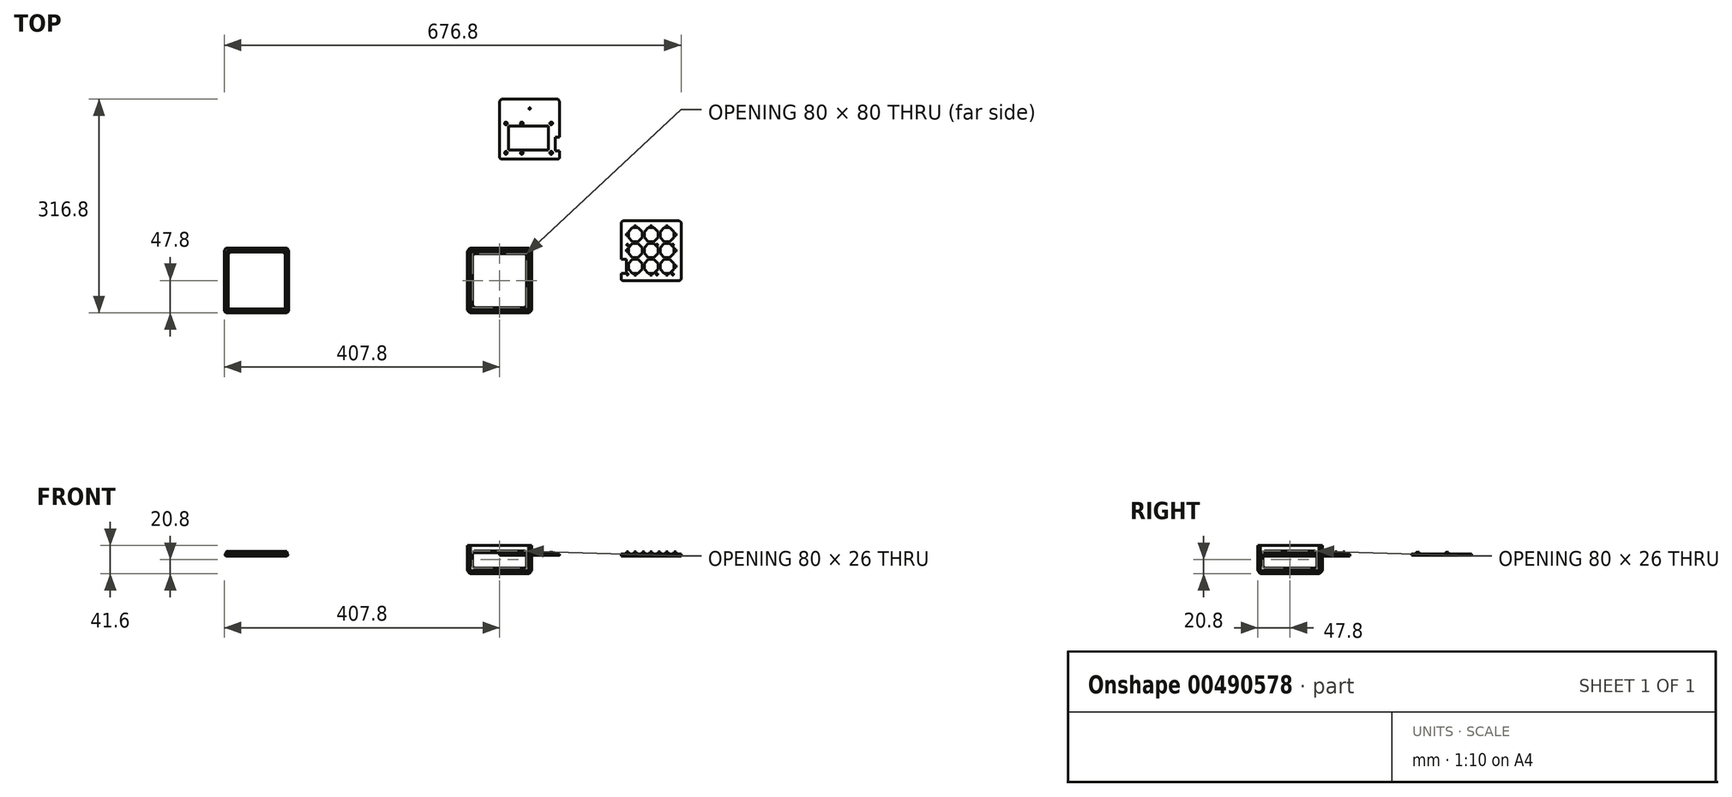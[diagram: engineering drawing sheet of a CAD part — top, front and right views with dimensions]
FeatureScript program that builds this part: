
annotation { "Feature Type Name" : "Feature", "Feature Type Description" : "" }
export const myFeature = defineFeature(function(context is Context, id is Id, definition is map)
    precondition{}
    {
        {
            assignVariable(context, id + "F0", {"name" : "Grosor", "anyValue" : 2.8});
        }
        {
            assignVariable(context, id + "F1", {"name" : "AltoPlaca", "anyValue" : 26});
        }
        {
            assignVariable(context, id + "F2", {"name" : "AltoBriX", "anyValue" : 10});
        }
        {
            var Q0;
            Q0=qCreatedBy(makeId("Top.planeOp"),FACE);
            var sketch = newSketch(context, id + "F3", { "sketchPlane" : qUnion([Q0])});
            skLineSegment(sketch, "E0.bottom", {"start": v(45, -45) * mm, "end": v(-45, -45) * mm});
            skLineSegment(sketch, "E0.top", {"start": v(45, 45) * mm, "end": v(-45, 45) * mm});
            skLineSegment(sketch, "E0.left", {"start": v(45, -45) * mm, "end": v(45, 45) * mm});
            skLineSegment(sketch, "E0.right", {"start": v(-45, -45) * mm, "end": v(-45, 45) * mm});
            skPoint(sketch, "E0.middle", {"position": v(0, 0) * mm});
            skLineSegment(sketch, "E1.0", {"start": v(47.8, 47.8) * mm, "end": v(-47.8, 47.8) * mm});
            skLineSegment(sketch, "E1.1", {"start": v(47.8, -47.8) * mm, "end": v(47.8, 47.8) * mm});
            skLineSegment(sketch, "E1.2", {"start": v(47.8, -47.8) * mm, "end": v(-47.8, -47.8) * mm});
            skLineSegment(sketch, "E1.3", {"start": v(-47.8, -47.8) * mm, "end": v(-47.8, 47.8) * mm});
            skLineSegment(sketch, "E2.bottom", {"start": v(-40, 47.8) * mm, "end": v(40, 47.8) * mm});
            skLineSegment(sketch, "E2.top", {"start": v(-40, -47.8) * mm, "end": v(40, -47.8) * mm});
            skLineSegment(sketch, "E2.left", {"start": v(-40, 47.8) * mm, "end": v(-40, -47.8) * mm});
            skLineSegment(sketch, "E2.right", {"start": v(40, 47.8) * mm, "end": v(40, -47.8) * mm});
            skLineSegment(sketch, "E3.bottom", {"start": v(-47.8, 40) * mm, "end": v(47.8, 40) * mm});
            skLineSegment(sketch, "E3.top", {"start": v(-47.8, -40) * mm, "end": v(47.8, -40) * mm});
            skLineSegment(sketch, "E3.left", {"start": v(-47.8, 40) * mm, "end": v(-47.8, -40) * mm});
            skLineSegment(sketch, "E3.right", {"start": v(47.8, 40) * mm, "end": v(47.8, -40) * mm});
            skSolve(sketch);
        }
        {
            var Q0;
            {var subQ0=sQuery(id+"F3.wireOp",EDGE,"E2.right");var subQ1=sQuery(id+"F3.wireOp",EDGE,"E0.top");var subQ2=makeQuery(id+"F3.imprint","INTERSECT",VERTEX,{"derivedFrom":[subQ1,subQ0]});Q0=makeQuery(id+"F3.imprint","IMPRINT",FACE,{"disambiguationData":[TD([[makeQuery(id+"F3.imprint","IMPRINT",EDGE,{"disambiguationData":[TD([[subQ2,-1.0]])],"derivedFrom":subQ1}),-1.0]])]});}
            var Q1;
            {var subQ7=sQuery(id+"F3.wireOp",EDGE,"E0.right");var subQ8=sQuery(id+"F3.wireOp",EDGE,"E0.top");var subQ9=makeQuery(id+"F3.imprint","INTERSECT",VERTEX,{"derivedFrom":[subQ8,subQ7]});Q1=makeQuery(id+"F3.imprint","IMPRINT",FACE,{"disambiguationData":[TD([[makeQuery(id+"F3.imprint","IMPRINT",EDGE,{"disambiguationData":[TD([[subQ9,1.0]])],"derivedFrom":subQ8}),-1.0]])]});}
            var Q2;
            {var subQ0=sQuery(id+"F3.wireOp",EDGE,"E2.right");var subQ8=sQuery(id+"F3.wireOp",EDGE,"E0.top");var subQ11=makeQuery(id+"F3.imprint","INTERSECT",VERTEX,{"derivedFrom":[subQ8,subQ0]});Q2=makeQuery(id+"F3.imprint","IMPRINT",FACE,{"disambiguationData":[TD([[makeQuery(id+"F3.imprint","IMPRINT",EDGE,{"disambiguationData":[TD([[subQ11,1.0]])],"derivedFrom":subQ8}),-1.0]])]});}
            var Q3;
            {var subQ0=sQuery(id+"F3.wireOp",EDGE,"E3.top");var subQ1=sQuery(id+"F3.wireOp",EDGE,"E0.left");var subQ2=makeQuery(id+"F3.imprint","INTERSECT",VERTEX,{"derivedFrom":[subQ1,subQ0]});Q3=makeQuery(id+"F3.imprint","IMPRINT",FACE,{"disambiguationData":[TD([[makeQuery(id+"F3.imprint","IMPRINT",EDGE,{"disambiguationData":[TD([[subQ2,-1.0]])],"derivedFrom":subQ1}),-1.0]])]});}
            var Q4;
            {var subQ0=sQuery(id+"F3.wireOp",EDGE,"E2.right");var subQ8=sQuery(id+"F3.wireOp",EDGE,"E0.bottom");var subQ11=makeQuery(id+"F3.imprint","INTERSECT",VERTEX,{"derivedFrom":[subQ8,subQ0]});Q4=makeQuery(id+"F3.imprint","IMPRINT",FACE,{"disambiguationData":[TD([[makeQuery(id+"F3.imprint","IMPRINT",EDGE,{"disambiguationData":[TD([[subQ11,1.0]])],"derivedFrom":subQ8}),1.0]])]});}
            var Q5;
            {var subQ0=sQuery(id+"F3.wireOp",EDGE,"E2.right");var subQ1=sQuery(id+"F3.wireOp",EDGE,"E0.bottom");var subQ2=makeQuery(id+"F3.imprint","INTERSECT",VERTEX,{"derivedFrom":[subQ1,subQ0]});Q5=makeQuery(id+"F3.imprint","IMPRINT",FACE,{"disambiguationData":[TD([[makeQuery(id+"F3.imprint","IMPRINT",EDGE,{"disambiguationData":[TD([[subQ2,-1.0]])],"derivedFrom":subQ1}),1.0]])]});}
            var Q6;
            {var subQ6=sQuery(id+"F3.wireOp",EDGE,"E0.right");var subQ9=sQuery(id+"F3.wireOp",EDGE,"E0.bottom");var subQ10=makeQuery(id+"F3.imprint","INTERSECT",VERTEX,{"derivedFrom":[subQ9,subQ6]});Q6=makeQuery(id+"F3.imprint","IMPRINT",FACE,{"disambiguationData":[TD([[makeQuery(id+"F3.imprint","IMPRINT",EDGE,{"disambiguationData":[TD([[subQ10,1.0]])],"derivedFrom":subQ9}),1.0]])]});}
            var Q7;
            {var subQ0=sQuery(id+"F3.wireOp",EDGE,"E3.top");var subQ1=sQuery(id+"F3.wireOp",EDGE,"E0.right");var subQ2=makeQuery(id+"F3.imprint","INTERSECT",VERTEX,{"derivedFrom":[subQ1,subQ0]});Q7=makeQuery(id+"F3.imprint","IMPRINT",FACE,{"disambiguationData":[TD([[makeQuery(id+"F3.imprint","IMPRINT",EDGE,{"disambiguationData":[TD([[subQ2,-1.0]])],"derivedFrom":subQ1}),1.0]])]});}
            var Q8;
            {var subQ0=sQuery(id+"F3.wireOp",EDGE,"E2.right");var subQ1=sQuery(id+"F3.wireOp",EDGE,"E0.bottom");var subQ2=makeQuery(id+"F3.imprint","INTERSECT",VERTEX,{"derivedFrom":[subQ1,subQ0]});Q8=makeQuery(id+"F3.imprint","IMPRINT",FACE,{"disambiguationData":[TD([[makeQuery(id+"F3.imprint","IMPRINT",EDGE,{"disambiguationData":[TD([[subQ2,1.0]])],"derivedFrom":subQ1}),-1.0]])]});}
            var Q9;
            {var subQ0=sQuery(id+"F3.wireOp",EDGE,"E2.right");var subQ1=sQuery(id+"F3.wireOp",EDGE,"E0.top");var subQ2=makeQuery(id+"F3.imprint","INTERSECT",VERTEX,{"derivedFrom":[subQ1,subQ0]});Q9=makeQuery(id+"F3.imprint","IMPRINT",FACE,{"disambiguationData":[TD([[makeQuery(id+"F3.imprint","IMPRINT",EDGE,{"disambiguationData":[TD([[subQ2,1.0]])],"derivedFrom":subQ1}),1.0]])]});}
            var Q10;
            {var subQ0=sQuery(id+"F3.wireOp",EDGE,"E0.right");var subQ1=sQuery(id+"F3.wireOp",EDGE,"E0.top");var subQ2=makeQuery(id+"F3.imprint","INTERSECT",VERTEX,{"derivedFrom":[subQ1,subQ0]});Q10=makeQuery(id+"F3.imprint","IMPRINT",FACE,{"disambiguationData":[TD([[makeQuery(id+"F3.imprint","IMPRINT",EDGE,{"disambiguationData":[TD([[subQ2,1.0]])],"derivedFrom":subQ1}),1.0]])]});}
            var Q11;
            {var subQ0=sQuery(id+"F3.wireOp",EDGE,"E3.top");var subQ1=sQuery(id+"F3.wireOp",EDGE,"E0.right");var subQ2=makeQuery(id+"F3.imprint","INTERSECT",VERTEX,{"derivedFrom":[subQ1,subQ0]});Q11=makeQuery(id+"F3.imprint","IMPRINT",FACE,{"disambiguationData":[TD([[makeQuery(id+"F3.imprint","IMPRINT",EDGE,{"disambiguationData":[TD([[subQ2,-1.0]])],"derivedFrom":subQ1}),-1.0]])]});}
            var Q12;
            {var subQ0=sQuery(id+"F3.wireOp",EDGE,"E3.top");var subQ1=sQuery(id+"F3.wireOp",EDGE,"E0.left");var subQ2=makeQuery(id+"F3.imprint","INTERSECT",VERTEX,{"derivedFrom":[subQ1,subQ0]});Q12=makeQuery(id+"F3.imprint","IMPRINT",FACE,{"disambiguationData":[TD([[makeQuery(id+"F3.imprint","IMPRINT",EDGE,{"disambiguationData":[TD([[subQ2,-1.0]])],"derivedFrom":subQ1}),1.0]])]});}
            var Q13;
            {var subQ0=sQuery(id+"F3.wireOp",EDGE,"E0.right");var subQ1=sQuery(id+"F3.wireOp",EDGE,"E0.bottom");var subQ2=makeQuery(id+"F3.imprint","INTERSECT",VERTEX,{"derivedFrom":[subQ1,subQ0]});Q13=makeQuery(id+"F3.imprint","IMPRINT",FACE,{"disambiguationData":[TD([[makeQuery(id+"F3.imprint","IMPRINT",EDGE,{"disambiguationData":[TD([[subQ2,1.0]])],"derivedFrom":subQ1}),-1.0]])]});}
            var Q14;
            {var subQ0=sQuery(id+"F3.wireOp",EDGE,"E2.right");var subQ1=sQuery(id+"F3.wireOp",EDGE,"E0.bottom");var subQ2=makeQuery(id+"F3.imprint","INTERSECT",VERTEX,{"derivedFrom":[subQ1,subQ0]});Q14=makeQuery(id+"F3.imprint","IMPRINT",FACE,{"disambiguationData":[TD([[makeQuery(id+"F3.imprint","IMPRINT",EDGE,{"disambiguationData":[TD([[subQ2,-1.0]])],"derivedFrom":subQ1}),-1.0]])]});}
            var Q15;
            {var subQ0=sQuery(id+"F3.wireOp",EDGE,"E2.right");var subQ1=sQuery(id+"F3.wireOp",EDGE,"E0.top");var subQ2=makeQuery(id+"F3.imprint","INTERSECT",VERTEX,{"derivedFrom":[subQ1,subQ0]});Q15=makeQuery(id+"F3.imprint","IMPRINT",FACE,{"disambiguationData":[TD([[makeQuery(id+"F3.imprint","IMPRINT",EDGE,{"disambiguationData":[TD([[subQ2,-1.0]])],"derivedFrom":subQ1}),1.0]])]});}
            extrude(context, id + "F4", {"entities" : qUnion([Q0, Q1, Q2, Q3, Q4, Q5, Q6, Q7, Q8, Q9, Q10, Q11, Q12, Q13, Q14, Q15]), "depth" : (getVariable(context, 'AltoBriX') + getVariable(context, 'Grosor')) * mm, "hasSecondDirection" : true, "secondDirectionOppositeDirection" : true, "secondDirectionDepth" : (getVariable(context, 'AltoPlaca') + getVariable(context, 'Grosor')) * mm});
        }
        {
            var Q0;
            {var subQ0=sQuery(id+"F3.wireOp",EDGE,"E3.top");var subQ1=sQuery(id+"F3.wireOp",EDGE,"E0.right");var subQ2=makeQuery(id+"F3.imprint","INTERSECT",VERTEX,{"derivedFrom":[subQ1,subQ0]});Q0=makeQuery(id+"F3.imprint","IMPRINT",FACE,{"disambiguationData":[TD([[makeQuery(id+"F3.imprint","IMPRINT",EDGE,{"disambiguationData":[TD([[subQ2,-1.0]])],"derivedFrom":subQ1}),-1.0]])]});}
            var Q1;
            {var subQ0=sQuery(id+"F3.wireOp",EDGE,"E2.right");var subQ1=sQuery(id+"F3.wireOp",EDGE,"E0.top");var subQ2=makeQuery(id+"F3.imprint","INTERSECT",VERTEX,{"derivedFrom":[subQ1,subQ0]});Q1=makeQuery(id+"F3.imprint","IMPRINT",FACE,{"disambiguationData":[TD([[makeQuery(id+"F3.imprint","IMPRINT",EDGE,{"disambiguationData":[TD([[subQ2,-1.0]])],"derivedFrom":subQ1}),1.0]])]});}
            var Q2;
            {var subQ0=sQuery(id+"F3.wireOp",EDGE,"E0.right");var subQ1=sQuery(id+"F3.wireOp",EDGE,"E0.top");var subQ2=makeQuery(id+"F3.imprint","INTERSECT",VERTEX,{"derivedFrom":[subQ1,subQ0]});Q2=makeQuery(id+"F3.imprint","IMPRINT",FACE,{"disambiguationData":[TD([[makeQuery(id+"F3.imprint","IMPRINT",EDGE,{"disambiguationData":[TD([[subQ2,1.0]])],"derivedFrom":subQ1}),1.0]])]});}
            var Q3;
            {var subQ0=sQuery(id+"F3.wireOp",EDGE,"E3.top");var subQ1=sQuery(id+"F3.wireOp",EDGE,"E0.left");var subQ2=makeQuery(id+"F3.imprint","INTERSECT",VERTEX,{"derivedFrom":[subQ1,subQ0]});Q3=makeQuery(id+"F3.imprint","IMPRINT",FACE,{"disambiguationData":[TD([[makeQuery(id+"F3.imprint","IMPRINT",EDGE,{"disambiguationData":[TD([[subQ2,-1.0]])],"derivedFrom":subQ1}),1.0]])]});}
            var Q4;
            {var subQ0=sQuery(id+"F3.wireOp",EDGE,"E2.right");var subQ1=sQuery(id+"F3.wireOp",EDGE,"E0.top");var subQ2=makeQuery(id+"F3.imprint","INTERSECT",VERTEX,{"derivedFrom":[subQ1,subQ0]});Q4=makeQuery(id+"F3.imprint","IMPRINT",FACE,{"disambiguationData":[TD([[makeQuery(id+"F3.imprint","IMPRINT",EDGE,{"disambiguationData":[TD([[subQ2,1.0]])],"derivedFrom":subQ1}),1.0]])]});}
            var Q5;
            {var subQ0=sQuery(id+"F3.wireOp",EDGE,"E0.right");var subQ1=sQuery(id+"F3.wireOp",EDGE,"E0.bottom");var subQ2=makeQuery(id+"F3.imprint","INTERSECT",VERTEX,{"derivedFrom":[subQ1,subQ0]});Q5=makeQuery(id+"F3.imprint","IMPRINT",FACE,{"disambiguationData":[TD([[makeQuery(id+"F3.imprint","IMPRINT",EDGE,{"disambiguationData":[TD([[subQ2,1.0]])],"derivedFrom":subQ1}),-1.0]])]});}
            var Q6;
            {var subQ0=sQuery(id+"F3.wireOp",EDGE,"E2.right");var subQ1=sQuery(id+"F3.wireOp",EDGE,"E0.bottom");var subQ2=makeQuery(id+"F3.imprint","INTERSECT",VERTEX,{"derivedFrom":[subQ1,subQ0]});Q6=makeQuery(id+"F3.imprint","IMPRINT",FACE,{"disambiguationData":[TD([[makeQuery(id+"F3.imprint","IMPRINT",EDGE,{"disambiguationData":[TD([[subQ2,-1.0]])],"derivedFrom":subQ1}),-1.0]])]});}
            var Q7;
            {var subQ0=sQuery(id+"F3.wireOp",EDGE,"E2.right");var subQ1=sQuery(id+"F3.wireOp",EDGE,"E0.bottom");var subQ2=makeQuery(id+"F3.imprint","INTERSECT",VERTEX,{"derivedFrom":[subQ1,subQ0]});Q7=makeQuery(id+"F3.imprint","IMPRINT",FACE,{"disambiguationData":[TD([[makeQuery(id+"F3.imprint","IMPRINT",EDGE,{"disambiguationData":[TD([[subQ2,1.0]])],"derivedFrom":subQ1}),-1.0]])]});}
            extrude(context, id + "F5", {"entities" : qUnion([Q0, Q1, Q2, Q3, Q4, Q5, Q6, Q7]), "operationType" : NewBodyOperationType.REMOVE, "depth" : (getVariable(context, 'AltoBriX') + getVariable(context, 'Grosor')) * mm, "hasSecondDirection" : true, "secondDirectionOppositeDirection" : true, "secondDirectionDepth" : (getVariable(context, 'AltoPlaca')) * mm});
        }
        {
            var Q0;
            {var subQ0=sQuery(id+"F3.wireOp",EDGE,"E3.top");var subQ1=sQuery(id+"F3.wireOp",EDGE,"E0.right");var subQ2=makeQuery(id+"F3.imprint","INTERSECT",VERTEX,{"derivedFrom":[subQ1,subQ0]});Q0=makeQuery(id+"F3.imprint","IMPRINT",FACE,{"disambiguationData":[TD([[makeQuery(id+"F3.imprint","IMPRINT",EDGE,{"disambiguationData":[TD([[subQ2,-1.0]])],"derivedFrom":subQ1}),1.0]])]});}
            var Q1;
            {var subQ0=sQuery(id+"F3.wireOp",EDGE,"E3.top");var subQ1=sQuery(id+"F3.wireOp",EDGE,"E0.left");var subQ2=makeQuery(id+"F3.imprint","INTERSECT",VERTEX,{"derivedFrom":[subQ1,subQ0]});Q1=makeQuery(id+"F3.imprint","IMPRINT",FACE,{"disambiguationData":[TD([[makeQuery(id+"F3.imprint","IMPRINT",EDGE,{"disambiguationData":[TD([[subQ2,-1.0]])],"derivedFrom":subQ1}),-1.0]])]});}
            var Q2;
            {var subQ0=sQuery(id+"F3.wireOp",EDGE,"E2.right");var subQ1=sQuery(id+"F3.wireOp",EDGE,"E0.bottom");var subQ2=makeQuery(id+"F3.imprint","INTERSECT",VERTEX,{"derivedFrom":[subQ1,subQ0]});Q2=makeQuery(id+"F3.imprint","IMPRINT",FACE,{"disambiguationData":[TD([[makeQuery(id+"F3.imprint","IMPRINT",EDGE,{"disambiguationData":[TD([[subQ2,-1.0]])],"derivedFrom":subQ1}),1.0]])]});}
            var Q3;
            {var subQ0=sQuery(id+"F3.wireOp",EDGE,"E2.right");var subQ1=sQuery(id+"F3.wireOp",EDGE,"E0.top");var subQ2=makeQuery(id+"F3.imprint","INTERSECT",VERTEX,{"derivedFrom":[subQ1,subQ0]});Q3=makeQuery(id+"F3.imprint","IMPRINT",FACE,{"disambiguationData":[TD([[makeQuery(id+"F3.imprint","IMPRINT",EDGE,{"disambiguationData":[TD([[subQ2,-1.0]])],"derivedFrom":subQ1}),-1.0]])]});}
            extrude(context, id + "F6", {"entities" : qUnion([Q0, Q1, Q2, Q3]), "operationType" : NewBodyOperationType.REMOVE, "depth" : (getVariable(context, 'AltoBriX') - 5) * mm, "hasSecondDirection" : true, "secondDirectionOppositeDirection" : true, "secondDirectionDepth" : (getVariable(context, 'AltoPlaca') - 5) * mm});
        }
        {
            var Q0;
            {var subQ0=sQuery(id+"F3.wireOp",EDGE,"E3.bottom");Q0=makeQuery(id+"F6.boolean.opBoolean","COPY",EDGE,{"derivedFrom":makeQuery(id+"F6.opExtrude","CAP_EDGE",EDGE,{"disambiguationData":[OSD([subQ0]),TDD([makeQuery(id+"F3.imprint","IMPRINT",EDGE,{"disambiguationData":[TD([[makeQuery(id+"F3.imprint","INTERSECT",VERTEX,{"derivedFrom":[sQuery(id+"F3.wireOp",EDGE,"E0.right"),subQ0]}),1.0]])],"derivedFrom":subQ0})])],"isStart":false})});}
            var Q1;
            {var subQ0=sQuery(id+"F3.wireOp",EDGE,"E3.bottom");Q1=makeQuery(id+"F6.boolean.opBoolean","COPY",EDGE,{"derivedFrom":makeQuery(id+"F6.opExtrude","CAP_EDGE",EDGE,{"disambiguationData":[OSD([subQ0]),TDD([makeQuery(id+"F3.imprint","IMPRINT",EDGE,{"disambiguationData":[TD([[makeQuery(id+"F3.imprint","INTERSECT",VERTEX,{"derivedFrom":[sQuery(id+"F3.wireOp",EDGE,"E0.right"),subQ0]}),1.0]])],"derivedFrom":subQ0})])],"isStart":true})});}
            var Q2;
            {var subQ0=sQuery(id+"F3.wireOp",EDGE,"E3.top");Q2=makeQuery(id+"F6.boolean.opBoolean","COPY",EDGE,{"derivedFrom":makeQuery(id+"F6.opExtrude","CAP_EDGE",EDGE,{"disambiguationData":[OSD([subQ0]),TDD([makeQuery(id+"F3.imprint","IMPRINT",EDGE,{"disambiguationData":[TD([[makeQuery(id+"F3.imprint","INTERSECT",VERTEX,{"derivedFrom":[sQuery(id+"F3.wireOp",EDGE,"E0.right"),subQ0]}),1.0]])],"derivedFrom":subQ0})])],"isStart":false})});}
            var Q3;
            {var subQ0=sQuery(id+"F3.wireOp",EDGE,"E2.right");Q3=makeQuery(id+"F6.boolean.opBoolean","COPY",EDGE,{"derivedFrom":makeQuery(id+"F6.opExtrude","CAP_EDGE",EDGE,{"disambiguationData":[OSD([subQ0]),TDD([makeQuery(id+"F3.imprint","IMPRINT",EDGE,{"disambiguationData":[TD([[makeQuery(id+"F3.imprint","INTERSECT",VERTEX,{"derivedFrom":[sQuery(id+"F3.wireOp",EDGE,"E0.bottom"),subQ0]}),-1.0]])],"derivedFrom":subQ0})])],"isStart":false})});}
            var Q4;
            {var subQ0=sQuery(id+"F3.wireOp",EDGE,"E3.top");Q4=makeQuery(id+"F6.boolean.opBoolean","COPY",EDGE,{"derivedFrom":makeQuery(id+"F6.opExtrude","CAP_EDGE",EDGE,{"disambiguationData":[OSD([subQ0]),TDD([makeQuery(id+"F3.imprint","IMPRINT",EDGE,{"disambiguationData":[TD([[makeQuery(id+"F3.imprint","INTERSECT",VERTEX,{"derivedFrom":[sQuery(id+"F3.wireOp",EDGE,"E0.left"),subQ0]}),-1.0]])],"derivedFrom":subQ0})])],"isStart":false})});}
            var Q5;
            {var subQ0=sQuery(id+"F3.wireOp",EDGE,"E3.top");Q5=makeQuery(id+"F6.boolean.opBoolean","COPY",EDGE,{"derivedFrom":makeQuery(id+"F6.opExtrude","CAP_EDGE",EDGE,{"disambiguationData":[OSD([subQ0]),TDD([makeQuery(id+"F3.imprint","IMPRINT",EDGE,{"disambiguationData":[TD([[makeQuery(id+"F3.imprint","INTERSECT",VERTEX,{"derivedFrom":[sQuery(id+"F3.wireOp",EDGE,"E0.left"),subQ0]}),-1.0]])],"derivedFrom":subQ0})])],"isStart":true})});}
            var Q6;
            {var subQ0=sQuery(id+"F3.wireOp",EDGE,"E2.right");Q6=makeQuery(id+"F6.boolean.opBoolean","COPY",EDGE,{"derivedFrom":makeQuery(id+"F6.opExtrude","CAP_EDGE",EDGE,{"disambiguationData":[OSD([subQ0]),TDD([makeQuery(id+"F3.imprint","IMPRINT",EDGE,{"disambiguationData":[TD([[makeQuery(id+"F3.imprint","INTERSECT",VERTEX,{"derivedFrom":[sQuery(id+"F3.wireOp",EDGE,"E0.bottom"),subQ0]}),-1.0]])],"derivedFrom":subQ0})])],"isStart":true})});}
            var Q7;
            {var subQ0=sQuery(id+"F3.wireOp",EDGE,"E3.top");Q7=makeQuery(id+"F6.boolean.opBoolean","COPY",EDGE,{"derivedFrom":makeQuery(id+"F6.opExtrude","CAP_EDGE",EDGE,{"disambiguationData":[OSD([subQ0]),TDD([makeQuery(id+"F3.imprint","IMPRINT",EDGE,{"disambiguationData":[TD([[makeQuery(id+"F3.imprint","INTERSECT",VERTEX,{"derivedFrom":[sQuery(id+"F3.wireOp",EDGE,"E0.right"),subQ0]}),1.0]])],"derivedFrom":subQ0})])],"isStart":true})});}
            var Q8;
            {var subQ0=sQuery(id+"F3.wireOp",EDGE,"E2.left");Q8=makeQuery(id+"F6.boolean.opBoolean","COPY",EDGE,{"derivedFrom":makeQuery(id+"F6.opExtrude","CAP_EDGE",EDGE,{"disambiguationData":[OSD([subQ0]),TDD([makeQuery(id+"F3.imprint","IMPRINT",EDGE,{"disambiguationData":[TD([[makeQuery(id+"F3.imprint","INTERSECT",VERTEX,{"derivedFrom":[sQuery(id+"F3.wireOp",EDGE,"E1.2"),subQ0]}),1.0]])],"derivedFrom":subQ0})])],"isStart":true})});}
            var Q9;
            {var subQ0=sQuery(id+"F3.wireOp",EDGE,"E2.left");Q9=makeQuery(id+"F6.boolean.opBoolean","COPY",EDGE,{"derivedFrom":makeQuery(id+"F6.opExtrude","CAP_EDGE",EDGE,{"disambiguationData":[OSD([subQ0]),TDD([makeQuery(id+"F3.imprint","IMPRINT",EDGE,{"disambiguationData":[TD([[makeQuery(id+"F3.imprint","INTERSECT",VERTEX,{"derivedFrom":[sQuery(id+"F3.wireOp",EDGE,"E1.2"),subQ0]}),1.0]])],"derivedFrom":subQ0})])],"isStart":false})});}
            var Q10;
            {var subQ0=sQuery(id+"F3.wireOp",EDGE,"E3.bottom");Q10=makeQuery(id+"F6.boolean.opBoolean","COPY",EDGE,{"derivedFrom":makeQuery(id+"F6.opExtrude","CAP_EDGE",EDGE,{"disambiguationData":[OSD([subQ0]),TDD([makeQuery(id+"F3.imprint","IMPRINT",EDGE,{"disambiguationData":[TD([[makeQuery(id+"F3.imprint","INTERSECT",VERTEX,{"derivedFrom":[sQuery(id+"F3.wireOp",EDGE,"E1.1"),subQ0]}),1.0]])],"derivedFrom":subQ0})])],"isStart":true})});}
            var Q11;
            {var subQ0=sQuery(id+"F3.wireOp",EDGE,"E3.bottom");Q11=makeQuery(id+"F6.boolean.opBoolean","COPY",EDGE,{"derivedFrom":makeQuery(id+"F6.opExtrude","CAP_EDGE",EDGE,{"disambiguationData":[OSD([subQ0]),TDD([makeQuery(id+"F3.imprint","IMPRINT",EDGE,{"disambiguationData":[TD([[makeQuery(id+"F3.imprint","INTERSECT",VERTEX,{"derivedFrom":[sQuery(id+"F3.wireOp",EDGE,"E1.1"),subQ0]}),1.0]])],"derivedFrom":subQ0})])],"isStart":false})});}
            var Q12;
            {var subQ0=sQuery(id+"F3.wireOp",EDGE,"E2.left");Q12=makeQuery(id+"F6.boolean.opBoolean","COPY",EDGE,{"derivedFrom":makeQuery(id+"F6.opExtrude","CAP_EDGE",EDGE,{"disambiguationData":[OSD([subQ0]),TDD([makeQuery(id+"F3.imprint","IMPRINT",EDGE,{"disambiguationData":[TD([[makeQuery(id+"F3.imprint","INTERSECT",VERTEX,{"derivedFrom":[sQuery(id+"F3.wireOp",EDGE,"E1.0"),subQ0]}),-1.0]])],"derivedFrom":subQ0})])],"isStart":false})});}
            var Q13;
            {var subQ0=sQuery(id+"F3.wireOp",EDGE,"E2.left");Q13=makeQuery(id+"F6.boolean.opBoolean","COPY",EDGE,{"derivedFrom":makeQuery(id+"F6.opExtrude","CAP_EDGE",EDGE,{"disambiguationData":[OSD([subQ0]),TDD([makeQuery(id+"F3.imprint","IMPRINT",EDGE,{"disambiguationData":[TD([[makeQuery(id+"F3.imprint","INTERSECT",VERTEX,{"derivedFrom":[sQuery(id+"F3.wireOp",EDGE,"E1.0"),subQ0]}),-1.0]])],"derivedFrom":subQ0})])],"isStart":true})});}
            var Q14;
            {var subQ0=sQuery(id+"F3.wireOp",EDGE,"E2.right");Q14=makeQuery(id+"F6.boolean.opBoolean","COPY",EDGE,{"derivedFrom":makeQuery(id+"F6.opExtrude","CAP_EDGE",EDGE,{"disambiguationData":[OSD([subQ0]),TDD([makeQuery(id+"F3.imprint","IMPRINT",EDGE,{"disambiguationData":[TD([[makeQuery(id+"F3.imprint","INTERSECT",VERTEX,{"derivedFrom":[sQuery(id+"F3.wireOp",EDGE,"E0.top"),subQ0]}),1.0]])],"derivedFrom":subQ0})])],"isStart":false})});}
            var Q15;
            {var subQ0=sQuery(id+"F3.wireOp",EDGE,"E2.right");Q15=makeQuery(id+"F6.boolean.opBoolean","COPY",EDGE,{"derivedFrom":makeQuery(id+"F6.opExtrude","CAP_EDGE",EDGE,{"disambiguationData":[OSD([subQ0]),TDD([makeQuery(id+"F3.imprint","IMPRINT",EDGE,{"disambiguationData":[TD([[makeQuery(id+"F3.imprint","INTERSECT",VERTEX,{"derivedFrom":[sQuery(id+"F3.wireOp",EDGE,"E0.top"),subQ0]}),1.0]])],"derivedFrom":subQ0})])],"isStart":true})});}
            var Q16;
            Q16=makeQuery(id+"F4.opExtrude","SWEPT_EDGE",EDGE,{"disambiguationData":[OSD([sQuery(id+"F3.wireOp",EDGE,"E2.right"),sQuery(id+"F3.wireOp",EDGE,"E3.top")])]});
            var Q17;
            Q17=makeQuery(id+"F4.opExtrude","SWEPT_EDGE",EDGE,{"disambiguationData":[OSD([sQuery(id+"F3.wireOp",EDGE,"E2.left"),sQuery(id+"F3.wireOp",EDGE,"E3.top")])]});
            var Q18;
            Q18=makeQuery(id+"F4.opExtrude","SWEPT_EDGE",EDGE,{"disambiguationData":[OSD([sQuery(id+"F3.wireOp",EDGE,"E2.left"),sQuery(id+"F3.wireOp",EDGE,"E3.bottom")])]});
            var Q19;
            Q19=makeQuery(id+"F4.opExtrude","SWEPT_EDGE",EDGE,{"disambiguationData":[OSD([sQuery(id+"F3.wireOp",EDGE,"E2.right"),sQuery(id+"F3.wireOp",EDGE,"E3.bottom")])]});
            fillet(context, id + "F7", {"entities" : qUnion([Q0, Q1, Q2, Q3, Q4, Q5, Q6, Q7, Q8, Q9, Q10, Q11, Q12, Q13, Q14, Q15, Q16, Q17, Q18, Q19]), "radius" : 5 * mm, "tangentPropagation" : true, "allowEdgeOverflow" : false});
        }
        {
            var Q0;
            Q0=qCreatedBy(makeId("Top.planeOp"),FACE);
            cPlane(context, id + "F8", {"entities" : qUnion([Q0]), "cplaneType" : CPlaneType.OFFSET, "offset" : (getVariable(context, 'AltoBriX') - 5) * mm, "width" : 150 * mm, "height" : 150 * mm});
        }
        {
            var Q0;
            Q0=qCreatedBy(id+"F8.planeOp",FACE);
            var sketch = newSketch(context, id + "F9", { "sketchPlane" : qUnion([Q0])});
            skLineSegment(sketch, "E4", {"start": v(0, 0) * mm, "end": v(-46.4, 0) * mm, "construction": true});
            skLineSegment(sketch, "E5", {"start": v(0, 0) * mm, "end": v(0, 46.4) * mm, "construction": true});
            skLineSegment(sketch, "E6", {"start": v(0, 0) * mm, "end": v(-16.82, 16.82) * mm, "construction": true});
            skLineSegment(sketch, "E7", {"start": v(0, 0) * mm, "end": v(10.62, -10.62) * mm, "construction": true});
            skLineSegment(sketch, "E8.bottom", {"start": v(-0.3, 45.25) * mm, "end": v(0.3, 45.25) * mm});
            skLineSegment(sketch, "E8.top", {"start": v(-0.3, 47.55) * mm, "end": v(0.3, 47.55) * mm});
            skLineSegment(sketch, "E8.left", {"start": v(-0.3, 45.25) * mm, "end": v(-0.3, 47.55) * mm});
            skLineSegment(sketch, "E8.right", {"start": v(0.3, 45.25) * mm, "end": v(0.3, 47.55) * mm});
            skPoint(sketch, "E8.middle", {"position": v(0, 46.4) * mm});
            skLineSegment(sketch, "E9", {"start": v(0, 0) * mm, "end": v(15.28, 0) * mm, "construction": true});
            skLineSegment(sketch, "E10.MirrorCS", {"start": v(0, 0) * mm, "end": v(0, -46.4) * mm, "construction": true});
            skPoint(sketch, "E11.1.0.0", {"position": v(5, 46.4) * mm});
            skPoint(sketch, "E11.1.0.1", {"position": v(5, 46.4) * mm});
            skLineSegment(sketch, "E11.1.0.2", {"start": v(4.7, 45.25) * mm, "end": v(5.3, 45.25) * mm});
            skLineSegment(sketch, "E11.1.0.3", {"start": v(4.7, 47.55) * mm, "end": v(5.3, 47.55) * mm});
            skLineSegment(sketch, "E11.1.0.4", {"start": v(4.7, 45.25) * mm, "end": v(4.7, 47.55) * mm});
            skLineSegment(sketch, "E11.1.0.5", {"start": v(5.3, 45.25) * mm, "end": v(5.3, 47.55) * mm});
            skPoint(sketch, "E11.2.0.0", {"position": v(10, 46.4) * mm});
            skPoint(sketch, "E11.2.0.1", {"position": v(10, 46.4) * mm});
            skLineSegment(sketch, "E11.2.0.2", {"start": v(9.7, 45.25) * mm, "end": v(10.3, 45.25) * mm});
            skLineSegment(sketch, "E11.2.0.3", {"start": v(9.7, 47.55) * mm, "end": v(10.3, 47.55) * mm});
            skLineSegment(sketch, "E11.2.0.4", {"start": v(9.7, 45.25) * mm, "end": v(9.7, 47.55) * mm});
            skLineSegment(sketch, "E11.2.0.5", {"start": v(10.3, 45.25) * mm, "end": v(10.3, 47.55) * mm});
            skPoint(sketch, "E11.3.0.0", {"position": v(15, 46.4) * mm});
            skPoint(sketch, "E11.3.0.1", {"position": v(15, 46.4) * mm});
            skLineSegment(sketch, "E11.3.0.2", {"start": v(14.7, 45.25) * mm, "end": v(15.3, 45.25) * mm});
            skLineSegment(sketch, "E11.3.0.3", {"start": v(14.7, 47.55) * mm, "end": v(15.3, 47.55) * mm});
            skLineSegment(sketch, "E11.3.0.4", {"start": v(14.7, 45.25) * mm, "end": v(14.7, 47.55) * mm});
            skLineSegment(sketch, "E11.3.0.5", {"start": v(15.3, 45.25) * mm, "end": v(15.3, 47.55) * mm});
            skPoint(sketch, "E11.4.0.0", {"position": v(20, 46.4) * mm});
            skPoint(sketch, "E11.4.0.1", {"position": v(20, 46.4) * mm});
            skLineSegment(sketch, "E11.4.0.2", {"start": v(19.7, 45.25) * mm, "end": v(20.3, 45.25) * mm});
            skLineSegment(sketch, "E11.4.0.3", {"start": v(19.7, 47.55) * mm, "end": v(20.3, 47.55) * mm});
            skLineSegment(sketch, "E11.4.0.4", {"start": v(19.7, 45.25) * mm, "end": v(19.7, 47.55) * mm});
            skLineSegment(sketch, "E11.4.0.5", {"start": v(20.3, 45.25) * mm, "end": v(20.3, 47.55) * mm});
            skLineSegment(sketch, "E11.direction1", {"start": v(-0.3, 45.25) * mm, "end": v(4.7, 45.25) * mm, "construction": true});
            skPoint(sketch, "E12.1.0.0", {"position": v(-5, 46.4) * mm});
            skLineSegment(sketch, "E12.1.0.1", {"start": v(-4.7, 45.25) * mm, "end": v(-4.7, 47.55) * mm});
            skLineSegment(sketch, "E12.1.0.2", {"start": v(-5.3, 45.25) * mm, "end": v(-5.3, 47.55) * mm});
            skPoint(sketch, "E12.1.0.3", {"position": v(-5, 46.4) * mm});
            skLineSegment(sketch, "E12.1.0.4", {"start": v(-5.3, 47.55) * mm, "end": v(-4.7, 47.55) * mm});
            skLineSegment(sketch, "E12.1.0.5", {"start": v(-5.3, 45.25) * mm, "end": v(-4.7, 45.25) * mm});
            skPoint(sketch, "E12.2.0.0", {"position": v(-10, 46.4) * mm});
            skLineSegment(sketch, "E12.2.0.1", {"start": v(-9.7, 45.25) * mm, "end": v(-9.7, 47.55) * mm});
            skLineSegment(sketch, "E12.2.0.2", {"start": v(-10.3, 45.25) * mm, "end": v(-10.3, 47.55) * mm});
            skPoint(sketch, "E12.2.0.3", {"position": v(-10, 46.4) * mm});
            skLineSegment(sketch, "E12.2.0.4", {"start": v(-10.3, 47.55) * mm, "end": v(-9.7, 47.55) * mm});
            skLineSegment(sketch, "E12.2.0.5", {"start": v(-10.3, 45.25) * mm, "end": v(-9.7, 45.25) * mm});
            skPoint(sketch, "E12.3.0.0", {"position": v(-15, 46.4) * mm});
            skLineSegment(sketch, "E12.3.0.1", {"start": v(-14.7, 45.25) * mm, "end": v(-14.7, 47.55) * mm});
            skLineSegment(sketch, "E12.3.0.2", {"start": v(-15.3, 45.25) * mm, "end": v(-15.3, 47.55) * mm});
            skPoint(sketch, "E12.3.0.3", {"position": v(-15, 46.4) * mm});
            skLineSegment(sketch, "E12.3.0.4", {"start": v(-15.3, 47.55) * mm, "end": v(-14.7, 47.55) * mm});
            skLineSegment(sketch, "E12.3.0.5", {"start": v(-15.3, 45.25) * mm, "end": v(-14.7, 45.25) * mm});
            skPoint(sketch, "E12.4.0.0", {"position": v(-20, 46.4) * mm});
            skLineSegment(sketch, "E12.4.0.1", {"start": v(-19.7, 45.25) * mm, "end": v(-19.7, 47.55) * mm});
            skLineSegment(sketch, "E12.4.0.2", {"start": v(-20.3, 45.25) * mm, "end": v(-20.3, 47.55) * mm});
            skPoint(sketch, "E12.4.0.3", {"position": v(-20, 46.4) * mm});
            skLineSegment(sketch, "E12.4.0.4", {"start": v(-20.3, 47.55) * mm, "end": v(-19.7, 47.55) * mm});
            skLineSegment(sketch, "E12.4.0.5", {"start": v(-20.3, 45.25) * mm, "end": v(-19.7, 45.25) * mm});
            skLineSegment(sketch, "E12.direction1", {"start": v(-0.3, 45.25) * mm, "end": v(-5.3, 45.25) * mm, "construction": true});
            skLineSegment(sketch, "E13.MirrorCS", {"start": v(-0.3, -45.25) * mm, "end": v(0.3, -45.25) * mm});
            skLineSegment(sketch, "E14.MirrorCS", {"start": v(9.7, -45.25) * mm, "end": v(10.3, -45.25) * mm});
            skLineSegment(sketch, "E15.MirrorCS", {"start": v(5.3, -45.25) * mm, "end": v(5.3, -47.55) * mm});
            skLineSegment(sketch, "E16.MirrorCS", {"start": v(4.7, -45.25) * mm, "end": v(4.7, -47.55) * mm});
            skLineSegment(sketch, "E17.MirrorCS", {"start": v(4.7, -47.55) * mm, "end": v(5.3, -47.55) * mm});
            skLineSegment(sketch, "E18.MirrorCS", {"start": v(4.7, -45.25) * mm, "end": v(5.3, -45.25) * mm});
            skLineSegment(sketch, "E19.MirrorCS", {"start": v(19.7, -45.25) * mm, "end": v(20.3, -45.25) * mm});
            skLineSegment(sketch, "E20.MirrorCS", {"start": v(-0.3, -45.25) * mm, "end": v(-0.3, -47.55) * mm});
            skLineSegment(sketch, "E21.MirrorCS", {"start": v(-0.3, -47.55) * mm, "end": v(0.3, -47.55) * mm});
            skLineSegment(sketch, "E22.MirrorCS", {"start": v(0.3, -45.25) * mm, "end": v(0.3, -47.55) * mm});
            skLineSegment(sketch, "E23.MirrorCS", {"start": v(-5.3, -45.25) * mm, "end": v(-4.7, -45.25) * mm});
            skLineSegment(sketch, "E24.MirrorCS", {"start": v(14.7, -45.25) * mm, "end": v(15.3, -45.25) * mm});
            skLineSegment(sketch, "E25.MirrorCS", {"start": v(20.3, -45.25) * mm, "end": v(20.3, -47.55) * mm});
            skLineSegment(sketch, "E26.MirrorCS", {"start": v(-20.3, -47.55) * mm, "end": v(-19.7, -47.55) * mm});
            skLineSegment(sketch, "E27.MirrorCS", {"start": v(-5.3, -47.55) * mm, "end": v(-4.7, -47.55) * mm});
            skLineSegment(sketch, "E28.MirrorCS", {"start": v(-5.3, -45.25) * mm, "end": v(-5.3, -47.55) * mm});
            skLineSegment(sketch, "E29.MirrorCS", {"start": v(19.7, -45.25) * mm, "end": v(19.7, -47.55) * mm});
            skLineSegment(sketch, "E30.MirrorCS", {"start": v(-20.3, -45.25) * mm, "end": v(-20.3, -47.55) * mm});
            skLineSegment(sketch, "E31.MirrorCS", {"start": v(-4.7, -45.25) * mm, "end": v(-4.7, -47.55) * mm});
            skLineSegment(sketch, "E32.MirrorCS", {"start": v(-0.3, -45.25) * mm, "end": v(-5.3, -45.25) * mm, "construction": true});
            skLineSegment(sketch, "E33.MirrorCS", {"start": v(-20.3, -45.25) * mm, "end": v(-19.7, -45.25) * mm});
            skLineSegment(sketch, "E34.MirrorCS", {"start": v(-15.3, -45.25) * mm, "end": v(-14.7, -45.25) * mm});
            skLineSegment(sketch, "E35.MirrorCS", {"start": v(19.7, -47.55) * mm, "end": v(20.3, -47.55) * mm});
            skLineSegment(sketch, "E36.MirrorCS", {"start": v(-19.7, -45.25) * mm, "end": v(-19.7, -47.55) * mm});
            skLineSegment(sketch, "E37.MirrorCS", {"start": v(15.3, -45.25) * mm, "end": v(15.3, -47.55) * mm});
            skLineSegment(sketch, "E38.MirrorCS", {"start": v(-15.3, -47.55) * mm, "end": v(-14.7, -47.55) * mm});
            skLineSegment(sketch, "E39.MirrorCS", {"start": v(14.7, -45.25) * mm, "end": v(14.7, -47.55) * mm});
            skLineSegment(sketch, "E40.MirrorCS", {"start": v(-15.3, -45.25) * mm, "end": v(-15.3, -47.55) * mm});
            skLineSegment(sketch, "E41.MirrorCS", {"start": v(-10.3, -45.25) * mm, "end": v(-9.7, -45.25) * mm});
            skLineSegment(sketch, "E42.MirrorCS", {"start": v(14.7, -47.55) * mm, "end": v(15.3, -47.55) * mm});
            skLineSegment(sketch, "E43.MirrorCS", {"start": v(-14.7, -45.25) * mm, "end": v(-14.7, -47.55) * mm});
            skLineSegment(sketch, "E44.MirrorCS", {"start": v(-10.3, -45.25) * mm, "end": v(-10.3, -47.55) * mm});
            skLineSegment(sketch, "E45.MirrorCS", {"start": v(9.7, -47.55) * mm, "end": v(10.3, -47.55) * mm});
            skLineSegment(sketch, "E46.MirrorCS", {"start": v(10.3, -45.25) * mm, "end": v(10.3, -47.55) * mm});
            skLineSegment(sketch, "E47.MirrorCS", {"start": v(-10.3, -47.55) * mm, "end": v(-9.7, -47.55) * mm});
            skLineSegment(sketch, "E48.MirrorCS", {"start": v(-9.7, -45.25) * mm, "end": v(-9.7, -47.55) * mm});
            skLineSegment(sketch, "E49.MirrorCS", {"start": v(9.7, -45.25) * mm, "end": v(9.7, -47.55) * mm});
            skPoint(sketch, "E50.MirrorP", {"position": v(0, -46.4) * mm});
            skPoint(sketch, "E51.MirrorP", {"position": v(-15, -46.4) * mm});
            skPoint(sketch, "E52.MirrorP", {"position": v(20, -46.4) * mm});
            skPoint(sketch, "E53.MirrorP", {"position": v(15, -46.4) * mm});
            skLineSegment(sketch, "E54.MirrorCS", {"start": v(-0.3, -45.25) * mm, "end": v(4.7, -45.25) * mm, "construction": true});
            skPoint(sketch, "E55.MirrorP", {"position": v(-5, -46.4) * mm});
            skPoint(sketch, "E56.MirrorP", {"position": v(-20, -46.4) * mm});
            skPoint(sketch, "E57.MirrorP", {"position": v(-10, -46.4) * mm});
            skPoint(sketch, "E58.MirrorP", {"position": v(10, -46.4) * mm});
            skPoint(sketch, "E59.MirrorP", {"position": v(5, -46.4) * mm});
            skLineSegment(sketch, "E60.bottom", {"start": v(-40, 46.25) * mm, "end": v(40, 46.25) * mm});
            skLineSegment(sketch, "E60.top", {"start": v(-40, 46.55) * mm, "end": v(40, 46.55) * mm});
            skLineSegment(sketch, "E60.left", {"start": v(-40, 46.25) * mm, "end": v(-40, 46.55) * mm});
            skLineSegment(sketch, "E60.right", {"start": v(40, 46.25) * mm, "end": v(40, 46.55) * mm});
            skLineSegment(sketch, "E61.MirrorCS", {"start": v(-40, -46.55) * mm, "end": v(40, -46.55) * mm});
            skLineSegment(sketch, "E62.MirrorCS", {"start": v(-40, -46.25) * mm, "end": v(40, -46.25) * mm});
            skLineSegment(sketch, "E63.MirrorCS", {"start": v(40, -46.25) * mm, "end": v(40, -46.55) * mm});
            skLineSegment(sketch, "E64.MirrorCS", {"start": v(-40, -46.25) * mm, "end": v(-40, -46.55) * mm});
            skLineSegment(sketch, "E65.bottom", {"start": v(-47.55, 0.3) * mm, "end": v(-45.25, 0.3) * mm});
            skLineSegment(sketch, "E65.top", {"start": v(-47.55, -0.3) * mm, "end": v(-45.25, -0.3) * mm});
            skLineSegment(sketch, "E65.left", {"start": v(-47.55, 0.3) * mm, "end": v(-47.55, -0.3) * mm});
            skLineSegment(sketch, "E65.right", {"start": v(-45.25, 0.3) * mm, "end": v(-45.25, -0.3) * mm});
            skPoint(sketch, "E65.middle", {"position": v(-46.4, 0) * mm});
            skLineSegment(sketch, "E66.1.0.0", {"start": v(-47.54, -4.7) * mm, "end": v(-47.54, -5.3) * mm});
            skLineSegment(sketch, "E66.1.0.1", {"start": v(-45.24, -4.7) * mm, "end": v(-45.24, -5.3) * mm});
            skPoint(sketch, "E66.1.0.2", {"position": v(-46.4, -5) * mm});
            skLineSegment(sketch, "E66.1.0.3", {"start": v(-47.54, -4.7) * mm, "end": v(-45.24, -4.7) * mm});
            skLineSegment(sketch, "E66.1.0.4", {"start": v(-47.54, -5.3) * mm, "end": v(-45.24, -5.3) * mm});
            skLineSegment(sketch, "E66.2.0.0", {"start": v(-47.53, -9.7) * mm, "end": v(-47.53, -10.3) * mm});
            skLineSegment(sketch, "E66.2.0.1", {"start": v(-45.23, -9.7) * mm, "end": v(-45.23, -10.3) * mm});
            skPoint(sketch, "E66.2.0.2", {"position": v(-46.38, -10) * mm});
            skLineSegment(sketch, "E66.2.0.3", {"start": v(-47.53, -9.7) * mm, "end": v(-45.23, -9.7) * mm});
            skLineSegment(sketch, "E66.2.0.4", {"start": v(-47.53, -10.3) * mm, "end": v(-45.23, -10.3) * mm});
            skLineSegment(sketch, "E66.3.0.0", {"start": v(-47.53, -14.7) * mm, "end": v(-47.53, -15.3) * mm});
            skLineSegment(sketch, "E66.3.0.1", {"start": v(-45.23, -14.7) * mm, "end": v(-45.23, -15.3) * mm});
            skPoint(sketch, "E66.3.0.2", {"position": v(-46.38, -15) * mm});
            skLineSegment(sketch, "E66.3.0.3", {"start": v(-47.53, -14.7) * mm, "end": v(-45.23, -14.7) * mm});
            skLineSegment(sketch, "E66.3.0.4", {"start": v(-47.53, -15.3) * mm, "end": v(-45.23, -15.3) * mm});
            skLineSegment(sketch, "E66.4.0.0", {"start": v(-47.52, -19.7) * mm, "end": v(-47.52, -20.3) * mm});
            skLineSegment(sketch, "E66.4.0.1", {"start": v(-45.22, -19.7) * mm, "end": v(-45.22, -20.3) * mm});
            skPoint(sketch, "E66.4.0.2", {"position": v(-46.37, -20) * mm});
            skLineSegment(sketch, "E66.4.0.3", {"start": v(-47.52, -19.7) * mm, "end": v(-45.22, -19.7) * mm});
            skLineSegment(sketch, "E66.4.0.4", {"start": v(-47.52, -20.3) * mm, "end": v(-45.22, -20.3) * mm});
            skLineSegment(sketch, "E66.5.0.0", {"start": v(-47.5, -24.7) * mm, "end": v(-47.5, -25.3) * mm});
            skLineSegment(sketch, "E66.5.0.1", {"start": v(-45.2, -24.7) * mm, "end": v(-45.2, -25.3) * mm});
            skPoint(sketch, "E66.5.0.2", {"position": v(-46.36, -25) * mm});
            skLineSegment(sketch, "E66.5.0.3", {"start": v(-47.5, -24.7) * mm, "end": v(-45.2, -24.7) * mm});
            skLineSegment(sketch, "E66.5.0.4", {"start": v(-47.5, -25.3) * mm, "end": v(-45.2, -25.3) * mm});
            skLineSegment(sketch, "E66.6.0.0", {"start": v(-47.5, -29.7) * mm, "end": v(-47.5, -30.3) * mm});
            skLineSegment(sketch, "E66.6.0.1", {"start": v(-45.2, -29.7) * mm, "end": v(-45.2, -30.3) * mm});
            skPoint(sketch, "E66.6.0.2", {"position": v(-46.35, -30) * mm});
            skLineSegment(sketch, "E66.6.0.3", {"start": v(-47.5, -29.7) * mm, "end": v(-45.2, -29.7) * mm});
            skLineSegment(sketch, "E66.6.0.4", {"start": v(-47.5, -30.3) * mm, "end": v(-45.2, -30.3) * mm});
            skLineSegment(sketch, "E66.direction1", {"start": v(-47.55, -0.3) * mm, "end": v(-47.54, -5.3) * mm, "construction": true});
            skLineSegment(sketch, "E67.1.0.0", {"start": v(-47.55, 4.7) * mm, "end": v(-45.25, 4.7) * mm});
            skPoint(sketch, "E67.1.0.1", {"position": v(-46.4, 5) * mm});
            skLineSegment(sketch, "E67.1.0.2", {"start": v(-47.55, 5.3) * mm, "end": v(-45.25, 5.3) * mm});
            skLineSegment(sketch, "E67.1.0.3", {"start": v(-45.25, 5.3) * mm, "end": v(-45.25, 4.7) * mm});
            skLineSegment(sketch, "E67.1.0.4", {"start": v(-47.55, 5.3) * mm, "end": v(-47.55, 4.7) * mm});
            skLineSegment(sketch, "E67.2.0.0", {"start": v(-47.55, 9.7) * mm, "end": v(-45.25, 9.7) * mm});
            skPoint(sketch, "E67.2.0.1", {"position": v(-46.4, 10) * mm});
            skLineSegment(sketch, "E67.2.0.2", {"start": v(-47.55, 10.3) * mm, "end": v(-45.25, 10.3) * mm});
            skLineSegment(sketch, "E67.2.0.3", {"start": v(-45.25, 10.3) * mm, "end": v(-45.25, 9.7) * mm});
            skLineSegment(sketch, "E67.2.0.4", {"start": v(-47.55, 10.3) * mm, "end": v(-47.55, 9.7) * mm});
            skLineSegment(sketch, "E67.3.0.0", {"start": v(-47.55, 14.7) * mm, "end": v(-45.25, 14.7) * mm});
            skPoint(sketch, "E67.3.0.1", {"position": v(-46.4, 15) * mm});
            skLineSegment(sketch, "E67.3.0.2", {"start": v(-47.55, 15.3) * mm, "end": v(-45.25, 15.3) * mm});
            skLineSegment(sketch, "E67.3.0.3", {"start": v(-45.25, 15.3) * mm, "end": v(-45.25, 14.7) * mm});
            skLineSegment(sketch, "E67.3.0.4", {"start": v(-47.55, 15.3) * mm, "end": v(-47.55, 14.7) * mm});
            skLineSegment(sketch, "E67.4.0.0", {"start": v(-47.55, 19.7) * mm, "end": v(-45.25, 19.7) * mm});
            skPoint(sketch, "E67.4.0.1", {"position": v(-46.4, 20) * mm});
            skLineSegment(sketch, "E67.4.0.2", {"start": v(-47.55, 20.3) * mm, "end": v(-45.25, 20.3) * mm});
            skLineSegment(sketch, "E67.4.0.3", {"start": v(-45.25, 20.3) * mm, "end": v(-45.25, 19.7) * mm});
            skLineSegment(sketch, "E67.4.0.4", {"start": v(-47.55, 20.3) * mm, "end": v(-47.55, 19.7) * mm});
            skLineSegment(sketch, "E67.5.0.0", {"start": v(-47.55, 24.7) * mm, "end": v(-45.25, 24.7) * mm});
            skPoint(sketch, "E67.5.0.1", {"position": v(-46.4, 25) * mm});
            skLineSegment(sketch, "E67.5.0.2", {"start": v(-47.55, 25.3) * mm, "end": v(-45.25, 25.3) * mm});
            skLineSegment(sketch, "E67.5.0.3", {"start": v(-45.25, 25.3) * mm, "end": v(-45.25, 24.7) * mm});
            skLineSegment(sketch, "E67.5.0.4", {"start": v(-47.55, 25.3) * mm, "end": v(-47.55, 24.7) * mm});
            skLineSegment(sketch, "E67.6.0.0", {"start": v(-47.55, 29.7) * mm, "end": v(-45.25, 29.7) * mm});
            skPoint(sketch, "E67.6.0.1", {"position": v(-46.4, 30) * mm});
            skLineSegment(sketch, "E67.6.0.2", {"start": v(-47.55, 30.3) * mm, "end": v(-45.25, 30.3) * mm});
            skLineSegment(sketch, "E67.6.0.3", {"start": v(-45.25, 30.3) * mm, "end": v(-45.25, 29.7) * mm});
            skLineSegment(sketch, "E67.6.0.4", {"start": v(-47.55, 30.3) * mm, "end": v(-47.55, 29.7) * mm});
            skLineSegment(sketch, "E67.direction1", {"start": v(-47.55, -0.3) * mm, "end": v(-47.55, 4.7) * mm, "construction": true});
            skLineSegment(sketch, "E68.MirrorCS", {"start": v(47.55, 0.3) * mm, "end": v(47.55, -0.3) * mm});
            skLineSegment(sketch, "E69.MirrorCS", {"start": v(47.55, -0.3) * mm, "end": v(45.25, -0.3) * mm});
            skLineSegment(sketch, "E70.MirrorCS", {"start": v(47.55, 0.3) * mm, "end": v(45.25, 0.3) * mm});
            skLineSegment(sketch, "E71.MirrorCS", {"start": v(47.5, -24.7) * mm, "end": v(47.5, -25.3) * mm});
            skLineSegment(sketch, "E72.MirrorCS", {"start": v(47.55, 20.3) * mm, "end": v(47.55, 19.7) * mm});
            skLineSegment(sketch, "E73.MirrorCS", {"start": v(45.2, -24.7) * mm, "end": v(45.2, -25.3) * mm});
            skLineSegment(sketch, "E74.MirrorCS", {"start": v(45.25, 0.3) * mm, "end": v(45.25, -0.3) * mm});
            skLineSegment(sketch, "E75.MirrorCS", {"start": v(45.25, 20.3) * mm, "end": v(45.25, 19.7) * mm});
            skLineSegment(sketch, "E76.MirrorCS", {"start": v(47.5, -24.7) * mm, "end": v(45.2, -24.7) * mm});
            skLineSegment(sketch, "E77.MirrorCS", {"start": v(47.5, -25.3) * mm, "end": v(45.2, -25.3) * mm});
            skLineSegment(sketch, "E78.MirrorCS", {"start": v(47.55, 20.3) * mm, "end": v(45.25, 20.3) * mm});
            skLineSegment(sketch, "E79.MirrorCS", {"start": v(47.55, 19.7) * mm, "end": v(45.25, 19.7) * mm});
            skLineSegment(sketch, "E80.MirrorCS", {"start": v(45.23, -9.7) * mm, "end": v(45.23, -10.3) * mm});
            skLineSegment(sketch, "E81.MirrorCS", {"start": v(45.24, -4.7) * mm, "end": v(45.24, -5.3) * mm});
            skLineSegment(sketch, "E82.MirrorCS", {"start": v(47.52, -20.3) * mm, "end": v(45.22, -20.3) * mm});
            skLineSegment(sketch, "E83.MirrorCS", {"start": v(47.53, -9.7) * mm, "end": v(47.53, -10.3) * mm});
            skLineSegment(sketch, "E84.MirrorCS", {"start": v(47.55, -0.3) * mm, "end": v(47.55, 4.7) * mm, "construction": true});
            skLineSegment(sketch, "E85.MirrorCS", {"start": v(47.53, -10.3) * mm, "end": v(45.23, -10.3) * mm});
            skLineSegment(sketch, "E86.MirrorCS", {"start": v(47.53, -9.7) * mm, "end": v(45.23, -9.7) * mm});
            skLineSegment(sketch, "E87.MirrorCS", {"start": v(47.55, 9.7) * mm, "end": v(45.25, 9.7) * mm});
            skLineSegment(sketch, "E88.MirrorCS", {"start": v(47.55, 29.7) * mm, "end": v(45.25, 29.7) * mm});
            skLineSegment(sketch, "E89.MirrorCS", {"start": v(45.22, -19.7) * mm, "end": v(45.22, -20.3) * mm});
            skLineSegment(sketch, "E90.MirrorCS", {"start": v(45.25, 30.3) * mm, "end": v(45.25, 29.7) * mm});
            skLineSegment(sketch, "E91.MirrorCS", {"start": v(47.52, -19.7) * mm, "end": v(45.22, -19.7) * mm});
            skLineSegment(sketch, "E92.MirrorCS", {"start": v(45.25, 10.3) * mm, "end": v(45.25, 9.7) * mm});
            skLineSegment(sketch, "E93.MirrorCS", {"start": v(47.54, -5.3) * mm, "end": v(45.24, -5.3) * mm});
            skLineSegment(sketch, "E94.MirrorCS", {"start": v(47.55, 5.3) * mm, "end": v(45.25, 5.3) * mm});
            skLineSegment(sketch, "E95.MirrorCS", {"start": v(45.2, -29.7) * mm, "end": v(45.2, -30.3) * mm});
            skLineSegment(sketch, "E96.MirrorCS", {"start": v(45.23, -14.7) * mm, "end": v(45.23, -15.3) * mm});
            skLineSegment(sketch, "E97.MirrorCS", {"start": v(47.55, 4.7) * mm, "end": v(45.25, 4.7) * mm});
            skLineSegment(sketch, "E98.MirrorCS", {"start": v(47.54, -4.7) * mm, "end": v(45.24, -4.7) * mm});
            skLineSegment(sketch, "E99.MirrorCS", {"start": v(47.55, 5.3) * mm, "end": v(47.55, 4.7) * mm});
            skLineSegment(sketch, "E100.MirrorCS", {"start": v(47.55, 30.3) * mm, "end": v(45.25, 30.3) * mm});
            skLineSegment(sketch, "E101.MirrorCS", {"start": v(47.55, 10.3) * mm, "end": v(45.25, 10.3) * mm});
            skLineSegment(sketch, "E102.MirrorCS", {"start": v(47.55, 24.7) * mm, "end": v(45.25, 24.7) * mm});
            skLineSegment(sketch, "E103.MirrorCS", {"start": v(47.5, -30.3) * mm, "end": v(45.2, -30.3) * mm});
            skLineSegment(sketch, "E104.MirrorCS", {"start": v(47.53, -14.7) * mm, "end": v(47.53, -15.3) * mm});
            skLineSegment(sketch, "E105.MirrorCS", {"start": v(47.55, 15.3) * mm, "end": v(47.55, 14.7) * mm});
            skLineSegment(sketch, "E106.MirrorCS", {"start": v(47.55, 10.3) * mm, "end": v(47.55, 9.7) * mm});
            skLineSegment(sketch, "E107.MirrorCS", {"start": v(47.55, 30.3) * mm, "end": v(47.55, 29.7) * mm});
            skLineSegment(sketch, "E108.MirrorCS", {"start": v(47.55, 14.7) * mm, "end": v(45.25, 14.7) * mm});
            skLineSegment(sketch, "E109.MirrorCS", {"start": v(47.54, -4.7) * mm, "end": v(47.54, -5.3) * mm});
            skLineSegment(sketch, "E110.MirrorCS", {"start": v(47.5, -29.7) * mm, "end": v(45.2, -29.7) * mm});
            skLineSegment(sketch, "E111.MirrorCS", {"start": v(47.55, 15.3) * mm, "end": v(45.25, 15.3) * mm});
            skLineSegment(sketch, "E112.MirrorCS", {"start": v(45.25, 15.3) * mm, "end": v(45.25, 14.7) * mm});
            skLineSegment(sketch, "E113.MirrorCS", {"start": v(45.25, 5.3) * mm, "end": v(45.25, 4.7) * mm});
            skLineSegment(sketch, "E114.MirrorCS", {"start": v(47.53, -14.7) * mm, "end": v(45.23, -14.7) * mm});
            skLineSegment(sketch, "E115.MirrorCS", {"start": v(47.55, 25.3) * mm, "end": v(45.25, 25.3) * mm});
            skLineSegment(sketch, "E116.MirrorCS", {"start": v(45.25, 25.3) * mm, "end": v(45.25, 24.7) * mm});
            skLineSegment(sketch, "E117.MirrorCS", {"start": v(47.53, -15.3) * mm, "end": v(45.23, -15.3) * mm});
            skLineSegment(sketch, "E118.MirrorCS", {"start": v(47.5, -29.7) * mm, "end": v(47.5, -30.3) * mm});
            skLineSegment(sketch, "E119.MirrorCS", {"start": v(47.55, -0.3) * mm, "end": v(47.54, -5.3) * mm, "construction": true});
            skLineSegment(sketch, "E120.MirrorCS", {"start": v(47.52, -19.7) * mm, "end": v(47.52, -20.3) * mm});
            skLineSegment(sketch, "E121.MirrorCS", {"start": v(47.55, 25.3) * mm, "end": v(47.55, 24.7) * mm});
            skPoint(sketch, "E122.MirrorP", {"position": v(46.4, 0) * mm});
            skPoint(sketch, "E123.MirrorP", {"position": v(46.38, -10) * mm});
            skPoint(sketch, "E124.MirrorP", {"position": v(46.38, -15) * mm});
            skPoint(sketch, "E125.MirrorP", {"position": v(46.4, 15) * mm});
            skPoint(sketch, "E126.MirrorP", {"position": v(46.4, 30) * mm});
            skPoint(sketch, "E127.MirrorP", {"position": v(46.4, 5) * mm});
            skPoint(sketch, "E128.MirrorP", {"position": v(46.36, -25) * mm});
            skPoint(sketch, "E129.MirrorP", {"position": v(46.35, -30) * mm});
            skPoint(sketch, "E130.MirrorP", {"position": v(46.4, 20) * mm});
            skPoint(sketch, "E131.MirrorP", {"position": v(46.4, 10) * mm});
            skPoint(sketch, "E132.MirrorP", {"position": v(46.4, 25) * mm});
            skPoint(sketch, "E133.MirrorP", {"position": v(46.4, -5) * mm});
            skPoint(sketch, "E134.MirrorP", {"position": v(46.37, -20) * mm});
            skLineSegment(sketch, "E135.bottom", {"start": v(-46.6, -40) * mm, "end": v(-46.2, -40) * mm});
            skLineSegment(sketch, "E135.top", {"start": v(-46.6, 40) * mm, "end": v(-46.2, 40) * mm});
            skLineSegment(sketch, "E135.left", {"start": v(-46.6, -40) * mm, "end": v(-46.6, 40) * mm});
            skLineSegment(sketch, "E135.right", {"start": v(-46.2, -40) * mm, "end": v(-46.2, 40) * mm});
            skLineSegment(sketch, "E136.bottom", {"start": v(46.6, -40) * mm, "end": v(46.2, -40) * mm});
            skLineSegment(sketch, "E136.top", {"start": v(46.6, 40) * mm, "end": v(46.2, 40) * mm});
            skLineSegment(sketch, "E136.left", {"start": v(46.6, -40) * mm, "end": v(46.6, 40) * mm});
            skLineSegment(sketch, "E136.right", {"start": v(46.2, -40) * mm, "end": v(46.2, 40) * mm});
            skSolve(sketch);
        }
        {
            var Q0;
            Q0=qSketchRegion(id+"F9",true);
            extrude(context, id + "F10", {"entities" : qUnion([Q0]), "operationType" : NewBodyOperationType.ADD, "oppositeDirection" : true, "depth" : 3 * mm, "hasDraft" : true, "draftAngle" : 3 * degree});
        }
        {
            var Q0;
            {var subQ5=sQuery(id+"F9.wireOp",EDGE,"E60.left");Q0=makeQuery(id+"F9.imprint","IMPRINT",FACE,{"disambiguationData":[TD([[makeQuery(id+"F9.imprint","IMPRINT",EDGE,{"derivedFrom":subQ5}),-1.0]])]});}
            var Q1;
            {var subQ5=sQuery(id+"F9.wireOp",EDGE,"E60.right");Q1=makeQuery(id+"F9.imprint","IMPRINT",FACE,{"disambiguationData":[TD([[makeQuery(id+"F9.imprint","IMPRINT",EDGE,{"derivedFrom":subQ5}),1.0]])]});}
            var Q2;
            {var subQ0=sQuery(id+"F9.wireOp",EDGE,"E136.left");var subQ1=sQuery(id+"F9.wireOp",EDGE,"E78.MirrorCS");var subQ2=makeQuery(id+"F9.imprint","INTERSECT",VERTEX,{"derivedFrom":[subQ1,subQ0]});Q2=makeQuery(id+"F9.imprint","IMPRINT",FACE,{"disambiguationData":[TD([[makeQuery(id+"F9.imprint","IMPRINT",EDGE,{"disambiguationData":[TD([[subQ2,-1.0]])],"derivedFrom":subQ1}),-1.0]])]});}
            var Q3;
            {var subQ0=sQuery(id+"F9.wireOp",EDGE,"E136.left");var subQ1=sQuery(id+"F9.wireOp",EDGE,"E76.MirrorCS");var subQ2=makeQuery(id+"F9.imprint","INTERSECT",VERTEX,{"derivedFrom":[subQ1,subQ0]});Q3=makeQuery(id+"F9.imprint","IMPRINT",FACE,{"disambiguationData":[TD([[makeQuery(id+"F9.imprint","IMPRINT",EDGE,{"disambiguationData":[TD([[subQ2,-1.0]])],"derivedFrom":subQ1}),-1.0]])]});}
            var Q4;
            {var subQ5=sQuery(id+"F9.wireOp",EDGE,"E63.MirrorCS");Q4=makeQuery(id+"F9.imprint","IMPRINT",FACE,{"disambiguationData":[TD([[makeQuery(id+"F9.imprint","IMPRINT",EDGE,{"derivedFrom":subQ5}),-1.0]])]});}
            var Q5;
            {var subQ5=sQuery(id+"F9.wireOp",EDGE,"E64.MirrorCS");Q5=makeQuery(id+"F9.imprint","IMPRINT",FACE,{"disambiguationData":[TD([[makeQuery(id+"F9.imprint","IMPRINT",EDGE,{"derivedFrom":subQ5}),1.0]])]});}
            var Q6;
            {var subQ0=sQuery(id+"F9.wireOp",EDGE,"E135.left");var subQ1=sQuery(id+"F9.wireOp",EDGE,"E66.4.0.4");var subQ2=makeQuery(id+"F9.imprint","INTERSECT",VERTEX,{"derivedFrom":[subQ1,subQ0]});Q6=makeQuery(id+"F9.imprint","IMPRINT",FACE,{"disambiguationData":[TD([[makeQuery(id+"F9.imprint","IMPRINT",EDGE,{"disambiguationData":[TD([[subQ2,-1.0]])],"derivedFrom":subQ1}),-1.0]])]});}
            var Q7;
            {var subQ0=sQuery(id+"F9.wireOp",EDGE,"E135.left");var subQ1=sQuery(id+"F9.wireOp",EDGE,"E67.4.0.2");var subQ2=makeQuery(id+"F9.imprint","INTERSECT",VERTEX,{"derivedFrom":[subQ1,subQ0]});Q7=makeQuery(id+"F9.imprint","IMPRINT",FACE,{"disambiguationData":[TD([[makeQuery(id+"F9.imprint","IMPRINT",EDGE,{"disambiguationData":[TD([[subQ2,-1.0]])],"derivedFrom":subQ1}),1.0]])]});}
            var Q8;
            {var subQ0=sQuery(id+"F9.wireOp",EDGE,"E60.bottom");var subQ1=sQuery(id+"F9.wireOp",EDGE,"E12.2.0.2");var subQ2=makeQuery(id+"F9.imprint","INTERSECT",VERTEX,{"derivedFrom":[subQ1,subQ0]});Q8=makeQuery(id+"F9.imprint","IMPRINT",FACE,{"disambiguationData":[TD([[makeQuery(id+"F9.imprint","IMPRINT",EDGE,{"disambiguationData":[TD([[subQ2,-1.0]])],"derivedFrom":subQ1}),1.0]])]});}
            var Q9;
            {var subQ0=sQuery(id+"F9.wireOp",EDGE,"E62.MirrorCS");var subQ1=sQuery(id+"F9.wireOp",EDGE,"E36.MirrorCS");var subQ2=makeQuery(id+"F9.imprint","INTERSECT",VERTEX,{"derivedFrom":[subQ1,subQ0]});Q9=makeQuery(id+"F9.imprint","IMPRINT",FACE,{"disambiguationData":[TD([[makeQuery(id+"F9.imprint","IMPRINT",EDGE,{"disambiguationData":[TD([[subQ2,-1.0]])],"derivedFrom":subQ1}),1.0]])]});}
            var Q10;
            {var subQ0=sQuery(id+"F9.wireOp",EDGE,"E62.MirrorCS");var subQ1=sQuery(id+"F9.wireOp",EDGE,"E43.MirrorCS");var subQ2=makeQuery(id+"F9.imprint","INTERSECT",VERTEX,{"derivedFrom":[subQ1,subQ0]});Q10=makeQuery(id+"F9.imprint","IMPRINT",FACE,{"disambiguationData":[TD([[makeQuery(id+"F9.imprint","IMPRINT",EDGE,{"disambiguationData":[TD([[subQ2,-1.0]])],"derivedFrom":subQ1}),1.0]])]});}
            var Q11;
            {var subQ0=sQuery(id+"F9.wireOp",EDGE,"E62.MirrorCS");var subQ1=sQuery(id+"F9.wireOp",EDGE,"E28.MirrorCS");var subQ2=makeQuery(id+"F9.imprint","INTERSECT",VERTEX,{"derivedFrom":[subQ1,subQ0]});Q11=makeQuery(id+"F9.imprint","IMPRINT",FACE,{"disambiguationData":[TD([[makeQuery(id+"F9.imprint","IMPRINT",EDGE,{"disambiguationData":[TD([[subQ2,-1.0]])],"derivedFrom":subQ1}),-1.0]])]});}
            var Q12;
            {var subQ0=sQuery(id+"F9.wireOp",EDGE,"E62.MirrorCS");var subQ1=sQuery(id+"F9.wireOp",EDGE,"E20.MirrorCS");var subQ2=makeQuery(id+"F9.imprint","INTERSECT",VERTEX,{"derivedFrom":[subQ1,subQ0]});Q12=makeQuery(id+"F9.imprint","IMPRINT",FACE,{"disambiguationData":[TD([[makeQuery(id+"F9.imprint","IMPRINT",EDGE,{"disambiguationData":[TD([[subQ2,-1.0]])],"derivedFrom":subQ1}),-1.0]])]});}
            var Q13;
            {var subQ0=sQuery(id+"F9.wireOp",EDGE,"E62.MirrorCS");var subQ1=sQuery(id+"F9.wireOp",EDGE,"E16.MirrorCS");var subQ2=makeQuery(id+"F9.imprint","INTERSECT",VERTEX,{"derivedFrom":[subQ1,subQ0]});Q13=makeQuery(id+"F9.imprint","IMPRINT",FACE,{"disambiguationData":[TD([[makeQuery(id+"F9.imprint","IMPRINT",EDGE,{"disambiguationData":[TD([[subQ2,-1.0]])],"derivedFrom":subQ1}),-1.0]])]});}
            var Q14;
            {var subQ0=sQuery(id+"F9.wireOp",EDGE,"E62.MirrorCS");var subQ1=sQuery(id+"F9.wireOp",EDGE,"E15.MirrorCS");var subQ2=makeQuery(id+"F9.imprint","INTERSECT",VERTEX,{"derivedFrom":[subQ1,subQ0]});Q14=makeQuery(id+"F9.imprint","IMPRINT",FACE,{"disambiguationData":[TD([[makeQuery(id+"F9.imprint","IMPRINT",EDGE,{"disambiguationData":[TD([[subQ2,-1.0]])],"derivedFrom":subQ1}),1.0]])]});}
            var Q15;
            {var subQ0=sQuery(id+"F9.wireOp",EDGE,"E62.MirrorCS");var subQ1=sQuery(id+"F9.wireOp",EDGE,"E29.MirrorCS");var subQ2=makeQuery(id+"F9.imprint","INTERSECT",VERTEX,{"derivedFrom":[subQ1,subQ0]});Q15=makeQuery(id+"F9.imprint","IMPRINT",FACE,{"disambiguationData":[TD([[makeQuery(id+"F9.imprint","IMPRINT",EDGE,{"disambiguationData":[TD([[subQ2,-1.0]])],"derivedFrom":subQ1}),-1.0]])]});}
            var Q16;
            {var subQ0=sQuery(id+"F9.wireOp",EDGE,"E62.MirrorCS");var subQ1=sQuery(id+"F9.wireOp",EDGE,"E39.MirrorCS");var subQ2=makeQuery(id+"F9.imprint","INTERSECT",VERTEX,{"derivedFrom":[subQ1,subQ0]});Q16=makeQuery(id+"F9.imprint","IMPRINT",FACE,{"disambiguationData":[TD([[makeQuery(id+"F9.imprint","IMPRINT",EDGE,{"disambiguationData":[TD([[subQ2,-1.0]])],"derivedFrom":subQ1}),-1.0]])]});}
            var Q17;
            {var subQ0=sQuery(id+"F9.wireOp",EDGE,"E136.left");var subQ1=sQuery(id+"F9.wireOp",EDGE,"E91.MirrorCS");var subQ2=makeQuery(id+"F9.imprint","INTERSECT",VERTEX,{"derivedFrom":[subQ1,subQ0]});Q17=makeQuery(id+"F9.imprint","IMPRINT",FACE,{"disambiguationData":[TD([[makeQuery(id+"F9.imprint","IMPRINT",EDGE,{"disambiguationData":[TD([[subQ2,-1.0]])],"derivedFrom":subQ1}),-1.0]])]});}
            var Q18;
            {var subQ0=sQuery(id+"F9.wireOp",EDGE,"E136.left");var subQ1=sQuery(id+"F9.wireOp",EDGE,"E85.MirrorCS");var subQ2=makeQuery(id+"F9.imprint","INTERSECT",VERTEX,{"derivedFrom":[subQ1,subQ0]});Q18=makeQuery(id+"F9.imprint","IMPRINT",FACE,{"disambiguationData":[TD([[makeQuery(id+"F9.imprint","IMPRINT",EDGE,{"disambiguationData":[TD([[subQ2,-1.0]])],"derivedFrom":subQ1}),1.0]])]});}
            var Q19;
            {var subQ0=sQuery(id+"F9.wireOp",EDGE,"E136.left");var subQ1=sQuery(id+"F9.wireOp",EDGE,"E86.MirrorCS");var subQ2=makeQuery(id+"F9.imprint","INTERSECT",VERTEX,{"derivedFrom":[subQ1,subQ0]});Q19=makeQuery(id+"F9.imprint","IMPRINT",FACE,{"disambiguationData":[TD([[makeQuery(id+"F9.imprint","IMPRINT",EDGE,{"disambiguationData":[TD([[subQ2,-1.0]])],"derivedFrom":subQ1}),-1.0]])]});}
            var Q20;
            {var subQ0=sQuery(id+"F9.wireOp",EDGE,"E136.left");var subQ1=sQuery(id+"F9.wireOp",EDGE,"E69.MirrorCS");var subQ2=makeQuery(id+"F9.imprint","INTERSECT",VERTEX,{"derivedFrom":[subQ1,subQ0]});Q20=makeQuery(id+"F9.imprint","IMPRINT",FACE,{"disambiguationData":[TD([[makeQuery(id+"F9.imprint","IMPRINT",EDGE,{"disambiguationData":[TD([[subQ2,-1.0]])],"derivedFrom":subQ1}),1.0]])]});}
            var Q21;
            {var subQ0=sQuery(id+"F9.wireOp",EDGE,"E136.left");var subQ1=sQuery(id+"F9.wireOp",EDGE,"E87.MirrorCS");var subQ2=makeQuery(id+"F9.imprint","INTERSECT",VERTEX,{"derivedFrom":[subQ1,subQ0]});Q21=makeQuery(id+"F9.imprint","IMPRINT",FACE,{"disambiguationData":[TD([[makeQuery(id+"F9.imprint","IMPRINT",EDGE,{"disambiguationData":[TD([[subQ2,-1.0]])],"derivedFrom":subQ1}),1.0]])]});}
            var Q22;
            {var subQ0=sQuery(id+"F9.wireOp",EDGE,"E136.left");var subQ1=sQuery(id+"F9.wireOp",EDGE,"E70.MirrorCS");var subQ2=makeQuery(id+"F9.imprint","INTERSECT",VERTEX,{"derivedFrom":[subQ1,subQ0]});Q22=makeQuery(id+"F9.imprint","IMPRINT",FACE,{"disambiguationData":[TD([[makeQuery(id+"F9.imprint","IMPRINT",EDGE,{"disambiguationData":[TD([[subQ2,-1.0]])],"derivedFrom":subQ1}),-1.0]])]});}
            var Q23;
            {var subQ0=sQuery(id+"F9.wireOp",EDGE,"E136.left");var subQ1=sQuery(id+"F9.wireOp",EDGE,"E101.MirrorCS");var subQ2=makeQuery(id+"F9.imprint","INTERSECT",VERTEX,{"derivedFrom":[subQ1,subQ0]});Q23=makeQuery(id+"F9.imprint","IMPRINT",FACE,{"disambiguationData":[TD([[makeQuery(id+"F9.imprint","IMPRINT",EDGE,{"disambiguationData":[TD([[subQ2,-1.0]])],"derivedFrom":subQ1}),-1.0]])]});}
            var Q24;
            {var subQ0=sQuery(id+"F9.wireOp",EDGE,"E136.left");var subQ1=sQuery(id+"F9.wireOp",EDGE,"E79.MirrorCS");var subQ2=makeQuery(id+"F9.imprint","INTERSECT",VERTEX,{"derivedFrom":[subQ1,subQ0]});Q24=makeQuery(id+"F9.imprint","IMPRINT",FACE,{"disambiguationData":[TD([[makeQuery(id+"F9.imprint","IMPRINT",EDGE,{"disambiguationData":[TD([[subQ2,-1.0]])],"derivedFrom":subQ1}),1.0]])]});}
            var Q25;
            {var subQ0=sQuery(id+"F9.wireOp",EDGE,"E60.bottom");var subQ1=sQuery(id+"F9.wireOp",EDGE,"E11.3.0.5");var subQ2=makeQuery(id+"F9.imprint","INTERSECT",VERTEX,{"derivedFrom":[subQ1,subQ0]});Q25=makeQuery(id+"F9.imprint","IMPRINT",FACE,{"disambiguationData":[TD([[makeQuery(id+"F9.imprint","IMPRINT",EDGE,{"disambiguationData":[TD([[subQ2,-1.0]])],"derivedFrom":subQ1}),-1.0]])]});}
            var Q26;
            {var subQ0=sQuery(id+"F9.wireOp",EDGE,"E60.bottom");var subQ1=sQuery(id+"F9.wireOp",EDGE,"E11.2.0.5");var subQ2=makeQuery(id+"F9.imprint","INTERSECT",VERTEX,{"derivedFrom":[subQ1,subQ0]});Q26=makeQuery(id+"F9.imprint","IMPRINT",FACE,{"disambiguationData":[TD([[makeQuery(id+"F9.imprint","IMPRINT",EDGE,{"disambiguationData":[TD([[subQ2,-1.0]])],"derivedFrom":subQ1}),-1.0]])]});}
            var Q27;
            {var subQ0=sQuery(id+"F9.wireOp",EDGE,"E60.bottom");var subQ1=sQuery(id+"F9.wireOp",EDGE,"E11.1.0.5");var subQ2=makeQuery(id+"F9.imprint","INTERSECT",VERTEX,{"derivedFrom":[subQ1,subQ0]});Q27=makeQuery(id+"F9.imprint","IMPRINT",FACE,{"disambiguationData":[TD([[makeQuery(id+"F9.imprint","IMPRINT",EDGE,{"disambiguationData":[TD([[subQ2,-1.0]])],"derivedFrom":subQ1}),-1.0]])]});}
            var Q28;
            {var subQ0=sQuery(id+"F9.wireOp",EDGE,"E60.bottom");var subQ1=sQuery(id+"F9.wireOp",EDGE,"E8.right");var subQ2=makeQuery(id+"F9.imprint","INTERSECT",VERTEX,{"derivedFrom":[subQ1,subQ0]});Q28=makeQuery(id+"F9.imprint","IMPRINT",FACE,{"disambiguationData":[TD([[makeQuery(id+"F9.imprint","IMPRINT",EDGE,{"disambiguationData":[TD([[subQ2,-1.0]])],"derivedFrom":subQ1}),-1.0]])]});}
            var Q29;
            {var subQ0=sQuery(id+"F9.wireOp",EDGE,"E60.bottom");var subQ1=sQuery(id+"F9.wireOp",EDGE,"E8.left");var subQ2=makeQuery(id+"F9.imprint","INTERSECT",VERTEX,{"derivedFrom":[subQ1,subQ0]});Q29=makeQuery(id+"F9.imprint","IMPRINT",FACE,{"disambiguationData":[TD([[makeQuery(id+"F9.imprint","IMPRINT",EDGE,{"disambiguationData":[TD([[subQ2,-1.0]])],"derivedFrom":subQ1}),1.0]])]});}
            var Q30;
            {var subQ0=sQuery(id+"F9.wireOp",EDGE,"E60.bottom");var subQ1=sQuery(id+"F9.wireOp",EDGE,"E12.1.0.2");var subQ2=makeQuery(id+"F9.imprint","INTERSECT",VERTEX,{"derivedFrom":[subQ1,subQ0]});Q30=makeQuery(id+"F9.imprint","IMPRINT",FACE,{"disambiguationData":[TD([[makeQuery(id+"F9.imprint","IMPRINT",EDGE,{"disambiguationData":[TD([[subQ2,-1.0]])],"derivedFrom":subQ1}),1.0]])]});}
            var Q31;
            {var subQ0=sQuery(id+"F9.wireOp",EDGE,"E60.bottom");var subQ1=sQuery(id+"F9.wireOp",EDGE,"E12.3.0.2");var subQ2=makeQuery(id+"F9.imprint","INTERSECT",VERTEX,{"derivedFrom":[subQ1,subQ0]});Q31=makeQuery(id+"F9.imprint","IMPRINT",FACE,{"disambiguationData":[TD([[makeQuery(id+"F9.imprint","IMPRINT",EDGE,{"disambiguationData":[TD([[subQ2,-1.0]])],"derivedFrom":subQ1}),1.0]])]});}
            var Q32;
            {var subQ0=sQuery(id+"F9.wireOp",EDGE,"E135.left");var subQ1=sQuery(id+"F9.wireOp",EDGE,"E67.3.0.2");var subQ2=makeQuery(id+"F9.imprint","INTERSECT",VERTEX,{"derivedFrom":[subQ1,subQ0]});Q32=makeQuery(id+"F9.imprint","IMPRINT",FACE,{"disambiguationData":[TD([[makeQuery(id+"F9.imprint","IMPRINT",EDGE,{"disambiguationData":[TD([[subQ2,-1.0]])],"derivedFrom":subQ1}),1.0]])]});}
            var Q33;
            {var subQ0=sQuery(id+"F9.wireOp",EDGE,"E135.left");var subQ1=sQuery(id+"F9.wireOp",EDGE,"E67.2.0.2");var subQ2=makeQuery(id+"F9.imprint","INTERSECT",VERTEX,{"derivedFrom":[subQ1,subQ0]});Q33=makeQuery(id+"F9.imprint","IMPRINT",FACE,{"disambiguationData":[TD([[makeQuery(id+"F9.imprint","IMPRINT",EDGE,{"disambiguationData":[TD([[subQ2,-1.0]])],"derivedFrom":subQ1}),1.0]])]});}
            var Q34;
            {var subQ0=sQuery(id+"F9.wireOp",EDGE,"E135.left");var subQ1=sQuery(id+"F9.wireOp",EDGE,"E67.1.0.2");var subQ2=makeQuery(id+"F9.imprint","INTERSECT",VERTEX,{"derivedFrom":[subQ1,subQ0]});Q34=makeQuery(id+"F9.imprint","IMPRINT",FACE,{"disambiguationData":[TD([[makeQuery(id+"F9.imprint","IMPRINT",EDGE,{"disambiguationData":[TD([[subQ2,-1.0]])],"derivedFrom":subQ1}),1.0]])]});}
            var Q35;
            {var subQ0=sQuery(id+"F9.wireOp",EDGE,"E135.left");var subQ1=sQuery(id+"F9.wireOp",EDGE,"E65.bottom");var subQ2=makeQuery(id+"F9.imprint","INTERSECT",VERTEX,{"derivedFrom":[subQ1,subQ0]});Q35=makeQuery(id+"F9.imprint","IMPRINT",FACE,{"disambiguationData":[TD([[makeQuery(id+"F9.imprint","IMPRINT",EDGE,{"disambiguationData":[TD([[subQ2,-1.0]])],"derivedFrom":subQ1}),1.0]])]});}
            var Q36;
            {var subQ0=sQuery(id+"F9.wireOp",EDGE,"E135.left");var subQ1=sQuery(id+"F9.wireOp",EDGE,"E66.1.0.4");var subQ2=makeQuery(id+"F9.imprint","INTERSECT",VERTEX,{"derivedFrom":[subQ1,subQ0]});Q36=makeQuery(id+"F9.imprint","IMPRINT",FACE,{"disambiguationData":[TD([[makeQuery(id+"F9.imprint","IMPRINT",EDGE,{"disambiguationData":[TD([[subQ2,-1.0]])],"derivedFrom":subQ1}),-1.0]])]});}
            var Q37;
            {var subQ0=sQuery(id+"F9.wireOp",EDGE,"E135.left");var subQ1=sQuery(id+"F9.wireOp",EDGE,"E65.top");var subQ2=makeQuery(id+"F9.imprint","INTERSECT",VERTEX,{"derivedFrom":[subQ1,subQ0]});Q37=makeQuery(id+"F9.imprint","IMPRINT",FACE,{"disambiguationData":[TD([[makeQuery(id+"F9.imprint","IMPRINT",EDGE,{"disambiguationData":[TD([[subQ2,-1.0]])],"derivedFrom":subQ1}),-1.0]])]});}
            var Q38;
            {var subQ0=sQuery(id+"F9.wireOp",EDGE,"E135.left");var subQ1=sQuery(id+"F9.wireOp",EDGE,"E66.2.0.4");var subQ2=makeQuery(id+"F9.imprint","INTERSECT",VERTEX,{"derivedFrom":[subQ1,subQ0]});Q38=makeQuery(id+"F9.imprint","IMPRINT",FACE,{"disambiguationData":[TD([[makeQuery(id+"F9.imprint","IMPRINT",EDGE,{"disambiguationData":[TD([[subQ2,-1.0]])],"derivedFrom":subQ1}),-1.0]])]});}
            var Q39;
            {var subQ0=sQuery(id+"F9.wireOp",EDGE,"E135.left");var subQ1=sQuery(id+"F9.wireOp",EDGE,"E66.3.0.4");var subQ2=makeQuery(id+"F9.imprint","INTERSECT",VERTEX,{"derivedFrom":[subQ1,subQ0]});Q39=makeQuery(id+"F9.imprint","IMPRINT",FACE,{"disambiguationData":[TD([[makeQuery(id+"F9.imprint","IMPRINT",EDGE,{"disambiguationData":[TD([[subQ2,-1.0]])],"derivedFrom":subQ1}),-1.0]])]});}
            extrude(context, id + "F11", {"entities" : qUnion([Q0, Q1, Q2, Q3, Q4, Q5, Q6, Q7, Q8, Q9, Q10, Q11, Q12, Q13, Q14, Q15, Q16, Q17, Q18, Q19, Q20, Q21, Q22, Q23, Q24, Q25, Q26, Q27, Q28, Q29, Q30, Q31, Q32, Q33, Q34, Q35, Q36, Q37, Q38, Q39]), "operationType" : NewBodyOperationType.REMOVE, "oppositeDirection" : true, "depth" : 2 * mm, "hasDraft" : true, "draftAngle" : 3 * degree});
        }
        {
            var Q0;
            {var subQ0=sQuery(id+"F3.wireOp",EDGE,"E0.right");var subQ1=sQuery(id+"F3.wireOp",EDGE,"E0.top");var subQ2=makeQuery(id+"F3.imprint","INTERSECT",VERTEX,{"derivedFrom":[subQ1,subQ0]});Q0=makeQuery(id+"F3.imprint","IMPRINT",FACE,{"disambiguationData":[TD([[makeQuery(id+"F3.imprint","IMPRINT",EDGE,{"disambiguationData":[TD([[subQ2,1.0]])],"derivedFrom":subQ1}),1.0]])]});}
            var Q1;
            {var subQ0=sQuery(id+"F3.wireOp",EDGE,"E2.right");var subQ1=sQuery(id+"F3.wireOp",EDGE,"E0.top");var subQ2=makeQuery(id+"F3.imprint","INTERSECT",VERTEX,{"derivedFrom":[subQ1,subQ0]});Q1=makeQuery(id+"F3.imprint","IMPRINT",FACE,{"disambiguationData":[TD([[makeQuery(id+"F3.imprint","IMPRINT",EDGE,{"disambiguationData":[TD([[subQ2,1.0]])],"derivedFrom":subQ1}),1.0]])]});}
            var Q2;
            {var subQ0=sQuery(id+"F3.wireOp",EDGE,"E2.right");var subQ1=sQuery(id+"F3.wireOp",EDGE,"E0.bottom");var subQ2=makeQuery(id+"F3.imprint","INTERSECT",VERTEX,{"derivedFrom":[subQ1,subQ0]});Q2=makeQuery(id+"F3.imprint","IMPRINT",FACE,{"disambiguationData":[TD([[makeQuery(id+"F3.imprint","IMPRINT",EDGE,{"disambiguationData":[TD([[subQ2,1.0]])],"derivedFrom":subQ1}),-1.0]])]});}
            var Q3;
            {var subQ0=sQuery(id+"F3.wireOp",EDGE,"E0.right");var subQ1=sQuery(id+"F3.wireOp",EDGE,"E0.bottom");var subQ2=makeQuery(id+"F3.imprint","INTERSECT",VERTEX,{"derivedFrom":[subQ1,subQ0]});Q3=makeQuery(id+"F3.imprint","IMPRINT",FACE,{"disambiguationData":[TD([[makeQuery(id+"F3.imprint","IMPRINT",EDGE,{"disambiguationData":[TD([[subQ2,1.0]])],"derivedFrom":subQ1}),-1.0]])]});}
            extrude(context, id + "F12", {"entities" : qUnion([Q0, Q1, Q2, Q3]), "operationType" : NewBodyOperationType.ADD, "endBound" : BoundingType.SYMMETRIC, "depth" : (getVariable(context, 'Grosor')) * mm});
        }
        {
            var Q0;
            Q0=makeQuery(id+"F12.opExtrude","SWEPT_EDGE",EDGE,{"disambiguationData":[OSD([sQuery(id+"F3.wireOp",EDGE,"E2.left"),sQuery(id+"F3.wireOp",EDGE,"E3.bottom")])]});
            var Q1;
            Q1=makeQuery(id+"F12.opExtrude","SWEPT_EDGE",EDGE,{"disambiguationData":[OSD([sQuery(id+"F3.wireOp",EDGE,"E2.right"),sQuery(id+"F3.wireOp",EDGE,"E3.bottom")])]});
            var Q2;
            Q2=makeQuery(id+"F12.opExtrude","SWEPT_EDGE",EDGE,{"disambiguationData":[OSD([sQuery(id+"F3.wireOp",EDGE,"E2.right"),sQuery(id+"F3.wireOp",EDGE,"E3.top")])]});
            var Q3;
            Q3=makeQuery(id+"F12.opExtrude","SWEPT_EDGE",EDGE,{"disambiguationData":[OSD([sQuery(id+"F3.wireOp",EDGE,"E2.left"),sQuery(id+"F3.wireOp",EDGE,"E3.top")])]});
            chamfer(context, id + "F13", {"entities" : qUnion([Q0, Q1, Q2, Q3]), "width" : 5 * mm, "tangentPropagation" : true});
        }
        {
            var Q0;
            {var subQ0=sQuery(id+"F3.wireOp",EDGE,"E1.3");Q0=makeQuery(id+"F3vxCluZQKjuGS6_1.boolean.opBoolean","MERGE",EDGE,{"derivedFrom":[makeQuery(id+"F6.opExtrude","CAP_EDGE",EDGE,{"disambiguationData":[OSD([subQ0]),TDD([makeQuery(id+"F3.imprint","IMPRINT",EDGE,{"disambiguationData":[TD([[makeQuery(id+"F3.imprint","INTERSECT",VERTEX,{"derivedFrom":[sQuery(id+"F3.wireOp",EDGE,"E1.2"),subQ0]}),-1.0]])],"derivedFrom":subQ0})])],"isStart":false}),makeQuery(id+"F6.opExtrude","CAP_EDGE",EDGE,{"disambiguationData":[OSD([subQ0]),TDD([makeQuery(id+"F3.imprint","IMPRINT",EDGE,{"disambiguationData":[TD([[makeQuery(id+"F3.imprint","INTERSECT",VERTEX,{"derivedFrom":[sQuery(id+"F3.wireOp",EDGE,"E1.0"),subQ0]}),1.0]])],"derivedFrom":subQ0})])],"isStart":false}),makeQuery(id+"F3vxCluZQKjuGS6_1.opExtrude","CAP_EDGE",EDGE,{"disambiguationData":[OSD([sQuery(id+"FG7JfQnFfKm0W8e.wireOp",EDGE,"a4df6a7b-901c-458c-aeef-db07d71890a7.3"),sQuery(id+"FG7JfQnFfKm0W8e.wireOp",EDGE,"3a78ae17-f210-4514-9efc-eef556d70575.left")])],"isStart":true})]});}
            var Q1;
            {var subQ0=sQuery(id+"F3.wireOp",EDGE,"E1.0");Q1=makeQuery(id+"F3vxCluZQKjuGS6_1.boolean.opBoolean","MERGE",EDGE,{"derivedFrom":[makeQuery(id+"F6.opExtrude","CAP_EDGE",EDGE,{"disambiguationData":[OSD([subQ0]),TDD([makeQuery(id+"F3.imprint","IMPRINT",EDGE,{"disambiguationData":[TD([[makeQuery(id+"F3.imprint","INTERSECT",VERTEX,{"derivedFrom":[subQ0,sQuery(id+"F3.wireOp",EDGE,"E1.1")]}),-1.0]])],"derivedFrom":subQ0})])],"isStart":false}),makeQuery(id+"F6.opExtrude","CAP_EDGE",EDGE,{"disambiguationData":[OSD([subQ0]),TDD([makeQuery(id+"F3.imprint","IMPRINT",EDGE,{"disambiguationData":[TD([[makeQuery(id+"F3.imprint","INTERSECT",VERTEX,{"derivedFrom":[subQ0,sQuery(id+"F3.wireOp",EDGE,"E1.3")]}),1.0]])],"derivedFrom":subQ0})])],"isStart":false}),makeQuery(id+"F3vxCluZQKjuGS6_1.opExtrude","CAP_EDGE",EDGE,{"disambiguationData":[OSD([sQuery(id+"FG7JfQnFfKm0W8e.wireOp",EDGE,"a4df6a7b-901c-458c-aeef-db07d71890a7.0"),sQuery(id+"FG7JfQnFfKm0W8e.wireOp",EDGE,"28a57de8-ee20-4f04-b501-8f9bbeeccb0a.bottom")])],"isStart":true})]});}
            var Q2;
            Q2=makeQuery(id+"F4.opExtrude","SWEPT_EDGE",EDGE,{"disambiguationData":[OSD([sQuery(id+"F3.wireOp",EDGE,"E1.0"),sQuery(id+"F3.wireOp",EDGE,"E1.3")])]});
            var Q3;
            {var subQ0=sQuery(id+"F3.wireOp",EDGE,"E1.1");Q3=makeQuery(id+"F3vxCluZQKjuGS6_1.boolean.opBoolean","MERGE",EDGE,{"derivedFrom":[makeQuery(id+"F6.opExtrude","CAP_EDGE",EDGE,{"disambiguationData":[OSD([subQ0]),TDD([makeQuery(id+"F3.imprint","IMPRINT",EDGE,{"disambiguationData":[TD([[makeQuery(id+"F3.imprint","INTERSECT",VERTEX,{"derivedFrom":[subQ0,sQuery(id+"F3.wireOp",EDGE,"E1.2")]}),-1.0]])],"derivedFrom":subQ0})])],"isStart":false}),makeQuery(id+"F6.opExtrude","CAP_EDGE",EDGE,{"disambiguationData":[OSD([subQ0]),TDD([makeQuery(id+"F3.imprint","IMPRINT",EDGE,{"disambiguationData":[TD([[makeQuery(id+"F3.imprint","INTERSECT",VERTEX,{"derivedFrom":[sQuery(id+"F3.wireOp",EDGE,"E1.0"),subQ0]}),1.0]])],"derivedFrom":subQ0})])],"isStart":false}),makeQuery(id+"F3vxCluZQKjuGS6_1.opExtrude","CAP_EDGE",EDGE,{"disambiguationData":[OSD([sQuery(id+"FG7JfQnFfKm0W8e.wireOp",EDGE,"a4df6a7b-901c-458c-aeef-db07d71890a7.1"),sQuery(id+"FG7JfQnFfKm0W8e.wireOp",EDGE,"3a78ae17-f210-4514-9efc-eef556d70575.right")])],"isStart":true})]});}
            var Q4;
            Q4=makeQuery(id+"F4.opExtrude","SWEPT_EDGE",EDGE,{"disambiguationData":[OSD([sQuery(id+"F3.wireOp",EDGE,"E1.0"),sQuery(id+"F3.wireOp",EDGE,"E1.1")])]});
            var Q5;
            Q5=makeQuery(id+"F4.opExtrude","SWEPT_EDGE",EDGE,{"disambiguationData":[OSD([sQuery(id+"F3.wireOp",EDGE,"E1.1"),sQuery(id+"F3.wireOp",EDGE,"E1.2")])]});
            var Q6;
            Q6=makeQuery(id+"F4.opExtrude","SWEPT_EDGE",EDGE,{"disambiguationData":[OSD([sQuery(id+"F3.wireOp",EDGE,"E1.2"),sQuery(id+"F3.wireOp",EDGE,"E1.3")])]});
            var Q7;
            {var subQ0=sQuery(id+"F3.wireOp",EDGE,"E1.2");Q7=makeQuery(id+"F3vxCluZQKjuGS6_1.boolean.opBoolean","MERGE",EDGE,{"derivedFrom":[makeQuery(id+"F6.opExtrude","CAP_EDGE",EDGE,{"disambiguationData":[OSD([subQ0]),TDD([makeQuery(id+"F3.imprint","IMPRINT",EDGE,{"disambiguationData":[TD([[makeQuery(id+"F3.imprint","INTERSECT",VERTEX,{"derivedFrom":[sQuery(id+"F3.wireOp",EDGE,"E1.1"),subQ0]}),-1.0]])],"derivedFrom":subQ0})])],"isStart":false}),makeQuery(id+"F6.opExtrude","CAP_EDGE",EDGE,{"disambiguationData":[OSD([subQ0]),TDD([makeQuery(id+"F3.imprint","IMPRINT",EDGE,{"disambiguationData":[TD([[makeQuery(id+"F3.imprint","INTERSECT",VERTEX,{"derivedFrom":[subQ0,sQuery(id+"F3.wireOp",EDGE,"E1.3")]}),1.0]])],"derivedFrom":subQ0})])],"isStart":false}),makeQuery(id+"F3vxCluZQKjuGS6_1.opExtrude","CAP_EDGE",EDGE,{"disambiguationData":[OSD([sQuery(id+"FG7JfQnFfKm0W8e.wireOp",EDGE,"a4df6a7b-901c-458c-aeef-db07d71890a7.2"),sQuery(id+"FG7JfQnFfKm0W8e.wireOp",EDGE,"28a57de8-ee20-4f04-b501-8f9bbeeccb0a.top")])],"isStart":true})]});}
            var Q8;
            Q8=makeQuery(id+"F4.opExtrude","CAP_EDGE",EDGE,{"disambiguationData":[OSD([sQuery(id+"F3.wireOp",EDGE,"E1.2")])],"isStart":true});
            var Q9;
            Q9=makeQuery(id+"F4.opExtrude","CAP_EDGE",EDGE,{"disambiguationData":[OSD([sQuery(id+"F3.wireOp",EDGE,"E1.0")])],"isStart":true});
            var Q10;
            Q10=makeQuery(id+"F4.opExtrude","CAP_EDGE",EDGE,{"disambiguationData":[OSD([sQuery(id+"F3.wireOp",EDGE,"E1.1")])],"isStart":true});
            var Q11;
            Q11=makeQuery(id+"F4.opExtrude","CAP_EDGE",EDGE,{"disambiguationData":[OSD([sQuery(id+"F3.wireOp",EDGE,"E1.3")])],"isStart":true});
            chamfer(context, id + "F14", {"entities" : qUnion([Q0, Q1, Q2, Q3, Q4, Q5, Q6, Q7, Q8, Q9, Q10, Q11]), "width" : 4 * mm, "tangentPropagation" : true});
        }
        {
            var Q0;
            Q0=makeQuery(id+"F5.boolean.opBoolean","COPY",EDGE,{"derivedFrom":makeQuery(id+"F5.opExtrude","CAP_EDGE",EDGE,{"disambiguationData":[OSD([sQuery(id+"F3.wireOp",EDGE,"E0.left")])],"isStart":true})});
            var Q1;
            Q1=makeQuery(id+"F5.boolean.opBoolean","COPY",EDGE,{"derivedFrom":makeQuery(id+"F5.opExtrude","CAP_EDGE",EDGE,{"disambiguationData":[OSD([sQuery(id+"F3.wireOp",EDGE,"E0.bottom")])],"isStart":true})});
            var Q2;
            Q2=makeQuery(id+"F5.boolean.opBoolean","COPY",EDGE,{"derivedFrom":makeQuery(id+"F5.opExtrude","CAP_EDGE",EDGE,{"disambiguationData":[OSD([sQuery(id+"F3.wireOp",EDGE,"E0.top")])],"isStart":true})});
            var Q3;
            Q3=makeQuery(id+"F5.boolean.opBoolean","COPY",EDGE,{"derivedFrom":makeQuery(id+"F5.opExtrude","CAP_EDGE",EDGE,{"disambiguationData":[OSD([sQuery(id+"F3.wireOp",EDGE,"E0.right")])],"isStart":true})});
            var Q4;
            {var subQ0=sQuery(id+"F3.wireOp",EDGE,"E3.bottom");var subQ1=sQuery(id+"F3.wireOp",EDGE,"E2.left");var subQ2=sQuery(id+"F3.wireOp",EDGE,"E0.right");var subQ3=sQuery(id+"F3.wireOp",EDGE,"E0.top");Q4=makeQuery(id+"F12.boolean.opBoolean","SPLIT",EDGE,{"disambiguationData":[TD([makeQuery(id+"F12.opExtrude","CAP_FACE",FACE,{"disambiguationData":[OSD([subQ3,subQ2,subQ1,subQ0])],"isStart":true})])],"derivedFrom":makeQuery(id+"F5.boolean.opBoolean","COPY",EDGE,{"derivedFrom":makeQuery(id+"F5.opExtrude","SWEPT_EDGE",EDGE,{"disambiguationData":[OSD([subQ3,subQ2])]})})});}
            var Q5;
            {var subQ0=sQuery(id+"F3.wireOp",EDGE,"E3.bottom");var subQ1=sQuery(id+"F3.wireOp",EDGE,"E2.right");var subQ2=sQuery(id+"F3.wireOp",EDGE,"E0.left");var subQ3=sQuery(id+"F3.wireOp",EDGE,"E0.top");Q5=makeQuery(id+"F12.boolean.opBoolean","SPLIT",EDGE,{"disambiguationData":[TD([makeQuery(id+"F12.opExtrude","CAP_FACE",FACE,{"disambiguationData":[OSD([subQ3,subQ2,subQ1,subQ0])],"isStart":true})])],"derivedFrom":makeQuery(id+"F5.boolean.opBoolean","COPY",EDGE,{"derivedFrom":makeQuery(id+"F5.opExtrude","SWEPT_EDGE",EDGE,{"disambiguationData":[OSD([subQ3,subQ2])]})})});}
            var Q6;
            {var subQ0=sQuery(id+"F3.wireOp",EDGE,"E0.bottom");var subQ1=sQuery(id+"F3.wireOp",EDGE,"E3.top");var subQ2=sQuery(id+"F3.wireOp",EDGE,"E2.right");var subQ3=sQuery(id+"F3.wireOp",EDGE,"E0.left");Q6=makeQuery(id+"F12.boolean.opBoolean","SPLIT",EDGE,{"disambiguationData":[TD([makeQuery(id+"F12.opExtrude","CAP_FACE",FACE,{"disambiguationData":[OSD([subQ0,subQ3,subQ2,subQ1])],"isStart":true})])],"derivedFrom":makeQuery(id+"F5.boolean.opBoolean","COPY",EDGE,{"derivedFrom":makeQuery(id+"F5.opExtrude","SWEPT_EDGE",EDGE,{"disambiguationData":[OSD([subQ0,subQ3])]})})});}
            var Q7;
            {var subQ0=sQuery(id+"F3.wireOp",EDGE,"E0.bottom");var subQ1=sQuery(id+"F3.wireOp",EDGE,"E3.top");var subQ2=sQuery(id+"F3.wireOp",EDGE,"E2.left");var subQ3=sQuery(id+"F3.wireOp",EDGE,"E0.right");Q7=makeQuery(id+"F12.boolean.opBoolean","SPLIT",EDGE,{"disambiguationData":[TD([makeQuery(id+"F12.opExtrude","CAP_FACE",FACE,{"disambiguationData":[OSD([subQ0,subQ3,subQ2,subQ1])],"isStart":true})])],"derivedFrom":makeQuery(id+"F5.boolean.opBoolean","COPY",EDGE,{"derivedFrom":makeQuery(id+"F5.opExtrude","SWEPT_EDGE",EDGE,{"disambiguationData":[OSD([subQ0,subQ3])]})})});}
            var Q8;
            {var subQ0=sQuery(id+"F3.wireOp",EDGE,"E3.bottom");var subQ1=sQuery(id+"F3.wireOp",EDGE,"E2.right");var subQ2=sQuery(id+"F3.wireOp",EDGE,"E0.top");var subQ3=sQuery(id+"F3.wireOp",EDGE,"E0.left");Q8=makeQuery(id+"F12.boolean.opBoolean","SPLIT",EDGE,{"disambiguationData":[TD([makeQuery(id+"F12.opExtrude","CAP_FACE",FACE,{"disambiguationData":[OSD([subQ2,subQ3,subQ1,subQ0])],"isStart":false})])],"derivedFrom":makeQuery(id+"F5.boolean.opBoolean","COPY",EDGE,{"derivedFrom":makeQuery(id+"F5.opExtrude","SWEPT_EDGE",EDGE,{"disambiguationData":[OSD([subQ2,subQ3])]})})});}
            var Q9;
            {var subQ0=sQuery(id+"F3.wireOp",EDGE,"E3.bottom");var subQ1=sQuery(id+"F3.wireOp",EDGE,"E2.left");var subQ2=sQuery(id+"F3.wireOp",EDGE,"E0.top");var subQ3=sQuery(id+"F3.wireOp",EDGE,"E0.right");Q9=makeQuery(id+"F12.boolean.opBoolean","SPLIT",EDGE,{"disambiguationData":[TD([makeQuery(id+"F12.opExtrude","CAP_FACE",FACE,{"disambiguationData":[OSD([subQ2,subQ3,subQ1,subQ0])],"isStart":false})])],"derivedFrom":makeQuery(id+"F5.boolean.opBoolean","COPY",EDGE,{"derivedFrom":makeQuery(id+"F5.opExtrude","SWEPT_EDGE",EDGE,{"disambiguationData":[OSD([subQ2,subQ3])]})})});}
            chamfer(context, id + "F15", {"entities" : qUnion([Q0, Q1, Q2, Q3, Q4, Q5, Q6, Q7, Q8, Q9]), "width" : 3 * mm, "tangentPropagation" : true});
        }
        {
            var Q0;
            {var subQ0=sQuery(id+"F3.wireOp",EDGE,"E3.top");var subQ1=sQuery(id+"F3.wireOp",EDGE,"E2.right");var subQ2=sQuery(id+"F3.wireOp",EDGE,"E0.bottom");var subQ3=sQuery(id+"F3.wireOp",EDGE,"E0.left");Q0=makeQuery(id+"F12.boolean.opBoolean","SPLIT",EDGE,{"disambiguationData":[TD([makeQuery(id+"F12.opExtrude","CAP_FACE",FACE,{"disambiguationData":[OSD([subQ2,subQ3,subQ1,subQ0])],"isStart":false})])],"derivedFrom":makeQuery(id+"F5.boolean.opBoolean","COPY",EDGE,{"derivedFrom":makeQuery(id+"F5.opExtrude","SWEPT_EDGE",EDGE,{"disambiguationData":[OSD([subQ2,subQ3])]})})});}
            var Q1;
            {var subQ0=sQuery(id+"F3.wireOp",EDGE,"E3.top");var subQ1=sQuery(id+"F3.wireOp",EDGE,"E2.left");var subQ2=sQuery(id+"F3.wireOp",EDGE,"E0.bottom");var subQ3=sQuery(id+"F3.wireOp",EDGE,"E0.right");Q1=makeQuery(id+"F12.boolean.opBoolean","SPLIT",EDGE,{"disambiguationData":[TD([makeQuery(id+"F12.opExtrude","CAP_FACE",FACE,{"disambiguationData":[OSD([subQ2,subQ3,subQ1,subQ0])],"isStart":false})])],"derivedFrom":makeQuery(id+"F5.boolean.opBoolean","COPY",EDGE,{"derivedFrom":makeQuery(id+"F5.opExtrude","SWEPT_EDGE",EDGE,{"disambiguationData":[OSD([subQ2,subQ3])]})})});}
            fillet(context, id + "F16", {"entities" : qUnion([Q0, Q1]), "radius" : 3 * mm, "tangentPropagation" : true, "allowEdgeOverflow" : false});
        }
        {
            var Q0;
            Q0=qCreatedBy(makeId("Top.planeOp"),FACE);
            var sketch = newSketch(context, id + "F17", { "sketchPlane" : qUnion([Q0])});
            skLineSegment(sketch, "E137", {"start": v(0, 0) * mm, "end": v(-360, 0) * mm, "construction": true});
            skLineSegment(sketch, "E138.bottom", {"start": v(-407.8, 47.8) * mm, "end": v(-312.2, 47.8) * mm});
            skLineSegment(sketch, "E138.top", {"start": v(-407.8, -47.8) * mm, "end": v(-312.2, -47.8) * mm});
            skLineSegment(sketch, "E138.left", {"start": v(-407.8, 47.8) * mm, "end": v(-407.8, -47.8) * mm});
            skLineSegment(sketch, "E138.right", {"start": v(-312.2, 47.8) * mm, "end": v(-312.2, -47.8) * mm});
            skPoint(sketch, "E138.middle", {"position": v(-360, 0) * mm});
            skSolve(sketch);
        }
        {
            var Q0;
            Q0=qSketchRegion(id+"F17",true);
            extrude(context, id + "F18", {"entities" : qUnion([Q0]), "oppositeDirection" : true, "depth" : (getVariable(context, 'Grosor')) * mm});
        }
        {
            var Q0;
            Q0=qCreatedBy(makeId("Top.planeOp"),FACE);
            var sketch = newSketch(context, id + "F19", { "sketchPlane" : qUnion([Q0])});
            skLineSegment(sketch, "E139", {"start": v(0, 0) * mm, "end": v(-360, 0) * mm, "construction": true});
            skLineSegment(sketch, "E140.bottom", {"start": v(-404.75, 44.75) * mm, "end": v(-315.25, 44.75) * mm});
            skLineSegment(sketch, "E140.top", {"start": v(-404.75, -44.75) * mm, "end": v(-315.25, -44.75) * mm});
            skLineSegment(sketch, "E140.left", {"start": v(-404.75, 44.75) * mm, "end": v(-404.75, -44.75) * mm});
            skLineSegment(sketch, "E140.right", {"start": v(-315.25, 44.75) * mm, "end": v(-315.25, -44.75) * mm});
            skPoint(sketch, "E140.middle", {"position": v(-360, 0) * mm});
            skLineSegment(sketch, "E141.bottom", {"start": v(-402.2, 42.2) * mm, "end": v(-317.8, 42.2) * mm});
            skLineSegment(sketch, "E141.top", {"start": v(-402.2, -42.2) * mm, "end": v(-317.8, -42.2) * mm});
            skLineSegment(sketch, "E141.left", {"start": v(-402.2, 42.2) * mm, "end": v(-402.2, -42.2) * mm});
            skLineSegment(sketch, "E141.right", {"start": v(-317.8, 42.2) * mm, "end": v(-317.8, -42.2) * mm});
            skSolve(sketch);
        }
        {
            var Q0;
            Q0=qSketchRegion(id+"F19",true);
            extrude(context, id + "F20", {"entities" : qUnion([Q0]), "operationType" : NewBodyOperationType.ADD, "depth" : (getVariable(context, 'Grosor') + 1) * mm});
        }
        {
            var Q0;
            Q0=makeQuery(id+"F18.opExtrude","CAP_FACE",FACE,{"disambiguationData":[OSD([sQuery(id+"F17.wireOp",EDGE,"E138.bottom"),sQuery(id+"F17.wireOp",EDGE,"E138.top"),sQuery(id+"F17.wireOp",EDGE,"E138.left"),sQuery(id+"F17.wireOp",EDGE,"E138.right")])],"isStart":false});
            var Q1;
            Q1=makeQuery(id+"F18.opExtrude","SWEPT_EDGE",EDGE,{"disambiguationData":[OSD([sQuery(id+"F17.wireOp",EDGE,"E138.bottom"),sQuery(id+"F17.wireOp",EDGE,"E138.left")])]});
            var Q2;
            Q2=makeQuery(id+"F18.opExtrude","SWEPT_EDGE",EDGE,{"disambiguationData":[OSD([sQuery(id+"F17.wireOp",EDGE,"E138.bottom"),sQuery(id+"F17.wireOp",EDGE,"E138.right")])]});
            var Q3;
            Q3=makeQuery(id+"F18.opExtrude","SWEPT_EDGE",EDGE,{"disambiguationData":[OSD([sQuery(id+"F17.wireOp",EDGE,"E138.top"),sQuery(id+"F17.wireOp",EDGE,"E138.right")])]});
            var Q4;
            Q4=makeQuery(id+"F18.opExtrude","SWEPT_EDGE",EDGE,{"disambiguationData":[OSD([sQuery(id+"F17.wireOp",EDGE,"E138.top"),sQuery(id+"F17.wireOp",EDGE,"E138.left")])]});
            chamfer(context, id + "F21", {"entities" : qUnion([Q0, Q1, Q2, Q3, Q4]), "width" : 2.8 * mm, "tangentPropagation" : true});
        }
        {
            var Q0;
            Q0=makeQuery(id+"F20.opExtrude","SWEPT_EDGE",EDGE,{"disambiguationData":[OSD([sQuery(id+"F19.wireOp",EDGE,"E140.bottom"),sQuery(id+"F19.wireOp",EDGE,"E140.left")])]});
            var Q1;
            Q1=makeQuery(id+"F20.opExtrude","SWEPT_EDGE",EDGE,{"disambiguationData":[OSD([sQuery(id+"F19.wireOp",EDGE,"E141.bottom"),sQuery(id+"F19.wireOp",EDGE,"E141.left")])]});
            var Q2;
            Q2=makeQuery(id+"F20.opExtrude","SWEPT_EDGE",EDGE,{"disambiguationData":[OSD([sQuery(id+"F19.wireOp",EDGE,"E141.bottom"),sQuery(id+"F19.wireOp",EDGE,"E141.right")])]});
            var Q3;
            Q3=makeQuery(id+"F20.opExtrude","SWEPT_EDGE",EDGE,{"disambiguationData":[OSD([sQuery(id+"F19.wireOp",EDGE,"E140.bottom"),sQuery(id+"F19.wireOp",EDGE,"E140.right")])]});
            chamfer(context, id + "F22", {"entities" : qUnion([Q0, Q1, Q2, Q3]), "width" : 3 * mm, "tangentPropagation" : true});
        }
        {
            var Q0;
            Q0=makeQuery(id+"F20.opExtrude","SWEPT_EDGE",EDGE,{"disambiguationData":[OSD([sQuery(id+"F19.wireOp",EDGE,"E140.top"),sQuery(id+"F19.wireOp",EDGE,"E140.right")])]});
            var Q1;
            Q1=makeQuery(id+"F20.opExtrude","SWEPT_EDGE",EDGE,{"disambiguationData":[OSD([sQuery(id+"F19.wireOp",EDGE,"E140.top"),sQuery(id+"F19.wireOp",EDGE,"E140.left")])]});
            var Q2;
            Q2=makeQuery(id+"F20.opExtrude","SWEPT_EDGE",EDGE,{"disambiguationData":[OSD([sQuery(id+"F19.wireOp",EDGE,"E141.top"),sQuery(id+"F19.wireOp",EDGE,"E141.left")])]});
            var Q3;
            Q3=makeQuery(id+"F20.opExtrude","SWEPT_EDGE",EDGE,{"disambiguationData":[OSD([sQuery(id+"F19.wireOp",EDGE,"E141.top"),sQuery(id+"F19.wireOp",EDGE,"E141.right")])]});
            fillet(context, id + "F23", {"entities" : qUnion([Q0, Q1, Q2, Q3]), "radius" : 3 * mm, "tangentPropagation" : true, "allowEdgeOverflow" : false});
        }
        {
            var Q0;
            Q0=qCreatedBy(makeId("Top.planeOp"),FACE);
            var sketch = newSketch(context, id + "F24", { "sketchPlane" : qUnion([Q0])});
            skLineSegment(sketch, "E142", {"start": v(0, 0) * mm, "end": v(-360, 0) * mm, "construction": true});
            skLineSegment(sketch, "E143", {"start": v(-360, 0) * mm, "end": v(-360, -23.5) * mm, "construction": true});
            skLineSegment(sketch, "E144", {"start": v(-360, -23.5) * mm, "end": v(-383.5, -23.5) * mm, "construction": true});
            skLineSegment(sketch, "E145.bottom", {"start": v(-386, -16) * mm, "end": v(-381, -16) * mm});
            skLineSegment(sketch, "E145.top", {"start": v(-386, -31) * mm, "end": v(-381, -31) * mm});
            skLineSegment(sketch, "E145.left", {"start": v(-391, -21) * mm, "end": v(-391, -26) * mm});
            skLineSegment(sketch, "E145.right", {"start": v(-376, -21) * mm, "end": v(-376, -26) * mm});
            skPoint(sketch, "E145.middle", {"position": v(-383.5, -23.5) * mm});
            skPoint(sketch, "E146.visualSharp", {"position": v(-391, -16) * mm});
            skArc(sketch, "E146.filletArc", {"start": v(-386, -16) * mm, "mid": v(-389.54, -17.46) * mm, "end": v(-391, -21) * mm});
            skPoint(sketch, "E147.visualSharp", {"position": v(-376, -16) * mm});
            skArc(sketch, "E147.filletArc", {"start": v(-376, -21) * mm, "mid": v(-377.46, -17.46) * mm, "end": v(-381, -16) * mm});
            skPoint(sketch, "E148.visualSharp", {"position": v(-376, -31) * mm});
            skArc(sketch, "E148.filletArc", {"start": v(-381, -31) * mm, "mid": v(-377.46, -29.54) * mm, "end": v(-376, -26) * mm});
            skPoint(sketch, "E149.visualSharp", {"position": v(-391, -31) * mm});
            skArc(sketch, "E149.filletArc", {"start": v(-391, -26) * mm, "mid": v(-389.54, -29.54) * mm, "end": v(-386, -31) * mm});
            skArc(sketch, "E150.0.1.0", {"start": v(-386, 7.5) * mm, "mid": v(-389.54, 6.04) * mm, "end": v(-391, 2.5) * mm});
            skPoint(sketch, "E150.0.1.1", {"position": v(-376, -7.5) * mm});
            skPoint(sketch, "E150.0.1.2", {"position": v(-376, 7.5) * mm});
            skArc(sketch, "E150.0.1.3", {"start": v(-381, -7.5) * mm, "mid": v(-377.46, -6.04) * mm, "end": v(-376, -2.5) * mm});
            skArc(sketch, "E150.0.1.4", {"start": v(-376, 2.5) * mm, "mid": v(-377.46, 6.04) * mm, "end": v(-381, 7.5) * mm});
            skPoint(sketch, "E150.0.1.5", {"position": v(-383.5, 0) * mm});
            skPoint(sketch, "E150.0.1.6", {"position": v(-391, 7.5) * mm});
            skLineSegment(sketch, "E150.0.1.7", {"start": v(-391, 2.5) * mm, "end": v(-391, -2.5) * mm});
            skArc(sketch, "E150.0.1.8", {"start": v(-391, -2.5) * mm, "mid": v(-389.54, -6.04) * mm, "end": v(-386, -7.5) * mm});
            skPoint(sketch, "E150.0.1.9", {"position": v(-391, -7.5) * mm});
            skLineSegment(sketch, "E150.0.1.10", {"start": v(-376, 2.5) * mm, "end": v(-376, -2.5) * mm});
            skLineSegment(sketch, "E150.0.1.11", {"start": v(-386, 7.5) * mm, "end": v(-381, 7.5) * mm});
            skLineSegment(sketch, "E150.0.1.12", {"start": v(-386, -7.5) * mm, "end": v(-381, -7.5) * mm});
            skArc(sketch, "E150.0.2.0", {"start": v(-386, 31) * mm, "mid": v(-389.54, 29.54) * mm, "end": v(-391, 26) * mm});
            skPoint(sketch, "E150.0.2.1", {"position": v(-376, 16) * mm});
            skPoint(sketch, "E150.0.2.2", {"position": v(-376, 31) * mm});
            skArc(sketch, "E150.0.2.3", {"start": v(-381, 16) * mm, "mid": v(-377.46, 17.46) * mm, "end": v(-376, 21) * mm});
            skArc(sketch, "E150.0.2.4", {"start": v(-376, 26) * mm, "mid": v(-377.46, 29.54) * mm, "end": v(-381, 31) * mm});
            skPoint(sketch, "E150.0.2.5", {"position": v(-383.5, 23.5) * mm});
            skPoint(sketch, "E150.0.2.6", {"position": v(-391, 31) * mm});
            skLineSegment(sketch, "E150.0.2.7", {"start": v(-391, 26) * mm, "end": v(-391, 21) * mm});
            skArc(sketch, "E150.0.2.8", {"start": v(-391, 21) * mm, "mid": v(-389.54, 17.46) * mm, "end": v(-386, 16) * mm});
            skPoint(sketch, "E150.0.2.9", {"position": v(-391, 16) * mm});
            skLineSegment(sketch, "E150.0.2.10", {"start": v(-376, 26) * mm, "end": v(-376, 21) * mm});
            skLineSegment(sketch, "E150.0.2.11", {"start": v(-386, 31) * mm, "end": v(-381, 31) * mm});
            skLineSegment(sketch, "E150.0.2.12", {"start": v(-386, 16) * mm, "end": v(-381, 16) * mm});
            skArc(sketch, "E150.1.0.0", {"start": v(-362.5, -16) * mm, "mid": v(-366.04, -17.46) * mm, "end": v(-367.5, -21) * mm});
            skPoint(sketch, "E150.1.0.1", {"position": v(-352.5, -31) * mm});
            skPoint(sketch, "E150.1.0.2", {"position": v(-352.5, -16) * mm});
            skArc(sketch, "E150.1.0.3", {"start": v(-357.5, -31) * mm, "mid": v(-353.96, -29.54) * mm, "end": v(-352.5, -26) * mm});
            skArc(sketch, "E150.1.0.4", {"start": v(-352.5, -21) * mm, "mid": v(-353.96, -17.46) * mm, "end": v(-357.5, -16) * mm});
            skPoint(sketch, "E150.1.0.5", {"position": v(-360, -23.5) * mm});
            skPoint(sketch, "E150.1.0.6", {"position": v(-367.5, -16) * mm});
            skLineSegment(sketch, "E150.1.0.7", {"start": v(-367.5, -21) * mm, "end": v(-367.5, -26) * mm});
            skArc(sketch, "E150.1.0.8", {"start": v(-367.5, -26) * mm, "mid": v(-366.04, -29.54) * mm, "end": v(-362.5, -31) * mm});
            skPoint(sketch, "E150.1.0.9", {"position": v(-367.5, -31) * mm});
            skLineSegment(sketch, "E150.1.0.10", {"start": v(-352.5, -21) * mm, "end": v(-352.5, -26) * mm});
            skLineSegment(sketch, "E150.1.0.11", {"start": v(-362.5, -16) * mm, "end": v(-357.5, -16) * mm});
            skLineSegment(sketch, "E150.1.0.12", {"start": v(-362.5, -31) * mm, "end": v(-357.5, -31) * mm});
            skArc(sketch, "E150.1.1.0", {"start": v(-362.5, 7.5) * mm, "mid": v(-366.04, 6.04) * mm, "end": v(-367.5, 2.5) * mm});
            skPoint(sketch, "E150.1.1.1", {"position": v(-352.5, -7.5) * mm});
            skPoint(sketch, "E150.1.1.2", {"position": v(-352.5, 7.5) * mm});
            skArc(sketch, "E150.1.1.3", {"start": v(-357.5, -7.5) * mm, "mid": v(-353.96, -6.04) * mm, "end": v(-352.5, -2.5) * mm});
            skArc(sketch, "E150.1.1.4", {"start": v(-352.5, 2.5) * mm, "mid": v(-353.96, 6.04) * mm, "end": v(-357.5, 7.5) * mm});
            skPoint(sketch, "E150.1.1.5", {"position": v(-360, 0) * mm});
            skPoint(sketch, "E150.1.1.6", {"position": v(-367.5, 7.5) * mm});
            skLineSegment(sketch, "E150.1.1.7", {"start": v(-367.5, 2.5) * mm, "end": v(-367.5, -2.5) * mm});
            skArc(sketch, "E150.1.1.8", {"start": v(-367.5, -2.5) * mm, "mid": v(-366.04, -6.04) * mm, "end": v(-362.5, -7.5) * mm});
            skPoint(sketch, "E150.1.1.9", {"position": v(-367.5, -7.5) * mm});
            skLineSegment(sketch, "E150.1.1.10", {"start": v(-352.5, 2.5) * mm, "end": v(-352.5, -2.5) * mm});
            skLineSegment(sketch, "E150.1.1.11", {"start": v(-362.5, 7.5) * mm, "end": v(-357.5, 7.5) * mm});
            skLineSegment(sketch, "E150.1.1.12", {"start": v(-362.5, -7.5) * mm, "end": v(-357.5, -7.5) * mm});
            skArc(sketch, "E150.1.2.0", {"start": v(-362.5, 31) * mm, "mid": v(-366.04, 29.54) * mm, "end": v(-367.5, 26) * mm});
            skPoint(sketch, "E150.1.2.1", {"position": v(-352.5, 16) * mm});
            skPoint(sketch, "E150.1.2.2", {"position": v(-352.5, 31) * mm});
            skArc(sketch, "E150.1.2.3", {"start": v(-357.5, 16) * mm, "mid": v(-353.96, 17.46) * mm, "end": v(-352.5, 21) * mm});
            skArc(sketch, "E150.1.2.4", {"start": v(-352.5, 26) * mm, "mid": v(-353.96, 29.54) * mm, "end": v(-357.5, 31) * mm});
            skPoint(sketch, "E150.1.2.5", {"position": v(-360, 23.5) * mm});
            skPoint(sketch, "E150.1.2.6", {"position": v(-367.5, 31) * mm});
            skLineSegment(sketch, "E150.1.2.7", {"start": v(-367.5, 26) * mm, "end": v(-367.5, 21) * mm});
            skArc(sketch, "E150.1.2.8", {"start": v(-367.5, 21) * mm, "mid": v(-366.04, 17.46) * mm, "end": v(-362.5, 16) * mm});
            skPoint(sketch, "E150.1.2.9", {"position": v(-367.5, 16) * mm});
            skLineSegment(sketch, "E150.1.2.10", {"start": v(-352.5, 26) * mm, "end": v(-352.5, 21) * mm});
            skLineSegment(sketch, "E150.1.2.11", {"start": v(-362.5, 31) * mm, "end": v(-357.5, 31) * mm});
            skLineSegment(sketch, "E150.1.2.12", {"start": v(-362.5, 16) * mm, "end": v(-357.5, 16) * mm});
            skArc(sketch, "E150.2.0.0", {"start": v(-339, -16) * mm, "mid": v(-342.54, -17.46) * mm, "end": v(-344, -21) * mm});
            skPoint(sketch, "E150.2.0.1", {"position": v(-329, -31) * mm});
            skPoint(sketch, "E150.2.0.2", {"position": v(-329, -16) * mm});
            skArc(sketch, "E150.2.0.3", {"start": v(-334, -31) * mm, "mid": v(-330.46, -29.54) * mm, "end": v(-329, -26) * mm});
            skArc(sketch, "E150.2.0.4", {"start": v(-329, -21) * mm, "mid": v(-330.46, -17.46) * mm, "end": v(-334, -16) * mm});
            skPoint(sketch, "E150.2.0.5", {"position": v(-336.5, -23.5) * mm});
            skPoint(sketch, "E150.2.0.6", {"position": v(-344, -16) * mm});
            skLineSegment(sketch, "E150.2.0.7", {"start": v(-344, -21) * mm, "end": v(-344, -26) * mm});
            skArc(sketch, "E150.2.0.8", {"start": v(-344, -26) * mm, "mid": v(-342.54, -29.54) * mm, "end": v(-339, -31) * mm});
            skPoint(sketch, "E150.2.0.9", {"position": v(-344, -31) * mm});
            skLineSegment(sketch, "E150.2.0.10", {"start": v(-329, -21) * mm, "end": v(-329, -26) * mm});
            skLineSegment(sketch, "E150.2.0.11", {"start": v(-339, -16) * mm, "end": v(-334, -16) * mm});
            skLineSegment(sketch, "E150.2.0.12", {"start": v(-339, -31) * mm, "end": v(-334, -31) * mm});
            skArc(sketch, "E150.2.1.0", {"start": v(-339, 7.5) * mm, "mid": v(-342.54, 6.04) * mm, "end": v(-344, 2.5) * mm});
            skPoint(sketch, "E150.2.1.1", {"position": v(-329, -7.5) * mm});
            skPoint(sketch, "E150.2.1.2", {"position": v(-329, 7.5) * mm});
            skArc(sketch, "E150.2.1.3", {"start": v(-334, -7.5) * mm, "mid": v(-330.46, -6.04) * mm, "end": v(-329, -2.5) * mm});
            skArc(sketch, "E150.2.1.4", {"start": v(-329, 2.5) * mm, "mid": v(-330.46, 6.04) * mm, "end": v(-334, 7.5) * mm});
            skPoint(sketch, "E150.2.1.5", {"position": v(-336.5, 0) * mm});
            skPoint(sketch, "E150.2.1.6", {"position": v(-344, 7.5) * mm});
            skLineSegment(sketch, "E150.2.1.7", {"start": v(-344, 2.5) * mm, "end": v(-344, -2.5) * mm});
            skArc(sketch, "E150.2.1.8", {"start": v(-344, -2.5) * mm, "mid": v(-342.54, -6.04) * mm, "end": v(-339, -7.5) * mm});
            skPoint(sketch, "E150.2.1.9", {"position": v(-344, -7.5) * mm});
            skLineSegment(sketch, "E150.2.1.10", {"start": v(-329, 2.5) * mm, "end": v(-329, -2.5) * mm});
            skLineSegment(sketch, "E150.2.1.11", {"start": v(-339, 7.5) * mm, "end": v(-334, 7.5) * mm});
            skLineSegment(sketch, "E150.2.1.12", {"start": v(-339, -7.5) * mm, "end": v(-334, -7.5) * mm});
            skArc(sketch, "E150.2.2.0", {"start": v(-339, 31) * mm, "mid": v(-342.54, 29.54) * mm, "end": v(-344, 26) * mm});
            skPoint(sketch, "E150.2.2.1", {"position": v(-329, 16) * mm});
            skPoint(sketch, "E150.2.2.2", {"position": v(-329, 31) * mm});
            skArc(sketch, "E150.2.2.3", {"start": v(-334, 16) * mm, "mid": v(-330.46, 17.46) * mm, "end": v(-329, 21) * mm});
            skArc(sketch, "E150.2.2.4", {"start": v(-329, 26) * mm, "mid": v(-330.46, 29.54) * mm, "end": v(-334, 31) * mm});
            skPoint(sketch, "E150.2.2.5", {"position": v(-336.5, 23.5) * mm});
            skPoint(sketch, "E150.2.2.6", {"position": v(-344, 31) * mm});
            skLineSegment(sketch, "E150.2.2.7", {"start": v(-344, 26) * mm, "end": v(-344, 21) * mm});
            skArc(sketch, "E150.2.2.8", {"start": v(-344, 21) * mm, "mid": v(-342.54, 17.46) * mm, "end": v(-339, 16) * mm});
            skPoint(sketch, "E150.2.2.9", {"position": v(-344, 16) * mm});
            skLineSegment(sketch, "E150.2.2.10", {"start": v(-329, 26) * mm, "end": v(-329, 21) * mm});
            skLineSegment(sketch, "E150.2.2.11", {"start": v(-339, 31) * mm, "end": v(-334, 31) * mm});
            skLineSegment(sketch, "E150.2.2.12", {"start": v(-339, 16) * mm, "end": v(-334, 16) * mm});
            skLineSegment(sketch, "E150.direction1", {"start": v(-391, -31) * mm, "end": v(-367.5, -31) * mm, "construction": true});
            skLineSegment(sketch, "E150.direction2", {"start": v(-391, -31) * mm, "end": v(-391, -7.5) * mm, "construction": true});
            skSolve(sketch);
        }
        {
            var Q0;
            Q0=qCreatedBy(makeId("Top.planeOp"),FACE);
            var sketch = newSketch(context, id + "F25", { "sketchPlane" : qUnion([Q0])});
            skLineSegment(sketch, "E151", {"start": v(0, 0) * mm, "end": v(180, 0) * mm, "construction": true});
            skLineSegment(sketch, "E152.bottom", {"start": v(180, 0) * mm, "end": v(269, 0) * mm});
            skLineSegment(sketch, "E152.top", {"start": v(180, 89) * mm, "end": v(269, 89) * mm});
            skLineSegment(sketch, "E152.left", {"start": v(180, 0) * mm, "end": v(180, 89) * mm});
            skLineSegment(sketch, "E152.right", {"start": v(269, 0) * mm, "end": v(269, 89) * mm});
            skSolve(sketch);
        }
        {
            var Q0;
            Q0=qSketchRegion(id+"F25",true);
            extrude(context, id + "F26", {"entities" : qUnion([Q0]), "oppositeDirection" : true, "depth" : (getVariable(context, 'Grosor')) * mm, "hasSecondDirection" : true, "secondDirectionOppositeDirection" : false, "secondDirectionDepth" : 3.5 * mm});
        }
        {
            var Q0;
            Q0=qCreatedBy(makeId("Top.planeOp"),FACE);
            var sketch = newSketch(context, id + "F27", { "sketchPlane" : qUnion([Q0])});
            skLineSegment(sketch, "E153", {"start": v(0, 0) * mm, "end": v(180, 0) * mm, "construction": true});
            skLineSegment(sketch, "E154", {"start": v(180, 0) * mm, "end": v(189.25, 0) * mm, "construction": true});
            skLineSegment(sketch, "E155", {"start": v(189.25, 0) * mm, "end": v(189.25, 9.25) * mm, "construction": true});
            skLineSegment(sketch, "E156", {"start": v(189.25, 9.25) * mm, "end": v(201, 9.25) * mm, "construction": true});
            skLineSegment(sketch, "E157", {"start": v(189.25, 9.25) * mm, "end": v(189.25, 21) * mm, "construction": true});
            skLineSegment(sketch, "E158.bottom", {"start": v(199.5, 10.75) * mm, "end": v(202.5, 10.75) * mm});
            skLineSegment(sketch, "E158.top", {"start": v(199.5, 7.75) * mm, "end": v(202.5, 7.75) * mm});
            skLineSegment(sketch, "E158.left", {"start": v(199.5, 10.75) * mm, "end": v(199.5, 7.75) * mm});
            skLineSegment(sketch, "E158.right", {"start": v(202.5, 10.75) * mm, "end": v(202.5, 7.75) * mm});
            skPoint(sketch, "E158.middle", {"position": v(201, 9.25) * mm});
            skLineSegment(sketch, "E159.bottom", {"start": v(187.75, 22.5) * mm, "end": v(190.75, 22.5) * mm});
            skLineSegment(sketch, "E159.top", {"start": v(187.75, 19.5) * mm, "end": v(190.75, 19.5) * mm});
            skLineSegment(sketch, "E159.left", {"start": v(187.75, 22.5) * mm, "end": v(187.75, 19.5) * mm});
            skLineSegment(sketch, "E159.right", {"start": v(190.75, 22.5) * mm, "end": v(190.75, 19.5) * mm});
            skPoint(sketch, "E159.middle", {"position": v(189.25, 21) * mm});
            skLineSegment(sketch, "E160.bottom", {"start": v(180, 0) * mm, "end": v(269, 0) * mm});
            skLineSegment(sketch, "E160.top", {"start": v(180, 89) * mm, "end": v(269, 89) * mm});
            skLineSegment(sketch, "E160.left", {"start": v(180, 0) * mm, "end": v(180, 89) * mm});
            skLineSegment(sketch, "E160.right", {"start": v(269, 0) * mm, "end": v(269, 89) * mm});
            skPoint(sketch, "E161.0.1.0", {"position": v(201, 32.75) * mm});
            skPoint(sketch, "E161.0.1.1", {"position": v(189.25, 44.5) * mm});
            skLineSegment(sketch, "E161.0.1.2", {"start": v(187.75, 46) * mm, "end": v(190.75, 46) * mm});
            skLineSegment(sketch, "E161.0.1.3", {"start": v(199.5, 34.25) * mm, "end": v(202.5, 34.25) * mm});
            skLineSegment(sketch, "E161.0.1.4", {"start": v(202.5, 34.25) * mm, "end": v(202.5, 31.25) * mm});
            skLineSegment(sketch, "E161.0.1.5", {"start": v(199.5, 34.25) * mm, "end": v(199.5, 31.25) * mm});
            skLineSegment(sketch, "E161.0.1.6", {"start": v(199.5, 31.25) * mm, "end": v(202.5, 31.25) * mm});
            skLineSegment(sketch, "E161.0.1.7", {"start": v(187.75, 46) * mm, "end": v(187.75, 43) * mm});
            skLineSegment(sketch, "E161.0.1.8", {"start": v(190.75, 46) * mm, "end": v(190.75, 43) * mm});
            skLineSegment(sketch, "E161.0.1.9", {"start": v(187.75, 43) * mm, "end": v(190.75, 43) * mm});
            skPoint(sketch, "E161.0.2.0", {"position": v(201, 56.25) * mm});
            skPoint(sketch, "E161.0.2.1", {"position": v(189.25, 68) * mm});
            skLineSegment(sketch, "E161.0.2.2", {"start": v(187.75, 69.5) * mm, "end": v(190.75, 69.5) * mm});
            skLineSegment(sketch, "E161.0.2.3", {"start": v(199.5, 57.75) * mm, "end": v(202.5, 57.75) * mm});
            skLineSegment(sketch, "E161.0.2.4", {"start": v(202.5, 57.75) * mm, "end": v(202.5, 54.75) * mm});
            skLineSegment(sketch, "E161.0.2.5", {"start": v(199.5, 57.75) * mm, "end": v(199.5, 54.75) * mm});
            skLineSegment(sketch, "E161.0.2.6", {"start": v(199.5, 54.75) * mm, "end": v(202.5, 54.75) * mm});
            skLineSegment(sketch, "E161.0.2.7", {"start": v(187.75, 69.5) * mm, "end": v(187.75, 66.5) * mm});
            skLineSegment(sketch, "E161.0.2.8", {"start": v(190.75, 69.5) * mm, "end": v(190.75, 66.5) * mm});
            skLineSegment(sketch, "E161.0.2.9", {"start": v(187.75, 66.5) * mm, "end": v(190.75, 66.5) * mm});
            skPoint(sketch, "E161.0.3.0", {"position": v(201, 79.75) * mm});
            skPoint(sketch, "E161.0.3.1", {"position": v(189.25, 91.5) * mm});
            skLineSegment(sketch, "E161.0.3.2", {"start": v(187.75, 93) * mm, "end": v(190.75, 93) * mm});
            skLineSegment(sketch, "E161.0.3.3", {"start": v(199.5, 81.25) * mm, "end": v(202.5, 81.25) * mm});
            skLineSegment(sketch, "E161.0.3.4", {"start": v(202.5, 81.25) * mm, "end": v(202.5, 78.25) * mm});
            skLineSegment(sketch, "E161.0.3.5", {"start": v(199.5, 81.25) * mm, "end": v(199.5, 78.25) * mm});
            skLineSegment(sketch, "E161.0.3.6", {"start": v(199.5, 78.25) * mm, "end": v(202.5, 78.25) * mm});
            skLineSegment(sketch, "E161.0.3.7", {"start": v(187.75, 93) * mm, "end": v(187.75, 90) * mm});
            skLineSegment(sketch, "E161.0.3.8", {"start": v(190.75, 93) * mm, "end": v(190.75, 90) * mm});
            skLineSegment(sketch, "E161.0.3.9", {"start": v(187.75, 90) * mm, "end": v(190.75, 90) * mm});
            skPoint(sketch, "E161.0.4.0", {"position": v(201, 103.25) * mm});
            skPoint(sketch, "E161.0.4.1", {"position": v(189.25, 115) * mm});
            skLineSegment(sketch, "E161.0.4.2", {"start": v(187.75, 116.5) * mm, "end": v(190.75, 116.5) * mm});
            skLineSegment(sketch, "E161.0.4.3", {"start": v(199.5, 104.75) * mm, "end": v(202.5, 104.75) * mm});
            skLineSegment(sketch, "E161.0.4.4", {"start": v(202.5, 104.75) * mm, "end": v(202.5, 101.75) * mm});
            skLineSegment(sketch, "E161.0.4.5", {"start": v(199.5, 104.75) * mm, "end": v(199.5, 101.75) * mm});
            skLineSegment(sketch, "E161.0.4.6", {"start": v(199.5, 101.75) * mm, "end": v(202.5, 101.75) * mm});
            skLineSegment(sketch, "E161.0.4.7", {"start": v(187.75, 116.5) * mm, "end": v(187.75, 113.5) * mm});
            skLineSegment(sketch, "E161.0.4.8", {"start": v(190.75, 116.5) * mm, "end": v(190.75, 113.5) * mm});
            skLineSegment(sketch, "E161.0.4.9", {"start": v(187.75, 113.5) * mm, "end": v(190.75, 113.5) * mm});
            skPoint(sketch, "E161.1.0.0", {"position": v(224.5, 9.25) * mm});
            skPoint(sketch, "E161.1.0.1", {"position": v(212.75, 21) * mm});
            skLineSegment(sketch, "E161.1.0.2", {"start": v(211.25, 22.5) * mm, "end": v(214.25, 22.5) * mm});
            skLineSegment(sketch, "E161.1.0.3", {"start": v(223, 10.75) * mm, "end": v(226, 10.75) * mm});
            skLineSegment(sketch, "E161.1.0.4", {"start": v(226, 10.75) * mm, "end": v(226, 7.75) * mm});
            skLineSegment(sketch, "E161.1.0.5", {"start": v(223, 10.75) * mm, "end": v(223, 7.75) * mm});
            skLineSegment(sketch, "E161.1.0.6", {"start": v(223, 7.75) * mm, "end": v(226, 7.75) * mm});
            skLineSegment(sketch, "E161.1.0.7", {"start": v(211.25, 22.5) * mm, "end": v(211.25, 19.5) * mm});
            skLineSegment(sketch, "E161.1.0.8", {"start": v(214.25, 22.5) * mm, "end": v(214.25, 19.5) * mm});
            skLineSegment(sketch, "E161.1.0.9", {"start": v(211.25, 19.5) * mm, "end": v(214.25, 19.5) * mm});
            skPoint(sketch, "E161.1.1.0", {"position": v(224.5, 32.75) * mm});
            skPoint(sketch, "E161.1.1.1", {"position": v(212.75, 44.5) * mm});
            skLineSegment(sketch, "E161.1.1.2", {"start": v(211.25, 46) * mm, "end": v(214.25, 46) * mm});
            skLineSegment(sketch, "E161.1.1.3", {"start": v(223, 34.25) * mm, "end": v(226, 34.25) * mm});
            skLineSegment(sketch, "E161.1.1.4", {"start": v(226, 34.25) * mm, "end": v(226, 31.25) * mm});
            skLineSegment(sketch, "E161.1.1.5", {"start": v(223, 34.25) * mm, "end": v(223, 31.25) * mm});
            skLineSegment(sketch, "E161.1.1.6", {"start": v(223, 31.25) * mm, "end": v(226, 31.25) * mm});
            skLineSegment(sketch, "E161.1.1.7", {"start": v(211.25, 46) * mm, "end": v(211.25, 43) * mm});
            skLineSegment(sketch, "E161.1.1.8", {"start": v(214.25, 46) * mm, "end": v(214.25, 43) * mm});
            skLineSegment(sketch, "E161.1.1.9", {"start": v(211.25, 43) * mm, "end": v(214.25, 43) * mm});
            skPoint(sketch, "E161.1.2.0", {"position": v(224.5, 56.25) * mm});
            skPoint(sketch, "E161.1.2.1", {"position": v(212.75, 68) * mm});
            skLineSegment(sketch, "E161.1.2.2", {"start": v(211.25, 69.5) * mm, "end": v(214.25, 69.5) * mm});
            skLineSegment(sketch, "E161.1.2.3", {"start": v(223, 57.75) * mm, "end": v(226, 57.75) * mm});
            skLineSegment(sketch, "E161.1.2.4", {"start": v(226, 57.75) * mm, "end": v(226, 54.75) * mm});
            skLineSegment(sketch, "E161.1.2.5", {"start": v(223, 57.75) * mm, "end": v(223, 54.75) * mm});
            skLineSegment(sketch, "E161.1.2.6", {"start": v(223, 54.75) * mm, "end": v(226, 54.75) * mm});
            skLineSegment(sketch, "E161.1.2.7", {"start": v(211.25, 69.5) * mm, "end": v(211.25, 66.5) * mm});
            skLineSegment(sketch, "E161.1.2.8", {"start": v(214.25, 69.5) * mm, "end": v(214.25, 66.5) * mm});
            skLineSegment(sketch, "E161.1.2.9", {"start": v(211.25, 66.5) * mm, "end": v(214.25, 66.5) * mm});
            skPoint(sketch, "E161.1.3.0", {"position": v(224.5, 79.75) * mm});
            skPoint(sketch, "E161.1.3.1", {"position": v(212.75, 91.5) * mm});
            skLineSegment(sketch, "E161.1.3.2", {"start": v(211.25, 93) * mm, "end": v(214.25, 93) * mm});
            skLineSegment(sketch, "E161.1.3.3", {"start": v(223, 81.25) * mm, "end": v(226, 81.25) * mm});
            skLineSegment(sketch, "E161.1.3.4", {"start": v(226, 81.25) * mm, "end": v(226, 78.25) * mm});
            skLineSegment(sketch, "E161.1.3.5", {"start": v(223, 81.25) * mm, "end": v(223, 78.25) * mm});
            skLineSegment(sketch, "E161.1.3.6", {"start": v(223, 78.25) * mm, "end": v(226, 78.25) * mm});
            skLineSegment(sketch, "E161.1.3.7", {"start": v(211.25, 93) * mm, "end": v(211.25, 90) * mm});
            skLineSegment(sketch, "E161.1.3.8", {"start": v(214.25, 93) * mm, "end": v(214.25, 90) * mm});
            skLineSegment(sketch, "E161.1.3.9", {"start": v(211.25, 90) * mm, "end": v(214.25, 90) * mm});
            skPoint(sketch, "E161.1.4.0", {"position": v(224.5, 103.25) * mm});
            skPoint(sketch, "E161.1.4.1", {"position": v(212.75, 115) * mm});
            skLineSegment(sketch, "E161.1.4.2", {"start": v(211.25, 116.5) * mm, "end": v(214.25, 116.5) * mm});
            skLineSegment(sketch, "E161.1.4.3", {"start": v(223, 104.75) * mm, "end": v(226, 104.75) * mm});
            skLineSegment(sketch, "E161.1.4.4", {"start": v(226, 104.75) * mm, "end": v(226, 101.75) * mm});
            skLineSegment(sketch, "E161.1.4.5", {"start": v(223, 104.75) * mm, "end": v(223, 101.75) * mm});
            skLineSegment(sketch, "E161.1.4.6", {"start": v(223, 101.75) * mm, "end": v(226, 101.75) * mm});
            skLineSegment(sketch, "E161.1.4.7", {"start": v(211.25, 116.5) * mm, "end": v(211.25, 113.5) * mm});
            skLineSegment(sketch, "E161.1.4.8", {"start": v(214.25, 116.5) * mm, "end": v(214.25, 113.5) * mm});
            skLineSegment(sketch, "E161.1.4.9", {"start": v(211.25, 113.5) * mm, "end": v(214.25, 113.5) * mm});
            skPoint(sketch, "E161.2.0.0", {"position": v(248, 9.25) * mm});
            skPoint(sketch, "E161.2.0.1", {"position": v(236.25, 21) * mm});
            skLineSegment(sketch, "E161.2.0.2", {"start": v(234.75, 22.5) * mm, "end": v(237.75, 22.5) * mm});
            skLineSegment(sketch, "E161.2.0.3", {"start": v(246.5, 10.75) * mm, "end": v(249.5, 10.75) * mm});
            skLineSegment(sketch, "E161.2.0.4", {"start": v(249.5, 10.75) * mm, "end": v(249.5, 7.75) * mm});
            skLineSegment(sketch, "E161.2.0.5", {"start": v(246.5, 10.75) * mm, "end": v(246.5, 7.75) * mm});
            skLineSegment(sketch, "E161.2.0.6", {"start": v(246.5, 7.75) * mm, "end": v(249.5, 7.75) * mm});
            skLineSegment(sketch, "E161.2.0.7", {"start": v(234.75, 22.5) * mm, "end": v(234.75, 19.5) * mm});
            skLineSegment(sketch, "E161.2.0.8", {"start": v(237.75, 22.5) * mm, "end": v(237.75, 19.5) * mm});
            skLineSegment(sketch, "E161.2.0.9", {"start": v(234.75, 19.5) * mm, "end": v(237.75, 19.5) * mm});
            skPoint(sketch, "E161.2.1.0", {"position": v(248, 32.75) * mm});
            skPoint(sketch, "E161.2.1.1", {"position": v(236.25, 44.5) * mm});
            skLineSegment(sketch, "E161.2.1.2", {"start": v(234.75, 46) * mm, "end": v(237.75, 46) * mm});
            skLineSegment(sketch, "E161.2.1.3", {"start": v(246.5, 34.25) * mm, "end": v(249.5, 34.25) * mm});
            skLineSegment(sketch, "E161.2.1.4", {"start": v(249.5, 34.25) * mm, "end": v(249.5, 31.25) * mm});
            skLineSegment(sketch, "E161.2.1.5", {"start": v(246.5, 34.25) * mm, "end": v(246.5, 31.25) * mm});
            skLineSegment(sketch, "E161.2.1.6", {"start": v(246.5, 31.25) * mm, "end": v(249.5, 31.25) * mm});
            skLineSegment(sketch, "E161.2.1.7", {"start": v(234.75, 46) * mm, "end": v(234.75, 43) * mm});
            skLineSegment(sketch, "E161.2.1.8", {"start": v(237.75, 46) * mm, "end": v(237.75, 43) * mm});
            skLineSegment(sketch, "E161.2.1.9", {"start": v(234.75, 43) * mm, "end": v(237.75, 43) * mm});
            skPoint(sketch, "E161.2.2.0", {"position": v(248, 56.25) * mm});
            skPoint(sketch, "E161.2.2.1", {"position": v(236.25, 68) * mm});
            skLineSegment(sketch, "E161.2.2.2", {"start": v(234.75, 69.5) * mm, "end": v(237.75, 69.5) * mm});
            skLineSegment(sketch, "E161.2.2.3", {"start": v(246.5, 57.75) * mm, "end": v(249.5, 57.75) * mm});
            skLineSegment(sketch, "E161.2.2.4", {"start": v(249.5, 57.75) * mm, "end": v(249.5, 54.75) * mm});
            skLineSegment(sketch, "E161.2.2.5", {"start": v(246.5, 57.75) * mm, "end": v(246.5, 54.75) * mm});
            skLineSegment(sketch, "E161.2.2.6", {"start": v(246.5, 54.75) * mm, "end": v(249.5, 54.75) * mm});
            skLineSegment(sketch, "E161.2.2.7", {"start": v(234.75, 69.5) * mm, "end": v(234.75, 66.5) * mm});
            skLineSegment(sketch, "E161.2.2.8", {"start": v(237.75, 69.5) * mm, "end": v(237.75, 66.5) * mm});
            skLineSegment(sketch, "E161.2.2.9", {"start": v(234.75, 66.5) * mm, "end": v(237.75, 66.5) * mm});
            skPoint(sketch, "E161.2.3.0", {"position": v(248, 79.75) * mm});
            skPoint(sketch, "E161.2.3.1", {"position": v(236.25, 91.5) * mm});
            skLineSegment(sketch, "E161.2.3.2", {"start": v(234.75, 93) * mm, "end": v(237.75, 93) * mm});
            skLineSegment(sketch, "E161.2.3.3", {"start": v(246.5, 81.25) * mm, "end": v(249.5, 81.25) * mm});
            skLineSegment(sketch, "E161.2.3.4", {"start": v(249.5, 81.25) * mm, "end": v(249.5, 78.25) * mm});
            skLineSegment(sketch, "E161.2.3.5", {"start": v(246.5, 81.25) * mm, "end": v(246.5, 78.25) * mm});
            skLineSegment(sketch, "E161.2.3.6", {"start": v(246.5, 78.25) * mm, "end": v(249.5, 78.25) * mm});
            skLineSegment(sketch, "E161.2.3.7", {"start": v(234.75, 93) * mm, "end": v(234.75, 90) * mm});
            skLineSegment(sketch, "E161.2.3.8", {"start": v(237.75, 93) * mm, "end": v(237.75, 90) * mm});
            skLineSegment(sketch, "E161.2.3.9", {"start": v(234.75, 90) * mm, "end": v(237.75, 90) * mm});
            skPoint(sketch, "E161.2.4.0", {"position": v(248, 103.25) * mm});
            skPoint(sketch, "E161.2.4.1", {"position": v(236.25, 115) * mm});
            skLineSegment(sketch, "E161.2.4.2", {"start": v(234.75, 116.5) * mm, "end": v(237.75, 116.5) * mm});
            skLineSegment(sketch, "E161.2.4.3", {"start": v(246.5, 104.75) * mm, "end": v(249.5, 104.75) * mm});
            skLineSegment(sketch, "E161.2.4.4", {"start": v(249.5, 104.75) * mm, "end": v(249.5, 101.75) * mm});
            skLineSegment(sketch, "E161.2.4.5", {"start": v(246.5, 104.75) * mm, "end": v(246.5, 101.75) * mm});
            skLineSegment(sketch, "E161.2.4.6", {"start": v(246.5, 101.75) * mm, "end": v(249.5, 101.75) * mm});
            skLineSegment(sketch, "E161.2.4.7", {"start": v(234.75, 116.5) * mm, "end": v(234.75, 113.5) * mm});
            skLineSegment(sketch, "E161.2.4.8", {"start": v(237.75, 116.5) * mm, "end": v(237.75, 113.5) * mm});
            skLineSegment(sketch, "E161.2.4.9", {"start": v(234.75, 113.5) * mm, "end": v(237.75, 113.5) * mm});
            skLineSegment(sketch, "E161.direction1", {"start": v(199.5, 7.75) * mm, "end": v(223, 7.75) * mm, "construction": true});
            skLineSegment(sketch, "E161.direction2", {"start": v(199.5, 7.75) * mm, "end": v(199.5, 31.25) * mm, "construction": true});
            skPoint(sketch, "E162.0.3.0", {"position": v(271.5, 9.25) * mm});
            skPoint(sketch, "E162.1.3.0", {"position": v(259.75, 21) * mm});
            skLineSegment(sketch, "E162.2.3.0", {"start": v(258.25, 22.5) * mm, "end": v(261.25, 22.5) * mm});
            skLineSegment(sketch, "E162.5.3.0", {"start": v(270, 10.75) * mm, "end": v(273, 10.75) * mm});
            skLineSegment(sketch, "E162.8.3.0", {"start": v(273, 10.75) * mm, "end": v(273, 7.75) * mm});
            skLineSegment(sketch, "E162.11.3.0", {"start": v(270, 10.75) * mm, "end": v(270, 7.75) * mm});
            skLineSegment(sketch, "E162.14.3.0", {"start": v(270, 7.75) * mm, "end": v(273, 7.75) * mm});
            skLineSegment(sketch, "E162.17.3.0", {"start": v(258.25, 22.5) * mm, "end": v(258.25, 19.5) * mm});
            skLineSegment(sketch, "E162.20.3.0", {"start": v(261.25, 22.5) * mm, "end": v(261.25, 19.5) * mm});
            skLineSegment(sketch, "E162.23.3.0", {"start": v(258.25, 19.5) * mm, "end": v(261.25, 19.5) * mm});
            skPoint(sketch, "E162.0.3.1", {"position": v(271.5, 32.75) * mm});
            skPoint(sketch, "E162.1.3.1", {"position": v(259.75, 44.5) * mm});
            skLineSegment(sketch, "E162.2.3.1", {"start": v(258.25, 46) * mm, "end": v(261.25, 46) * mm});
            skLineSegment(sketch, "E162.5.3.1", {"start": v(270, 34.25) * mm, "end": v(273, 34.25) * mm});
            skLineSegment(sketch, "E162.8.3.1", {"start": v(273, 34.25) * mm, "end": v(273, 31.25) * mm});
            skLineSegment(sketch, "E162.11.3.1", {"start": v(270, 34.25) * mm, "end": v(270, 31.25) * mm});
            skLineSegment(sketch, "E162.14.3.1", {"start": v(270, 31.25) * mm, "end": v(273, 31.25) * mm});
            skLineSegment(sketch, "E162.17.3.1", {"start": v(258.25, 46) * mm, "end": v(258.25, 43) * mm});
            skLineSegment(sketch, "E162.20.3.1", {"start": v(261.25, 46) * mm, "end": v(261.25, 43) * mm});
            skLineSegment(sketch, "E162.23.3.1", {"start": v(258.25, 43) * mm, "end": v(261.25, 43) * mm});
            skPoint(sketch, "E162.0.3.2", {"position": v(271.5, 56.25) * mm});
            skPoint(sketch, "E162.1.3.2", {"position": v(259.75, 68) * mm});
            skLineSegment(sketch, "E162.2.3.2", {"start": v(258.25, 69.5) * mm, "end": v(261.25, 69.5) * mm});
            skLineSegment(sketch, "E162.5.3.2", {"start": v(270, 57.75) * mm, "end": v(273, 57.75) * mm});
            skLineSegment(sketch, "E162.8.3.2", {"start": v(273, 57.75) * mm, "end": v(273, 54.75) * mm});
            skLineSegment(sketch, "E162.11.3.2", {"start": v(270, 57.75) * mm, "end": v(270, 54.75) * mm});
            skLineSegment(sketch, "E162.14.3.2", {"start": v(270, 54.75) * mm, "end": v(273, 54.75) * mm});
            skLineSegment(sketch, "E162.17.3.2", {"start": v(258.25, 69.5) * mm, "end": v(258.25, 66.5) * mm});
            skLineSegment(sketch, "E162.20.3.2", {"start": v(261.25, 69.5) * mm, "end": v(261.25, 66.5) * mm});
            skLineSegment(sketch, "E162.23.3.2", {"start": v(258.25, 66.5) * mm, "end": v(261.25, 66.5) * mm});
            skPoint(sketch, "E162.0.3.3", {"position": v(271.5, 79.75) * mm});
            skPoint(sketch, "E162.1.3.3", {"position": v(259.75, 91.5) * mm});
            skLineSegment(sketch, "E162.2.3.3", {"start": v(258.25, 93) * mm, "end": v(261.25, 93) * mm});
            skLineSegment(sketch, "E162.5.3.3", {"start": v(270, 81.25) * mm, "end": v(273, 81.25) * mm});
            skLineSegment(sketch, "E162.8.3.3", {"start": v(273, 81.25) * mm, "end": v(273, 78.25) * mm});
            skLineSegment(sketch, "E162.11.3.3", {"start": v(270, 81.25) * mm, "end": v(270, 78.25) * mm});
            skLineSegment(sketch, "E162.14.3.3", {"start": v(270, 78.25) * mm, "end": v(273, 78.25) * mm});
            skLineSegment(sketch, "E162.17.3.3", {"start": v(258.25, 93) * mm, "end": v(258.25, 90) * mm});
            skLineSegment(sketch, "E162.20.3.3", {"start": v(261.25, 93) * mm, "end": v(261.25, 90) * mm});
            skLineSegment(sketch, "E162.23.3.3", {"start": v(258.25, 90) * mm, "end": v(261.25, 90) * mm});
            skPoint(sketch, "E162.0.3.4", {"position": v(271.5, 103.25) * mm});
            skPoint(sketch, "E162.1.3.4", {"position": v(259.75, 115) * mm});
            skLineSegment(sketch, "E162.2.3.4", {"start": v(258.25, 116.5) * mm, "end": v(261.25, 116.5) * mm});
            skLineSegment(sketch, "E162.5.3.4", {"start": v(270, 104.75) * mm, "end": v(273, 104.75) * mm});
            skLineSegment(sketch, "E162.8.3.4", {"start": v(273, 104.75) * mm, "end": v(273, 101.75) * mm});
            skLineSegment(sketch, "E162.11.3.4", {"start": v(270, 104.75) * mm, "end": v(270, 101.75) * mm});
            skLineSegment(sketch, "E162.14.3.4", {"start": v(270, 101.75) * mm, "end": v(273, 101.75) * mm});
            skLineSegment(sketch, "E162.17.3.4", {"start": v(258.25, 116.5) * mm, "end": v(258.25, 113.5) * mm});
            skLineSegment(sketch, "E162.20.3.4", {"start": v(261.25, 116.5) * mm, "end": v(261.25, 113.5) * mm});
            skLineSegment(sketch, "E162.23.3.4", {"start": v(258.25, 113.5) * mm, "end": v(261.25, 113.5) * mm});
            skSolve(sketch);
        }
        {
            var Q0;
            Q0=qSketchRegion(id+"F27",true);
            extrude(context, id + "F28", {"entities" : qUnion([Q0]), "operationType" : NewBodyOperationType.REMOVE, "depth" : 25 * mm});
        }
        {
            var Q0;
            Q0=qCreatedBy(makeId("Top.planeOp"),FACE);
            var sketch = newSketch(context, id + "F29", { "sketchPlane" : qUnion([Q0])});
            skLineSegment(sketch, "E163", {"start": v(0, 0) * mm, "end": v(180, 0) * mm, "construction": true});
            skLineSegment(sketch, "E164", {"start": v(180, 0) * mm, "end": v(189.25, 0) * mm, "construction": true});
            skLineSegment(sketch, "E165", {"start": v(189.25, 0) * mm, "end": v(189.25, 9.25) * mm, "construction": true});
            skLineSegment(sketch, "E166", {"start": v(189.25, 9.25) * mm, "end": v(201, 9.25) * mm, "construction": true});
            skLineSegment(sketch, "E167", {"start": v(201, 9.25) * mm, "end": v(201, 21) * mm, "construction": true});
            skLineSegment(sketch, "E168", {"start": v(201, 21) * mm, "end": v(189.25, 21) * mm, "construction": true});
            skCircle(sketch, "E169", {"center": v(201, 9.25) * mm, "radius": 1.05 * mm});
            skCircle(sketch, "E170", {"center": v(189.25, 21) * mm, "radius": 1.05 * mm});
            skCircle(sketch, "E171.0.1.0", {"center": v(201, 32.75) * mm, "radius": 1.05 * mm});
            skCircle(sketch, "E171.0.1.1", {"center": v(189.25, 44.5) * mm, "radius": 1.05 * mm});
            skCircle(sketch, "E171.0.2.0", {"center": v(201, 56.25) * mm, "radius": 1.05 * mm});
            skCircle(sketch, "E171.0.2.1", {"center": v(189.25, 68) * mm, "radius": 1.05 * mm});
            skCircle(sketch, "E171.0.3.0", {"center": v(201, 79.75) * mm, "radius": 1.05 * mm});
            skCircle(sketch, "E171.0.3.1", {"center": v(189.25, 91.5) * mm, "radius": 1.05 * mm});
            skCircle(sketch, "E171.0.4.0", {"center": v(201, 103.25) * mm, "radius": 1.05 * mm});
            skCircle(sketch, "E171.0.4.1", {"center": v(189.25, 115) * mm, "radius": 1.05 * mm});
            skCircle(sketch, "E171.1.0.0", {"center": v(224.5, 9.25) * mm, "radius": 1.05 * mm});
            skCircle(sketch, "E171.1.0.1", {"center": v(212.75, 21) * mm, "radius": 1.05 * mm});
            skCircle(sketch, "E171.1.1.0", {"center": v(224.5, 32.75) * mm, "radius": 1.05 * mm});
            skCircle(sketch, "E171.1.1.1", {"center": v(212.75, 44.5) * mm, "radius": 1.05 * mm});
            skCircle(sketch, "E171.1.2.0", {"center": v(224.5, 56.25) * mm, "radius": 1.05 * mm});
            skCircle(sketch, "E171.1.2.1", {"center": v(212.75, 68) * mm, "radius": 1.05 * mm});
            skCircle(sketch, "E171.1.3.0", {"center": v(224.5, 79.75) * mm, "radius": 1.05 * mm});
            skCircle(sketch, "E171.1.3.1", {"center": v(212.75, 91.5) * mm, "radius": 1.05 * mm});
            skCircle(sketch, "E171.1.4.0", {"center": v(224.5, 103.25) * mm, "radius": 1.05 * mm});
            skCircle(sketch, "E171.1.4.1", {"center": v(212.75, 115) * mm, "radius": 1.05 * mm});
            skCircle(sketch, "E171.2.0.0", {"center": v(248, 9.25) * mm, "radius": 1.05 * mm});
            skCircle(sketch, "E171.2.0.1", {"center": v(236.25, 21) * mm, "radius": 1.05 * mm});
            skCircle(sketch, "E171.2.1.0", {"center": v(248, 32.75) * mm, "radius": 1.05 * mm});
            skCircle(sketch, "E171.2.1.1", {"center": v(236.25, 44.5) * mm, "radius": 1.05 * mm});
            skCircle(sketch, "E171.2.2.0", {"center": v(248, 56.25) * mm, "radius": 1.05 * mm});
            skCircle(sketch, "E171.2.2.1", {"center": v(236.25, 68) * mm, "radius": 1.05 * mm});
            skCircle(sketch, "E171.2.3.0", {"center": v(248, 79.75) * mm, "radius": 1.05 * mm});
            skCircle(sketch, "E171.2.3.1", {"center": v(236.25, 91.5) * mm, "radius": 1.05 * mm});
            skCircle(sketch, "E171.2.4.0", {"center": v(248, 103.25) * mm, "radius": 1.05 * mm});
            skCircle(sketch, "E171.2.4.1", {"center": v(236.25, 115) * mm, "radius": 1.05 * mm});
            skCircle(sketch, "E171.3.0.0", {"center": v(271.5, 9.25) * mm, "radius": 1.05 * mm});
            skCircle(sketch, "E171.3.0.1", {"center": v(259.75, 21) * mm, "radius": 1.05 * mm});
            skCircle(sketch, "E171.3.1.0", {"center": v(271.5, 32.75) * mm, "radius": 1.05 * mm});
            skCircle(sketch, "E171.3.1.1", {"center": v(259.75, 44.5) * mm, "radius": 1.05 * mm});
            skCircle(sketch, "E171.3.2.0", {"center": v(271.5, 56.25) * mm, "radius": 1.05 * mm});
            skCircle(sketch, "E171.3.2.1", {"center": v(259.75, 68) * mm, "radius": 1.05 * mm});
            skCircle(sketch, "E171.3.3.0", {"center": v(271.5, 79.75) * mm, "radius": 1.05 * mm});
            skCircle(sketch, "E171.3.3.1", {"center": v(259.75, 91.5) * mm, "radius": 1.05 * mm});
            skCircle(sketch, "E171.3.4.0", {"center": v(271.5, 103.25) * mm, "radius": 1.05 * mm});
            skCircle(sketch, "E171.3.4.1", {"center": v(259.75, 115) * mm, "radius": 1.05 * mm});
            skCircle(sketch, "E171.4.0.0", {"center": v(295, 9.25) * mm, "radius": 1.05 * mm});
            skCircle(sketch, "E171.4.0.1", {"center": v(283.25, 21) * mm, "radius": 1.05 * mm});
            skCircle(sketch, "E171.4.1.0", {"center": v(295, 32.75) * mm, "radius": 1.05 * mm});
            skCircle(sketch, "E171.4.1.1", {"center": v(283.25, 44.5) * mm, "radius": 1.05 * mm});
            skCircle(sketch, "E171.4.2.0", {"center": v(295, 56.25) * mm, "radius": 1.05 * mm});
            skCircle(sketch, "E171.4.2.1", {"center": v(283.25, 68) * mm, "radius": 1.05 * mm});
            skCircle(sketch, "E171.4.3.0", {"center": v(295, 79.75) * mm, "radius": 1.05 * mm});
            skCircle(sketch, "E171.4.3.1", {"center": v(283.25, 91.5) * mm, "radius": 1.05 * mm});
            skCircle(sketch, "E171.4.4.0", {"center": v(295, 103.25) * mm, "radius": 1.05 * mm});
            skCircle(sketch, "E171.4.4.1", {"center": v(283.25, 115) * mm, "radius": 1.05 * mm});
            skLineSegment(sketch, "E171.direction1", {"start": v(201, 9.25) * mm, "end": v(224.5, 9.25) * mm, "construction": true});
            skLineSegment(sketch, "E171.direction2", {"start": v(201, 9.25) * mm, "end": v(201, 32.75) * mm, "construction": true});
            skSolve(sketch);
        }
        {
            var Q0;
            Q0=qSketchRegion(id+"F29",true);
            extrude(context, id + "F30", {"entities" : qUnion([Q0]), "operationType" : NewBodyOperationType.REMOVE, "endBound" : BoundingType.THROUGH_ALL, "depth" : 25 * mm, "hasSecondDirection" : true, "secondDirectionBound" : SecondDirectionBoundingType.THROUGH_ALL, "secondDirectionOppositeDirection" : true, "secondDirectionDepth" : 25 * mm});
        }
        {
            var Q0;
            Q0=qCreatedBy(makeId("Top.planeOp"),FACE);
            var sketch = newSketch(context, id + "F31", { "sketchPlane" : qUnion([Q0])});
            skLineSegment(sketch, "E172", {"start": v(0, 0) * mm, "end": v(180, 0) * mm, "construction": true});
            skLineSegment(sketch, "E173", {"start": v(180, 0) * mm, "end": v(189.3, 0) * mm, "construction": true});
            skLineSegment(sketch, "E174", {"start": v(189.3, 0) * mm, "end": v(189.3, 9.3) * mm, "construction": true});
            skLineSegment(sketch, "E175.bottom", {"start": v(189.3, 9.3) * mm, "end": v(233, 9.3) * mm, "construction": true});
            skLineSegment(sketch, "E175.top", {"start": v(189.3, 53) * mm, "end": v(233, 53) * mm, "construction": true});
            skLineSegment(sketch, "E175.left", {"start": v(189.3, 9.3) * mm, "end": v(189.3, 53) * mm, "construction": true});
            skLineSegment(sketch, "E175.right", {"start": v(233, 9.3) * mm, "end": v(233, 53) * mm, "construction": true});
            skCircle(sketch, "E176", {"center": v(189.3, 9.3) * mm, "radius": 1.05 * mm});
            skCircle(sketch, "E177", {"center": v(233, 9.3) * mm, "radius": 1.05 * mm});
            skCircle(sketch, "E178", {"center": v(233, 53) * mm, "radius": 1.05 * mm});
            skCircle(sketch, "E179", {"center": v(189.3, 53) * mm, "radius": 1.05 * mm});
            skLineSegment(sketch, "E180", {"start": v(233, 53) * mm, "end": v(256.5, 53) * mm, "construction": true});
            skLineSegment(sketch, "E181", {"start": v(233, 9.3) * mm, "end": v(256.5, 9.3) * mm, "construction": true});
            skCircle(sketch, "E182", {"center": v(256.5, 53) * mm, "radius": 1.05 * mm});
            skCircle(sketch, "E183", {"center": v(256.5, 9.3) * mm, "radius": 1.05 * mm});
            skSolve(sketch);
        }
        {
            var Q0;
            Q0=qSketchRegion(id+"F31",true);
            extrude(context, id + "F32", {"entities" : qUnion([Q0]), "operationType" : NewBodyOperationType.REMOVE, "endBound" : BoundingType.THROUGH_ALL, "oppositeDirection" : true, "depth" : 25 * mm});
        }
        {
            var Q0;
            Q0=qCreatedBy(makeId("Top.planeOp"),FACE);
            var sketch = newSketch(context, id + "F33", { "sketchPlane" : qUnion([Q0])});
            skLineSegment(sketch, "E184", {"start": v(0, 0) * mm, "end": v(180, 0) * mm, "construction": true});
            skLineSegment(sketch, "E185", {"start": v(180, 0) * mm, "end": v(201, 0) * mm, "construction": true});
            skLineSegment(sketch, "E186", {"start": v(201, 0) * mm, "end": v(201, 21) * mm, "construction": true});
            skLineSegment(sketch, "E187", {"start": v(201, 21) * mm, "end": v(201, 31.25) * mm, "construction": true});
            skCircle(sketch, "E188.cCircle", {"center": v(201, 21) * mm, "radius": 10.25 * mm, "construction": true});
            skLineSegment(sketch, "E188.0", {"start": v(196.75, 31.25) * mm, "end": v(205.25, 31.25) * mm});
            skLineSegment(sketch, "E188.1", {"start": v(205.25, 31.25) * mm, "end": v(211.25, 25.25) * mm});
            skLineSegment(sketch, "E188.2", {"start": v(211.25, 25.25) * mm, "end": v(211.25, 16.75) * mm});
            skLineSegment(sketch, "E188.3", {"start": v(211.25, 16.75) * mm, "end": v(205.25, 10.75) * mm});
            skLineSegment(sketch, "E188.4", {"start": v(205.25, 10.75) * mm, "end": v(196.75, 10.75) * mm});
            skLineSegment(sketch, "E188.5", {"start": v(196.75, 10.75) * mm, "end": v(190.75, 16.75) * mm});
            skLineSegment(sketch, "E188.6", {"start": v(190.75, 16.75) * mm, "end": v(190.75, 25.25) * mm});
            skLineSegment(sketch, "E188.7", {"start": v(190.75, 25.25) * mm, "end": v(196.75, 31.25) * mm});
            skPoint(sketch, "E188.0.midPoint", {"position": v(201, 31.25) * mm});
            skCircle(sketch, "E189.0.1.0", {"center": v(201, 44.5) * mm, "radius": 10.25 * mm, "construction": true});
            skLineSegment(sketch, "E189.0.1.1", {"start": v(190.75, 40.25) * mm, "end": v(190.75, 48.75) * mm});
            skLineSegment(sketch, "E189.0.1.2", {"start": v(196.75, 54.75) * mm, "end": v(205.25, 54.75) * mm});
            skLineSegment(sketch, "E189.0.1.3", {"start": v(190.75, 48.75) * mm, "end": v(196.75, 54.75) * mm});
            skPoint(sketch, "E189.0.1.4", {"position": v(201, 54.75) * mm});
            skLineSegment(sketch, "E189.0.1.5", {"start": v(196.75, 34.25) * mm, "end": v(190.75, 40.25) * mm});
            skLineSegment(sketch, "E189.0.1.6", {"start": v(205.25, 34.25) * mm, "end": v(196.75, 34.25) * mm});
            skLineSegment(sketch, "E189.0.1.7", {"start": v(211.25, 40.25) * mm, "end": v(205.25, 34.25) * mm});
            skLineSegment(sketch, "E189.0.1.8", {"start": v(205.25, 54.75) * mm, "end": v(211.25, 48.75) * mm});
            skLineSegment(sketch, "E189.0.1.9", {"start": v(211.25, 48.75) * mm, "end": v(211.25, 40.25) * mm});
            skCircle(sketch, "E189.0.2.0", {"center": v(201, 68) * mm, "radius": 10.25 * mm, "construction": true});
            skLineSegment(sketch, "E189.0.2.1", {"start": v(190.75, 63.75) * mm, "end": v(190.75, 72.25) * mm});
            skLineSegment(sketch, "E189.0.2.2", {"start": v(196.75, 78.25) * mm, "end": v(205.25, 78.25) * mm});
            skLineSegment(sketch, "E189.0.2.3", {"start": v(190.75, 72.25) * mm, "end": v(196.75, 78.25) * mm});
            skPoint(sketch, "E189.0.2.4", {"position": v(201, 78.25) * mm});
            skLineSegment(sketch, "E189.0.2.5", {"start": v(196.75, 57.75) * mm, "end": v(190.75, 63.75) * mm});
            skLineSegment(sketch, "E189.0.2.6", {"start": v(205.25, 57.75) * mm, "end": v(196.75, 57.75) * mm});
            skLineSegment(sketch, "E189.0.2.7", {"start": v(211.25, 63.75) * mm, "end": v(205.25, 57.75) * mm});
            skLineSegment(sketch, "E189.0.2.8", {"start": v(205.25, 78.25) * mm, "end": v(211.25, 72.25) * mm});
            skLineSegment(sketch, "E189.0.2.9", {"start": v(211.25, 72.25) * mm, "end": v(211.25, 63.75) * mm});
            skCircle(sketch, "E189.1.0.0", {"center": v(224.5, 21) * mm, "radius": 10.25 * mm, "construction": true});
            skLineSegment(sketch, "E189.1.0.1", {"start": v(214.25, 16.75) * mm, "end": v(214.25, 25.25) * mm});
            skLineSegment(sketch, "E189.1.0.2", {"start": v(220.25, 31.25) * mm, "end": v(228.75, 31.25) * mm});
            skLineSegment(sketch, "E189.1.0.3", {"start": v(214.25, 25.25) * mm, "end": v(220.25, 31.25) * mm});
            skPoint(sketch, "E189.1.0.4", {"position": v(224.5, 31.25) * mm});
            skLineSegment(sketch, "E189.1.0.5", {"start": v(220.25, 10.75) * mm, "end": v(214.25, 16.75) * mm});
            skLineSegment(sketch, "E189.1.0.6", {"start": v(228.75, 10.75) * mm, "end": v(220.25, 10.75) * mm});
            skLineSegment(sketch, "E189.1.0.7", {"start": v(234.75, 16.75) * mm, "end": v(228.75, 10.75) * mm});
            skLineSegment(sketch, "E189.1.0.8", {"start": v(228.75, 31.25) * mm, "end": v(234.75, 25.25) * mm});
            skLineSegment(sketch, "E189.1.0.9", {"start": v(234.75, 25.25) * mm, "end": v(234.75, 16.75) * mm});
            skCircle(sketch, "E189.1.1.0", {"center": v(224.5, 44.5) * mm, "radius": 10.25 * mm, "construction": true});
            skLineSegment(sketch, "E189.1.1.1", {"start": v(214.25, 40.25) * mm, "end": v(214.25, 48.75) * mm});
            skLineSegment(sketch, "E189.1.1.2", {"start": v(220.25, 54.75) * mm, "end": v(228.75, 54.75) * mm});
            skLineSegment(sketch, "E189.1.1.3", {"start": v(214.25, 48.75) * mm, "end": v(220.25, 54.75) * mm});
            skPoint(sketch, "E189.1.1.4", {"position": v(224.5, 54.75) * mm});
            skLineSegment(sketch, "E189.1.1.5", {"start": v(220.25, 34.25) * mm, "end": v(214.25, 40.25) * mm});
            skLineSegment(sketch, "E189.1.1.6", {"start": v(228.75, 34.25) * mm, "end": v(220.25, 34.25) * mm});
            skLineSegment(sketch, "E189.1.1.7", {"start": v(234.75, 40.25) * mm, "end": v(228.75, 34.25) * mm});
            skLineSegment(sketch, "E189.1.1.8", {"start": v(228.75, 54.75) * mm, "end": v(234.75, 48.75) * mm});
            skLineSegment(sketch, "E189.1.1.9", {"start": v(234.75, 48.75) * mm, "end": v(234.75, 40.25) * mm});
            skCircle(sketch, "E189.1.2.0", {"center": v(224.5, 68) * mm, "radius": 10.25 * mm, "construction": true});
            skLineSegment(sketch, "E189.1.2.1", {"start": v(214.25, 63.75) * mm, "end": v(214.25, 72.25) * mm});
            skLineSegment(sketch, "E189.1.2.2", {"start": v(220.25, 78.25) * mm, "end": v(228.75, 78.25) * mm});
            skLineSegment(sketch, "E189.1.2.3", {"start": v(214.25, 72.25) * mm, "end": v(220.25, 78.25) * mm});
            skPoint(sketch, "E189.1.2.4", {"position": v(224.5, 78.25) * mm});
            skLineSegment(sketch, "E189.1.2.5", {"start": v(220.25, 57.75) * mm, "end": v(214.25, 63.75) * mm});
            skLineSegment(sketch, "E189.1.2.6", {"start": v(228.75, 57.75) * mm, "end": v(220.25, 57.75) * mm});
            skLineSegment(sketch, "E189.1.2.7", {"start": v(234.75, 63.75) * mm, "end": v(228.75, 57.75) * mm});
            skLineSegment(sketch, "E189.1.2.8", {"start": v(228.75, 78.25) * mm, "end": v(234.75, 72.25) * mm});
            skLineSegment(sketch, "E189.1.2.9", {"start": v(234.75, 72.25) * mm, "end": v(234.75, 63.75) * mm});
            skCircle(sketch, "E189.2.0.0", {"center": v(248, 21) * mm, "radius": 10.25 * mm, "construction": true});
            skLineSegment(sketch, "E189.2.0.1", {"start": v(237.75, 16.75) * mm, "end": v(237.75, 25.25) * mm});
            skLineSegment(sketch, "E189.2.0.2", {"start": v(243.75, 31.25) * mm, "end": v(252.25, 31.25) * mm});
            skLineSegment(sketch, "E189.2.0.3", {"start": v(237.75, 25.25) * mm, "end": v(243.75, 31.25) * mm});
            skPoint(sketch, "E189.2.0.4", {"position": v(248, 31.25) * mm});
            skLineSegment(sketch, "E189.2.0.5", {"start": v(243.75, 10.75) * mm, "end": v(237.75, 16.75) * mm});
            skLineSegment(sketch, "E189.2.0.6", {"start": v(252.25, 10.75) * mm, "end": v(243.75, 10.75) * mm});
            skLineSegment(sketch, "E189.2.0.7", {"start": v(258.25, 16.75) * mm, "end": v(252.25, 10.75) * mm});
            skLineSegment(sketch, "E189.2.0.8", {"start": v(252.25, 31.25) * mm, "end": v(258.25, 25.25) * mm});
            skLineSegment(sketch, "E189.2.0.9", {"start": v(258.25, 25.25) * mm, "end": v(258.25, 16.75) * mm});
            skCircle(sketch, "E189.2.1.0", {"center": v(248, 44.5) * mm, "radius": 10.25 * mm, "construction": true});
            skLineSegment(sketch, "E189.2.1.1", {"start": v(237.75, 40.25) * mm, "end": v(237.75, 48.75) * mm});
            skLineSegment(sketch, "E189.2.1.2", {"start": v(243.75, 54.75) * mm, "end": v(252.25, 54.75) * mm});
            skLineSegment(sketch, "E189.2.1.3", {"start": v(237.75, 48.75) * mm, "end": v(243.75, 54.75) * mm});
            skPoint(sketch, "E189.2.1.4", {"position": v(248, 54.75) * mm});
            skLineSegment(sketch, "E189.2.1.5", {"start": v(243.75, 34.25) * mm, "end": v(237.75, 40.25) * mm});
            skLineSegment(sketch, "E189.2.1.6", {"start": v(252.25, 34.25) * mm, "end": v(243.75, 34.25) * mm});
            skLineSegment(sketch, "E189.2.1.7", {"start": v(258.25, 40.25) * mm, "end": v(252.25, 34.25) * mm});
            skLineSegment(sketch, "E189.2.1.8", {"start": v(252.25, 54.75) * mm, "end": v(258.25, 48.75) * mm});
            skLineSegment(sketch, "E189.2.1.9", {"start": v(258.25, 48.75) * mm, "end": v(258.25, 40.25) * mm});
            skCircle(sketch, "E189.2.2.0", {"center": v(248, 68) * mm, "radius": 10.25 * mm, "construction": true});
            skLineSegment(sketch, "E189.2.2.1", {"start": v(237.75, 63.75) * mm, "end": v(237.75, 72.25) * mm});
            skLineSegment(sketch, "E189.2.2.2", {"start": v(243.75, 78.25) * mm, "end": v(252.25, 78.25) * mm});
            skLineSegment(sketch, "E189.2.2.3", {"start": v(237.75, 72.25) * mm, "end": v(243.75, 78.25) * mm});
            skPoint(sketch, "E189.2.2.4", {"position": v(248, 78.25) * mm});
            skLineSegment(sketch, "E189.2.2.5", {"start": v(243.75, 57.75) * mm, "end": v(237.75, 63.75) * mm});
            skLineSegment(sketch, "E189.2.2.6", {"start": v(252.25, 57.75) * mm, "end": v(243.75, 57.75) * mm});
            skLineSegment(sketch, "E189.2.2.7", {"start": v(258.25, 63.75) * mm, "end": v(252.25, 57.75) * mm});
            skLineSegment(sketch, "E189.2.2.8", {"start": v(252.25, 78.25) * mm, "end": v(258.25, 72.25) * mm});
            skLineSegment(sketch, "E189.2.2.9", {"start": v(258.25, 72.25) * mm, "end": v(258.25, 63.75) * mm});
            skLineSegment(sketch, "E189.direction1", {"start": v(196.75, 10.75) * mm, "end": v(220.25, 10.75) * mm, "construction": true});
            skLineSegment(sketch, "E189.direction2", {"start": v(196.75, 10.75) * mm, "end": v(196.75, 34.25) * mm, "construction": true});
            skLineSegment(sketch, "E190", {"start": v(180, 0) * mm, "end": v(180, 10.75) * mm, "construction": true});
            skLineSegment(sketch, "E191.bottom", {"start": v(180, 10.75) * mm, "end": v(187.75, 10.75) * mm});
            skLineSegment(sketch, "E191.top", {"start": v(180, 31.25) * mm, "end": v(187.75, 31.25) * mm});
            skLineSegment(sketch, "E191.left", {"start": v(180, 10.75) * mm, "end": v(180, 31.25) * mm});
            skLineSegment(sketch, "E191.right", {"start": v(187.75, 10.75) * mm, "end": v(187.75, 31.25) * mm});
            skSolve(sketch);
        }
        {
            var Q0;
            Q0 = qSketchRegion(id + "F33", true);
            extrude(context, id + "F34", {"entities" : qUnion([Q0]), "operationType" : NewBodyOperationType.REMOVE, "endBound" : BoundingType.THROUGH_ALL, "oppositeDirection" : true, "depth" : 25 * mm});
        }
        {
            var Q0;
            Q0=qCreatedBy(makeId("Top.planeOp"),FACE);
            var sketch = newSketch(context, id + "F35", { "sketchPlane" : qUnion([Q0])});
            skLineSegment(sketch, "E192", {"start": v(0, 0) * mm, "end": v(-180, 0) * mm, "construction": true});
            skLineSegment(sketch, "E193.bottom", {"start": v(-179, 0) * mm, "end": v(-90, 0) * mm});
            skLineSegment(sketch, "E193.top", {"start": v(-179, 89) * mm, "end": v(-90, 89) * mm});
            skLineSegment(sketch, "E193.left", {"start": v(-179, 0) * mm, "end": v(-179, 89) * mm});
            skLineSegment(sketch, "E193.right", {"start": v(-90, 0) * mm, "end": v(-90, 89) * mm});
            skPoint(sketch, "E193.middle", {"position": v(-134.5, 44.5) * mm});
            skLineSegment(sketch, "E194.bottom", {"start": v(-171.35, 51.35) * mm, "end": v(-127.65, 51.35) * mm, "construction": true});
            skLineSegment(sketch, "E194.top", {"start": v(-171.35, 7.65) * mm, "end": v(-127.65, 7.65) * mm, "construction": true});
            skLineSegment(sketch, "E194.left", {"start": v(-171.35, 51.35) * mm, "end": v(-171.35, 7.65) * mm, "construction": true});
            skLineSegment(sketch, "E194.right", {"start": v(-127.65, 51.35) * mm, "end": v(-127.65, 7.65) * mm, "construction": true});
            skPoint(sketch, "E194.middle", {"position": v(-149.5, 29.5) * mm});
            skCircle(sketch, "E195", {"center": v(-171.35, 51.35) * mm, "radius": 1.05 * mm});
            skCircle(sketch, "E196", {"center": v(-127.65, 51.35) * mm, "radius": 1.05 * mm});
            skCircle(sketch, "E197", {"center": v(-127.65, 7.65) * mm, "radius": 1.05 * mm});
            skCircle(sketch, "E198", {"center": v(-171.35, 7.65) * mm, "radius": 1.05 * mm});
            skLineSegment(sketch, "E199.bottom", {"start": v(-167, 47) * mm, "end": v(-132, 47) * mm});
            skLineSegment(sketch, "E199.top", {"start": v(-167, 12) * mm, "end": v(-132, 12) * mm});
            skLineSegment(sketch, "E199.left", {"start": v(-167, 47) * mm, "end": v(-167, 12) * mm});
            skLineSegment(sketch, "E199.right", {"start": v(-132, 47) * mm, "end": v(-132, 12) * mm});
            skLineSegment(sketch, "E200", {"start": v(-127.65, 7.65) * mm, "end": v(-124.5, 7.65) * mm, "construction": true});
            skLineSegment(sketch, "E201", {"start": v(-124.5, 7.65) * mm, "end": v(-124.5, 10.8) * mm, "construction": true});
            skLineSegment(sketch, "E202.bottom", {"start": v(-124.5, 10.8) * mm, "end": v(-116.75, 10.8) * mm});
            skLineSegment(sketch, "E202.top", {"start": v(-124.5, 31.3) * mm, "end": v(-116.75, 31.3) * mm});
            skLineSegment(sketch, "E202.left", {"start": v(-124.5, 10.8) * mm, "end": v(-124.5, 31.3) * mm});
            skLineSegment(sketch, "E202.right", {"start": v(-116.75, 10.8) * mm, "end": v(-116.75, 31.3) * mm});
            skLineSegment(sketch, "E203", {"start": v(0, 0) * mm, "end": v(0, 180) * mm, "construction": true});
            skLineSegment(sketch, "E204.bottom", {"start": v(0, 180) * mm, "end": v(89, 180) * mm});
            skLineSegment(sketch, "E204.top", {"start": v(0, 269) * mm, "end": v(89, 269) * mm});
            skLineSegment(sketch, "E204.left", {"start": v(0, 180) * mm, "end": v(0, 269) * mm});
            skLineSegment(sketch, "E204.right", {"start": v(89, 180) * mm, "end": v(89, 269) * mm});
            skLineSegment(sketch, "E205", {"start": v(0, 180) * mm, "end": v(9.3, 180) * mm, "construction": true});
            skLineSegment(sketch, "E206", {"start": v(9.3, 180) * mm, "end": v(9.3, 189.3) * mm, "construction": true});
            skLineSegment(sketch, "E207", {"start": v(9.3, 189.3) * mm, "end": v(32.8, 189.3) * mm, "construction": true});
            skLineSegment(sketch, "E208.bottom", {"start": v(32.8, 189.3) * mm, "end": v(76.5, 189.3) * mm, "construction": true});
            skLineSegment(sketch, "E208.top", {"start": v(32.8, 233) * mm, "end": v(76.5, 233) * mm, "construction": true});
            skLineSegment(sketch, "E208.left", {"start": v(32.8, 189.3) * mm, "end": v(32.8, 233) * mm, "construction": true});
            skLineSegment(sketch, "E208.right", {"start": v(76.5, 189.3) * mm, "end": v(76.5, 233) * mm, "construction": true});
            skLineSegment(sketch, "E209", {"start": v(9.3, 189.3) * mm, "end": v(9.3, 233) * mm, "construction": true});
            skLineSegment(sketch, "E210", {"start": v(9.3, 189.3) * mm, "end": v(9.3, 193.3) * mm, "construction": true});
            skLineSegment(sketch, "E211", {"start": v(9.3, 193.3) * mm, "end": v(13.3, 193.3) * mm, "construction": true});
            skLineSegment(sketch, "E212.bottom", {"start": v(13.3, 193.3) * mm, "end": v(72.5, 193.3) * mm});
            skLineSegment(sketch, "E212.top", {"start": v(13.3, 229) * mm, "end": v(72.5, 229) * mm});
            skLineSegment(sketch, "E212.left", {"start": v(13.3, 193.3) * mm, "end": v(13.3, 229) * mm});
            skLineSegment(sketch, "E212.right", {"start": v(72.5, 193.3) * mm, "end": v(72.5, 229) * mm});
            skCircle(sketch, "E213", {"center": v(9.3, 233) * mm, "radius": 1.05 * mm});
            skCircle(sketch, "E214", {"center": v(32.8, 233) * mm, "radius": 1.05 * mm});
            skCircle(sketch, "E215", {"center": v(76.5, 233) * mm, "radius": 1.05 * mm});
            skCircle(sketch, "E216", {"center": v(76.5, 189.3) * mm, "radius": 1.05 * mm});
            skCircle(sketch, "E217", {"center": v(32.8, 189.3) * mm, "radius": 1.05 * mm});
            skLineSegment(sketch, "E218", {"start": v(9.3, 180) * mm, "end": v(90, 180) * mm, "construction": true});
            skLineSegment(sketch, "E219", {"start": v(90, 180) * mm, "end": v(90, 192.25) * mm, "construction": true});
            skLineSegment(sketch, "E220.bottom", {"start": v(90, 192.25) * mm, "end": v(82.25, 192.25) * mm});
            skLineSegment(sketch, "E220.top", {"start": v(90, 212.75) * mm, "end": v(82.25, 212.75) * mm});
            skLineSegment(sketch, "E220.left", {"start": v(90, 192.25) * mm, "end": v(90, 212.75) * mm});
            skLineSegment(sketch, "E220.right", {"start": v(82.25, 192.25) * mm, "end": v(82.25, 212.75) * mm});
            skCircle(sketch, "E221", {"center": v(9.3, 189.3) * mm, "radius": 1.05 * mm});
            skLineSegment(sketch, "E222", {"start": v(44.5, 269) * mm, "end": v(44.5, 255) * mm, "construction": true});
            skCircle(sketch, "E223", {"center": v(44.5, 255) * mm, "radius": 1.05 * mm});
            skSolve(sketch);
        }
        {
            var Q0;
            {var subQ4=sQuery(id+"F35.wireOp",EDGE,"E204.bottom");Q0=makeQuery(id+"F35.imprint","IMPRINT",FACE,{"disambiguationData":[TD([[makeQuery(id+"F35.imprint","IMPRINT",EDGE,{"derivedFrom":subQ4}),1.0]])]});}
            extrude(context, id + "F36", {"entities" : qUnion([Q0]), "oppositeDirection" : true, "depth" : (getVariable(context, 'Grosor') / 2) * mm, "hasSecondDirection" : true, "secondDirectionOppositeDirection" : false, "secondDirectionDepth" : 3 * mm});
        }
        {
            var Q0;
            Q0=qCreatedBy(makeId("Top.planeOp"),FACE);
            var sketch = newSketch(context, id + "F37", { "sketchPlane" : qUnion([Q0])});
            skLineSegment(sketch, "E224", {"start": v(0, 0) * mm, "end": v(-180, 0) * mm, "construction": true});
            skLineSegment(sketch, "E225.bottom", {"start": v(-171.35, 51.35) * mm, "end": v(-127.65, 51.35) * mm, "construction": true});
            skLineSegment(sketch, "E225.top", {"start": v(-171.35, 7.65) * mm, "end": v(-127.65, 7.65) * mm, "construction": true});
            skLineSegment(sketch, "E225.left", {"start": v(-171.35, 51.35) * mm, "end": v(-171.35, 7.65) * mm, "construction": true});
            skLineSegment(sketch, "E225.right", {"start": v(-127.65, 51.35) * mm, "end": v(-127.65, 7.65) * mm, "construction": true});
            skPoint(sketch, "E225.middle", {"position": v(-149.5, 29.5) * mm});
            skCircle(sketch, "E226", {"center": v(-171.35, 51.35) * mm, "radius": 2.1 * mm});
            skCircle(sketch, "E227", {"center": v(-127.65, 51.35) * mm, "radius": 2.1 * mm});
            skCircle(sketch, "E228", {"center": v(-127.65, 7.65) * mm, "radius": 2.1 * mm});
            skCircle(sketch, "E229", {"center": v(-171.35, 7.65) * mm, "radius": 2.1 * mm});
            skLineSegment(sketch, "E230.bottom", {"start": v(-179.5, -0.5) * mm, "end": v(-89.5, -0.5) * mm});
            skLineSegment(sketch, "E230.top", {"start": v(-179.5, 89.5) * mm, "end": v(-89.5, 89.5) * mm});
            skLineSegment(sketch, "E230.left", {"start": v(-179.5, -0.5) * mm, "end": v(-179.5, 89.5) * mm});
            skLineSegment(sketch, "E230.right", {"start": v(-89.5, -0.5) * mm, "end": v(-89.5, 89.5) * mm});
            skPoint(sketch, "E230.middle", {"position": v(-134.5, 44.5) * mm});
            skLineSegment(sketch, "E231", {"start": v(0, 0) * mm, "end": v(0, 180) * mm, "construction": true});
            skLineSegment(sketch, "E232", {"start": v(0, 180) * mm, "end": v(9.3, 180) * mm, "construction": true});
            skLineSegment(sketch, "E233", {"start": v(9.3, 180) * mm, "end": v(9.3, 189.3) * mm, "construction": true});
            skCircle(sketch, "E234", {"center": v(9.3, 189.3) * mm, "radius": 2.05 * mm});
            skLineSegment(sketch, "E235", {"start": v(9.3, 189.3) * mm, "end": v(32.8, 189.3) * mm, "construction": true});
            skLineSegment(sketch, "E236.bottom", {"start": v(32.8, 189.3) * mm, "end": v(76.5, 189.3) * mm, "construction": true});
            skLineSegment(sketch, "E236.top", {"start": v(32.8, 233) * mm, "end": v(76.5, 233) * mm, "construction": true});
            skLineSegment(sketch, "E236.left", {"start": v(32.8, 189.3) * mm, "end": v(32.8, 233) * mm, "construction": true});
            skLineSegment(sketch, "E236.right", {"start": v(76.5, 189.3) * mm, "end": v(76.5, 233) * mm, "construction": true});
            skLineSegment(sketch, "E237", {"start": v(9.3, 189.3) * mm, "end": v(9.3, 233) * mm, "construction": true});
            skCircle(sketch, "E238", {"center": v(9.3, 233) * mm, "radius": 2.05 * mm});
            skCircle(sketch, "E239", {"center": v(32.8, 233) * mm, "radius": 2.05 * mm});
            skCircle(sketch, "E240", {"center": v(76.5, 233) * mm, "radius": 2.05 * mm});
            skCircle(sketch, "E241", {"center": v(76.5, 189.3) * mm, "radius": 2.05 * mm});
            skCircle(sketch, "E242", {"center": v(32.8, 189.3) * mm, "radius": 2.05 * mm});
            skLineSegment(sketch, "E243.bottom", {"start": v(0, 180) * mm, "end": v(89, 180) * mm});
            skLineSegment(sketch, "E243.top", {"start": v(0, 269) * mm, "end": v(89, 269) * mm});
            skLineSegment(sketch, "E243.left", {"start": v(0, 180) * mm, "end": v(0, 269) * mm});
            skLineSegment(sketch, "E243.right", {"start": v(89, 180) * mm, "end": v(89, 269) * mm});
            skSolve(sketch);
        }
        {
            var Q0;
            Q0=makeQuery(id+"F37.imprint","IMPRINT",FACE,{"disambiguationData":[TD([[makeQuery(id+"F37.imprint","IMPRINT",EDGE,{"derivedFrom":sQuery(id+"F37.wireOp",EDGE,"E234")}),-1.0]])]});
            extrude(context, id + "F38", {"entities" : qUnion([Q0]), "operationType" : NewBodyOperationType.REMOVE, "depth" : 25 * mm});
        }
        {
            var Q0;
            Q0=makeQuery(id+"F26.opExtrude","SWEPT_EDGE",EDGE,{"disambiguationData":[OSD([sQuery(id+"F25.wireOp",EDGE,"Wud6Z5jM-8rQq-3mEt-tfTX-94YiYB74VQni.bottom"),sQuery(id+"F25.wireOp",EDGE,"Wud6Z5jM-8rQq-3mEt-tfTX-94YiYB74VQni.right")])]});
            var Q1;
            Q1=makeQuery(id+"F26.opExtrude","SWEPT_EDGE",EDGE,{"disambiguationData":[OSD([sQuery(id+"F25.wireOp",EDGE,"Wud6Z5jM-8rQq-3mEt-tfTX-94YiYB74VQni.bottom"),sQuery(id+"F25.wireOp",EDGE,"Wud6Z5jM-8rQq-3mEt-tfTX-94YiYB74VQni.left")])]});
            var Q2;
            Q2=makeQuery(id+"F36.opExtrude","SWEPT_EDGE",EDGE,{"disambiguationData":[OSD([sQuery(id+"F35.wireOp",EDGE,"E193.bottom"),sQuery(id+"F35.wireOp",EDGE,"E193.right")])]});
            var Q3;
            Q3=makeQuery(id+"F36.opExtrude","SWEPT_EDGE",EDGE,{"disambiguationData":[OSD([sQuery(id+"F35.wireOp",EDGE,"E193.bottom"),sQuery(id+"F35.wireOp",EDGE,"E193.left")])]});
            var Q4;
            Q4=makeQuery(id+"F26.opExtrude","SWEPT_EDGE",EDGE,{"disambiguationData":[OSD([sQuery(id+"F25.wireOp",EDGE,"E152.bottom"),sQuery(id+"F25.wireOp",EDGE,"E152.left")])]});
            var Q5;
            Q5=makeQuery(id+"F26.opExtrude","SWEPT_EDGE",EDGE,{"disambiguationData":[OSD([sQuery(id+"F25.wireOp",EDGE,"E152.bottom"),sQuery(id+"F25.wireOp",EDGE,"E152.right")])]});
            var Q6;
            Q6=makeQuery(id+"F36.opExtrude","SWEPT_EDGE",EDGE,{"disambiguationData":[OSD([sQuery(id+"F35.wireOp",EDGE,"E204.bottom"),sQuery(id+"F35.wireOp",EDGE,"E204.right")])]});
            var Q7;
            Q7=makeQuery(id+"F36.opExtrude","SWEPT_EDGE",EDGE,{"disambiguationData":[OSD([sQuery(id+"F35.wireOp",EDGE,"E204.bottom"),sQuery(id+"F35.wireOp",EDGE,"E204.left")])]});
            fillet(context, id + "F39", {"entities" : qUnion([Q0, Q1, Q2, Q3, Q4, Q5, Q6, Q7]), "radius" : 3 * mm, "tangentPropagation" : true, "allowEdgeOverflow" : false});
        }
        {
            var Q0;
            Q0=makeQuery(id+"F36.opExtrude","SWEPT_EDGE",EDGE,{"disambiguationData":[OSD([sQuery(id+"F35.wireOp",EDGE,"E193.top"),sQuery(id+"F35.wireOp",EDGE,"E193.left")])]});
            var Q1;
            Q1=makeQuery(id+"F36.opExtrude","SWEPT_EDGE",EDGE,{"disambiguationData":[OSD([sQuery(id+"F35.wireOp",EDGE,"E193.top"),sQuery(id+"F35.wireOp",EDGE,"E193.right")])]});
            var Q2;
            Q2=makeQuery(id+"F26.opExtrude","SWEPT_EDGE",EDGE,{"disambiguationData":[OSD([sQuery(id+"F25.wireOp",EDGE,"Wud6Z5jM-8rQq-3mEt-tfTX-94YiYB74VQni.top"),sQuery(id+"F25.wireOp",EDGE,"Wud6Z5jM-8rQq-3mEt-tfTX-94YiYB74VQni.left")])]});
            var Q3;
            Q3=makeQuery(id+"F26.opExtrude","SWEPT_EDGE",EDGE,{"disambiguationData":[OSD([sQuery(id+"F25.wireOp",EDGE,"Wud6Z5jM-8rQq-3mEt-tfTX-94YiYB74VQni.top"),sQuery(id+"F25.wireOp",EDGE,"Wud6Z5jM-8rQq-3mEt-tfTX-94YiYB74VQni.right")])]});
            var Q4;
            Q4=makeQuery(id+"F26.opExtrude","SWEPT_EDGE",EDGE,{"disambiguationData":[OSD([sQuery(id+"F25.wireOp",EDGE,"E152.top"),sQuery(id+"F25.wireOp",EDGE,"E152.right")])]});
            var Q5;
            Q5=makeQuery(id+"F26.opExtrude","SWEPT_EDGE",EDGE,{"disambiguationData":[OSD([sQuery(id+"F25.wireOp",EDGE,"E152.top"),sQuery(id+"F25.wireOp",EDGE,"E152.left")])]});
            var Q6;
            Q6=makeQuery(id+"F36.opExtrude","SWEPT_EDGE",EDGE,{"disambiguationData":[OSD([sQuery(id+"F35.wireOp",EDGE,"E204.top"),sQuery(id+"F35.wireOp",EDGE,"E204.right")])]});
            var Q7;
            Q7=makeQuery(id+"F36.opExtrude","SWEPT_EDGE",EDGE,{"disambiguationData":[OSD([sQuery(id+"F35.wireOp",EDGE,"E204.top"),sQuery(id+"F35.wireOp",EDGE,"E204.left")])]});
            chamfer(context, id + "F40", {"entities" : qUnion([Q0, Q1, Q2, Q3, Q4, Q5, Q6, Q7]), "width" : 3 * mm, "tangentPropagation" : true});
        }
    });
